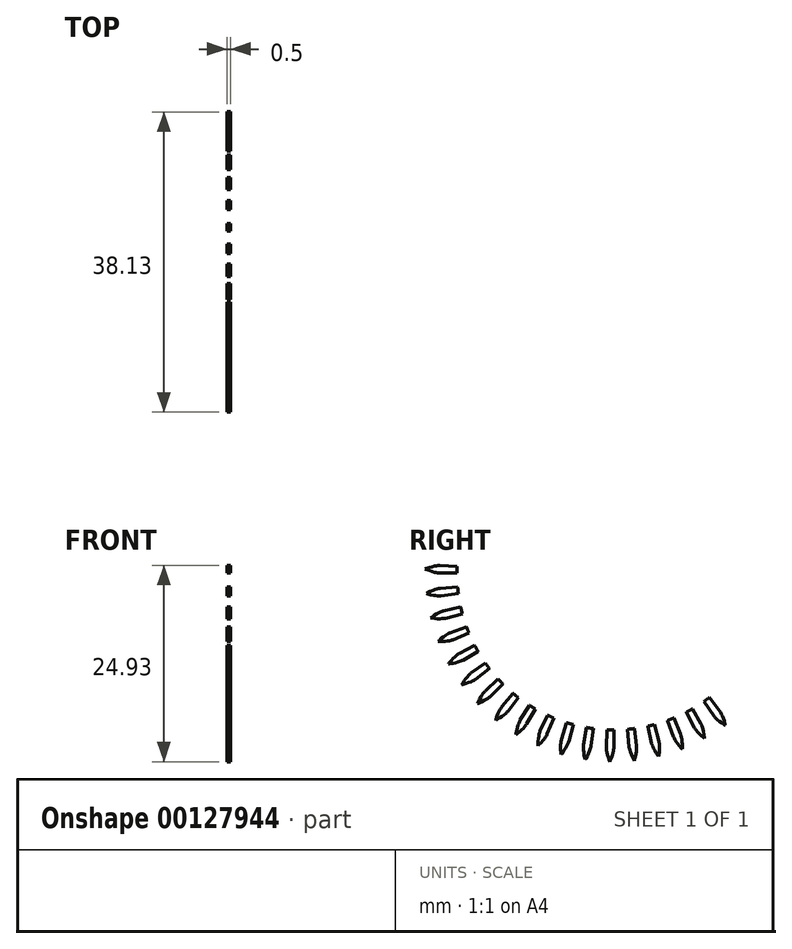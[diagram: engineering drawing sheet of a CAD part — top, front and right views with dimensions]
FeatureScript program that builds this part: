
annotation { "Feature Type Name" : "Feature", "Feature Type Description" : "" }
export const myFeature = defineFeature(function(context is Context, id is Id, definition is map)
    precondition{}
    {
        {
            assignVariable(context, id + "F0", {"name" : "GearThickness", "anyValue" : .5});
        }
        {
            var Q0;
            Q0=qCreatedBy(makeId("Right.planeOp"),FACE);
            var sketch = newSketch(context, id + "F1", { "sketchPlane" : qUnion([Q0])});
            skCircle(sketch, "E0", {"center": v(0, 0) * mm, "radius": 19.92 * mm});
            skCircle(sketch, "E1", {"center": v(0, 0) * mm, "radius": 22.13 * mm, "construction": true});
            skCircle(sketch, "E2", {"center": v(0, 0) * mm, "radius": 22.86 * mm, "construction": true});
            skCircle(sketch, "E3", {"center": v(0, 0) * mm, "radius": 25.4 * mm});
            skLineSegment(sketch, "E4", {"start": v(0, 0) * mm, "end": v(-22.13, 0) * mm, "construction": true});
            skLineSegment(sketch, "E5.1.0", {"start": v(0, 0) * mm, "end": v(-22.1, 1.1) * mm, "construction": true});
            skLineSegment(sketch, "E5.2.0", {"start": v(0, 0) * mm, "end": v(-22.02, 2.2) * mm, "construction": true});
            skLineSegment(sketch, "E5.3.0", {"start": v(0, 0) * mm, "end": v(-21.88, 3.3) * mm, "construction": true});
            skLineSegment(sketch, "E5.4.0", {"start": v(0, 0) * mm, "end": v(-21.7, 4.4) * mm, "construction": true});
            skLineSegment(sketch, "E5.5.0", {"start": v(0, 0) * mm, "end": v(-21.44, 5.48) * mm, "construction": true});
            skLineSegment(sketch, "E5.6.0", {"start": v(0, 0) * mm, "end": v(-21.14, 6.54) * mm, "construction": true});
            skLineSegment(sketch, "E5.7.0", {"start": v(0, 0) * mm, "end": v(-20.8, 7.59) * mm, "construction": true});
            skLineSegment(sketch, "E5.8.0", {"start": v(0, 0) * mm, "end": v(-20.38, 8.62) * mm, "construction": true});
            skLineSegment(sketch, "E5.9.0", {"start": v(0, 0) * mm, "end": v(-19.93, 9.63) * mm, "construction": true});
            skLineSegment(sketch, "E5.10.0", {"start": v(0, 0) * mm, "end": v(-19.42, 10.61) * mm, "construction": true});
            skLineSegment(sketch, "E5.11.0", {"start": v(0, 0) * mm, "end": v(-18.87, 11.57) * mm, "construction": true});
            skLineSegment(sketch, "E5.12.0", {"start": v(0, 0) * mm, "end": v(-18.27, 12.5) * mm, "construction": true});
            skLineSegment(sketch, "E5.13.0", {"start": v(0, 0) * mm, "end": v(-17.62, 13.4) * mm, "construction": true});
            skLineSegment(sketch, "E5.14.0", {"start": v(0, 0) * mm, "end": v(-16.93, 14.26) * mm, "construction": true});
            skLineSegment(sketch, "E5.anchor2", {"start": v(0, 0) * mm, "end": v(-16.93, 14.26) * mm, "construction": true});
            skLineSegment(sketch, "E6", {"start": v(-22.1, 1.1) * mm, "end": v(-22.16, 0) * mm, "construction": true});
            skLineSegment(sketch, "E7", {"start": v(-22.02, 2.2) * mm, "end": v(-22.24, 0) * mm, "construction": true});
            skLineSegment(sketch, "E8", {"start": v(-21.88, 3.3) * mm, "end": v(-22.38, 0.02) * mm, "construction": true});
            skLineSegment(sketch, "E9", {"start": v(-21.44, 5.48) * mm, "end": v(-22.81, 0.11) * mm, "construction": true});
            skLineSegment(sketch, "E10", {"start": v(-21.14, 6.54) * mm, "end": v(-23.1, 0.2) * mm, "construction": true});
            skLineSegment(sketch, "E11", {"start": v(-20.8, 7.59) * mm, "end": v(-23.45, 0.31) * mm, "construction": true});
            skLineSegment(sketch, "E12", {"start": v(-20.38, 8.62) * mm, "end": v(-23.83, 0.46) * mm, "construction": true});
            skLineSegment(sketch, "E13", {"start": v(-19.93, 9.63) * mm, "end": v(-24.26, 0.66) * mm, "construction": true});
            skLineSegment(sketch, "E14", {"start": v(-19.42, 10.61) * mm, "end": v(-24.73, 0.9) * mm, "construction": true});
            skLineSegment(sketch, "E15", {"start": v(-18.87, 11.57) * mm, "end": v(-25.23, 1.2) * mm, "construction": true});
            skLineSegment(sketch, "E16", {"start": v(-21.7, 4.4) * mm, "end": v(-22.57, 0.06) * mm, "construction": true});
            skLineSegment(sketch, "E17", {"start": v(-18.27, 12.5) * mm, "end": v(-25.76, 1.54) * mm, "construction": true});
            skLineSegment(sketch, "E18", {"start": v(-17.62, 13.4) * mm, "end": v(-26.32, 1.94) * mm, "construction": true});
            skLineSegment(sketch, "E19", {"start": v(-16.93, 14.26) * mm, "end": v(-26.9, 2.4) * mm, "construction": true});
            skLineSegment(sketch, "E20", {"start": v(0, 0) * mm, "end": v(-22.05, 1.93) * mm, "construction": true});
            skLineSegment(sketch, "E21", {"start": v(-19.92, 0) * mm, "end": v(-22.13, 0) * mm});
            skLineSegment(sketch, "E22.MirrorCS", {"start": v(-19.62, 3.46) * mm, "end": v(-21.8, 3.84) * mm});
            skLineSegment(sketch, "E23", {"start": v(-22.13, 0) * mm, "end": v(-22.16, 0) * mm});
            skLineSegment(sketch, "E24", {"start": v(-22.16, 0) * mm, "end": v(-22.24, 0) * mm});
            skLineSegment(sketch, "E25", {"start": v(-22.24, 0) * mm, "end": v(-22.38, 0.02) * mm});
            skLineSegment(sketch, "E26", {"start": v(-22.38, 0.02) * mm, "end": v(-22.57, 0.06) * mm});
            skLineSegment(sketch, "E27", {"start": v(-22.57, 0.06) * mm, "end": v(-22.81, 0.11) * mm});
            skLineSegment(sketch, "E28", {"start": v(-22.81, 0.11) * mm, "end": v(-23.1, 0.2) * mm});
            skLineSegment(sketch, "E29", {"start": v(-23.1, 0.2) * mm, "end": v(-23.45, 0.31) * mm});
            skLineSegment(sketch, "E30", {"start": v(-23.45, 0.31) * mm, "end": v(-23.83, 0.46) * mm});
            skLineSegment(sketch, "E31", {"start": v(-23.83, 0.46) * mm, "end": v(-24.26, 0.66) * mm});
            skLineSegment(sketch, "E32", {"start": v(-24.26, 0.66) * mm, "end": v(-24.73, 0.9) * mm});
            skLineSegment(sketch, "E33", {"start": v(-24.73, 0.9) * mm, "end": v(-25.23, 1.2) * mm});
            skLineSegment(sketch, "E34", {"start": v(-25.23, 1.2) * mm, "end": v(-25.76, 1.54) * mm});
            skLineSegment(sketch, "E35", {"start": v(-25.76, 1.54) * mm, "end": v(-26.32, 1.94) * mm});
            skLineSegment(sketch, "E36", {"start": v(-26.32, 1.94) * mm, "end": v(-26.9, 2.4) * mm});
            skLineSegment(sketch, "E37.MirrorCS", {"start": v(-21.8, 3.84) * mm, "end": v(-21.82, 3.85) * mm});
            skLineSegment(sketch, "E38.MirrorCS", {"start": v(-21.82, 3.85) * mm, "end": v(-21.9, 3.86) * mm});
            skLineSegment(sketch, "E39.MirrorCS", {"start": v(-21.9, 3.86) * mm, "end": v(-22.04, 3.86) * mm});
            skLineSegment(sketch, "E40.MirrorCS", {"start": v(-22.04, 3.86) * mm, "end": v(-22.24, 3.86) * mm});
            skLineSegment(sketch, "E41.MirrorCS", {"start": v(-22.49, 3.85) * mm, "end": v(-22.79, 3.82) * mm});
            skLineSegment(sketch, "E42.MirrorCS", {"start": v(-22.79, 3.82) * mm, "end": v(-23.14, 3.76) * mm});
            skLineSegment(sketch, "E43.MirrorCS", {"start": v(-23.14, 3.76) * mm, "end": v(-23.55, 3.68) * mm});
            skLineSegment(sketch, "E44.MirrorCS", {"start": v(-23.55, 3.68) * mm, "end": v(-24, 3.56) * mm});
            skLineSegment(sketch, "E45.MirrorCS", {"start": v(-24.5, 3.4) * mm, "end": v(-25.05, 3.2) * mm});
            skLineSegment(sketch, "E46.MirrorCS", {"start": v(-24, 3.56) * mm, "end": v(-24.5, 3.4) * mm});
            skLineSegment(sketch, "E47.MirrorCS", {"start": v(-25.05, 3.2) * mm, "end": v(-25.64, 2.96) * mm});
            skLineSegment(sketch, "E48.MirrorCS", {"start": v(-25.64, 2.96) * mm, "end": v(-26.26, 2.66) * mm});
            skLineSegment(sketch, "E49.MirrorCS", {"start": v(-26.26, 2.66) * mm, "end": v(-26.92, 2.3) * mm});
            skLineSegment(sketch, "E50.MirrorCS", {"start": v(-22.24, 3.86) * mm, "end": v(-22.49, 3.85) * mm});
            skLineSegment(sketch, "E51.1.0", {"start": v(-19.75, -2.6) * mm, "end": v(-21.94, -2.89) * mm});
            skLineSegment(sketch, "E51.1.1", {"start": v(-25.26, -0.09) * mm, "end": v(-25.8, -0.41) * mm});
            skLineSegment(sketch, "E51.1.2", {"start": v(-19.9, 0.87) * mm, "end": v(-22.11, 0.97) * mm});
            skLineSegment(sketch, "E51.1.3", {"start": v(-24.74, 0.18) * mm, "end": v(-25.26, -0.09) * mm});
            skLineSegment(sketch, "E51.1.4", {"start": v(-24.63, -2.34) * mm, "end": v(-25.17, -2.11) * mm});
            skLineSegment(sketch, "E51.1.5", {"start": v(-25.17, -2.11) * mm, "end": v(-25.74, -1.84) * mm});
            skLineSegment(sketch, "E51.1.6", {"start": v(-24.27, 0.4) * mm, "end": v(-24.74, 0.18) * mm});
            skLineSegment(sketch, "E51.1.7", {"start": v(-26.38, -0.8) * mm, "end": v(-26.99, -1.23) * mm});
            skLineSegment(sketch, "E51.1.8", {"start": v(-23.83, 0.58) * mm, "end": v(-24.27, 0.4) * mm});
            skLineSegment(sketch, "E51.1.9", {"start": v(-26.35, -1.51) * mm, "end": v(-27, -1.12) * mm});
            skLineSegment(sketch, "E51.1.10", {"start": v(-25.8, -0.41) * mm, "end": v(-26.38, -0.8) * mm});
            skLineSegment(sketch, "E51.1.11", {"start": v(-24.14, -2.51) * mm, "end": v(-24.63, -2.34) * mm});
            skLineSegment(sketch, "E51.1.12", {"start": v(-25.74, -1.84) * mm, "end": v(-26.35, -1.51) * mm});
            skLineSegment(sketch, "E51.1.13", {"start": v(-22.8, 0.88) * mm, "end": v(-23.1, 0.81) * mm});
            skLineSegment(sketch, "E51.1.14", {"start": v(-23.1, 0.81) * mm, "end": v(-23.44, 0.71) * mm});
            skLineSegment(sketch, "E51.1.15", {"start": v(-23.44, 0.71) * mm, "end": v(-23.83, 0.58) * mm});
            skLineSegment(sketch, "E51.1.16", {"start": v(-23.29, -2.75) * mm, "end": v(-23.69, -2.65) * mm});
            skLineSegment(sketch, "E51.1.17", {"start": v(-22.93, -2.82) * mm, "end": v(-23.29, -2.75) * mm});
            skLineSegment(sketch, "E51.1.18", {"start": v(-23.69, -2.65) * mm, "end": v(-24.14, -2.51) * mm});
            skLineSegment(sketch, "E51.1.19", {"start": v(-22.55, 0.93) * mm, "end": v(-22.8, 0.88) * mm});
            skLineSegment(sketch, "E51.1.20", {"start": v(-22.36, 0.95) * mm, "end": v(-22.55, 0.93) * mm});
            skLineSegment(sketch, "E51.1.21", {"start": v(-22.63, -2.86) * mm, "end": v(-22.93, -2.82) * mm});
            skLineSegment(sketch, "E51.1.22", {"start": v(-22.38, -2.89) * mm, "end": v(-22.63, -2.86) * mm});
            skLineSegment(sketch, "E51.1.23", {"start": v(-22.05, -2.9) * mm, "end": v(-22.2, -2.9) * mm});
            skLineSegment(sketch, "E51.1.24", {"start": v(-22.11, 0.97) * mm, "end": v(-22.14, 0.97) * mm});
            skLineSegment(sketch, "E51.1.25", {"start": v(-22.14, 0.97) * mm, "end": v(-22.22, 0.96) * mm});
            skLineSegment(sketch, "E51.1.26", {"start": v(-22.2, -2.9) * mm, "end": v(-22.38, -2.89) * mm});
            skLineSegment(sketch, "E51.1.27", {"start": v(-22.22, 0.96) * mm, "end": v(-22.36, 0.95) * mm});
            skLineSegment(sketch, "E51.1.28", {"start": v(-21.97, -2.9) * mm, "end": v(-22.05, -2.9) * mm});
            skLineSegment(sketch, "E51.1.29", {"start": v(-21.94, -2.89) * mm, "end": v(-21.97, -2.9) * mm});
            skLineSegment(sketch, "E51.2.0", {"start": v(-19.24, -5.16) * mm, "end": v(-21.38, -5.73) * mm});
            skLineSegment(sketch, "E51.2.1", {"start": v(-25.03, -3.39) * mm, "end": v(-25.53, -3.78) * mm});
            skLineSegment(sketch, "E51.2.2", {"start": v(-19.85, -1.74) * mm, "end": v(-22.05, -1.93) * mm});
            skLineSegment(sketch, "E51.2.3", {"start": v(-24.56, -3.05) * mm, "end": v(-25.03, -3.39) * mm});
            skLineSegment(sketch, "E51.2.4", {"start": v(-24.12, -5.53) * mm, "end": v(-24.68, -5.38) * mm});
            skLineSegment(sketch, "E51.2.5", {"start": v(-24.68, -5.38) * mm, "end": v(-25.28, -5.18) * mm});
            skLineSegment(sketch, "E51.2.6", {"start": v(-24.11, -2.77) * mm, "end": v(-24.56, -3.05) * mm});
            skLineSegment(sketch, "E51.2.7", {"start": v(-26.06, -4.23) * mm, "end": v(-26.6, -4.74) * mm});
            skLineSegment(sketch, "E51.2.8", {"start": v(-23.7, -2.54) * mm, "end": v(-24.11, -2.77) * mm});
            skLineSegment(sketch, "E51.2.9", {"start": v(-25.93, -4.94) * mm, "end": v(-26.61, -4.64) * mm});
            skLineSegment(sketch, "E51.2.10", {"start": v(-25.53, -3.78) * mm, "end": v(-26.06, -4.23) * mm});
            skLineSegment(sketch, "E51.2.11", {"start": v(-23.6, -5.64) * mm, "end": v(-24.12, -5.53) * mm});
            skLineSegment(sketch, "E51.2.12", {"start": v(-25.28, -5.18) * mm, "end": v(-25.93, -4.94) * mm});
            skLineSegment(sketch, "E51.2.13", {"start": v(-22.72, -2.1) * mm, "end": v(-23, -2.21) * mm});
            skLineSegment(sketch, "E51.2.14", {"start": v(-23, -2.21) * mm, "end": v(-23.33, -2.35) * mm});
            skLineSegment(sketch, "E51.2.15", {"start": v(-23.33, -2.35) * mm, "end": v(-23.7, -2.54) * mm});
            skLineSegment(sketch, "E51.2.16", {"start": v(-22.73, -5.77) * mm, "end": v(-23.14, -5.72) * mm});
            skLineSegment(sketch, "E51.2.17", {"start": v(-22.37, -5.79) * mm, "end": v(-22.73, -5.77) * mm});
            skLineSegment(sketch, "E51.2.18", {"start": v(-23.14, -5.72) * mm, "end": v(-23.6, -5.64) * mm});
            skLineSegment(sketch, "E51.2.19", {"start": v(-22.48, -2.03) * mm, "end": v(-22.72, -2.1) * mm});
            skLineSegment(sketch, "E51.2.20", {"start": v(-22.3, -1.98) * mm, "end": v(-22.48, -2.03) * mm});
            skLineSegment(sketch, "E51.2.21", {"start": v(-22.07, -5.8) * mm, "end": v(-22.37, -5.79) * mm});
            skLineSegment(sketch, "E51.2.22", {"start": v(-21.82, -5.78) * mm, "end": v(-22.07, -5.8) * mm});
            skLineSegment(sketch, "E51.2.23", {"start": v(-21.49, -5.75) * mm, "end": v(-21.62, -5.77) * mm});
            skLineSegment(sketch, "E51.2.24", {"start": v(-22.05, -1.93) * mm, "end": v(-22.08, -1.93) * mm});
            skLineSegment(sketch, "E51.2.25", {"start": v(-22.08, -1.93) * mm, "end": v(-22.16, -1.95) * mm});
            skLineSegment(sketch, "E51.2.26", {"start": v(-21.62, -5.77) * mm, "end": v(-21.82, -5.78) * mm});
            skLineSegment(sketch, "E51.2.27", {"start": v(-22.16, -1.95) * mm, "end": v(-22.3, -1.98) * mm});
            skLineSegment(sketch, "E51.2.28", {"start": v(-21.4, -5.73) * mm, "end": v(-21.49, -5.75) * mm});
            skLineSegment(sketch, "E51.2.29", {"start": v(-21.38, -5.73) * mm, "end": v(-21.4, -5.73) * mm});
            skLineSegment(sketch, "E51.3.0", {"start": v(-18.4, -7.62) * mm, "end": v(-20.45, -8.47) * mm});
            skLineSegment(sketch, "E51.3.1", {"start": v(-24.37, -6.62) * mm, "end": v(-24.82, -7.08) * mm});
            skLineSegment(sketch, "E51.3.2", {"start": v(-19.45, -4.31) * mm, "end": v(-21.6, -4.8) * mm});
            skLineSegment(sketch, "E51.3.3", {"start": v(-23.95, -6.23) * mm, "end": v(-24.37, -6.62) * mm});
            skLineSegment(sketch, "E51.3.4", {"start": v(-23.19, -8.63) * mm, "end": v(-23.77, -8.56) * mm});
            skLineSegment(sketch, "E51.3.5", {"start": v(-23.77, -8.56) * mm, "end": v(-24.4, -8.44) * mm});
            skLineSegment(sketch, "E51.3.6", {"start": v(-23.54, -5.9) * mm, "end": v(-23.95, -6.23) * mm});
            skLineSegment(sketch, "E51.3.7", {"start": v(-25.28, -7.6) * mm, "end": v(-25.75, -8.18) * mm});
            skLineSegment(sketch, "E51.3.8", {"start": v(-23.17, -5.61) * mm, "end": v(-23.54, -5.9) * mm});
            skLineSegment(sketch, "E51.3.9", {"start": v(-25.06, -8.28) * mm, "end": v(-25.78, -8.07) * mm});
            skLineSegment(sketch, "E51.3.10", {"start": v(-24.82, -7.08) * mm, "end": v(-25.28, -7.6) * mm});
            skLineSegment(sketch, "E51.3.11", {"start": v(-22.67, -8.68) * mm, "end": v(-23.19, -8.63) * mm});
            skLineSegment(sketch, "E51.3.12", {"start": v(-24.4, -8.44) * mm, "end": v(-25.06, -8.28) * mm});
            skLineSegment(sketch, "E51.3.13", {"start": v(-22.25, -5.05) * mm, "end": v(-22.52, -5.2) * mm});
            skLineSegment(sketch, "E51.3.14", {"start": v(-22.52, -5.2) * mm, "end": v(-22.82, -5.38) * mm});
            skLineSegment(sketch, "E51.3.15", {"start": v(-22.82, -5.38) * mm, "end": v(-23.17, -5.61) * mm});
            skLineSegment(sketch, "E51.3.16", {"start": v(-21.78, -8.68) * mm, "end": v(-22.2, -8.7) * mm});
            skLineSegment(sketch, "E51.3.17", {"start": v(-21.42, -8.66) * mm, "end": v(-21.78, -8.68) * mm});
            skLineSegment(sketch, "E51.3.18", {"start": v(-22.2, -8.7) * mm, "end": v(-22.67, -8.68) * mm});
            skLineSegment(sketch, "E51.3.19", {"start": v(-22.02, -4.94) * mm, "end": v(-22.25, -5.05) * mm});
            skLineSegment(sketch, "E51.3.20", {"start": v(-21.84, -4.87) * mm, "end": v(-22.02, -4.94) * mm});
            skLineSegment(sketch, "E51.3.21", {"start": v(-21.12, -8.62) * mm, "end": v(-21.42, -8.66) * mm});
            skLineSegment(sketch, "E51.3.22", {"start": v(-20.87, -8.58) * mm, "end": v(-21.12, -8.62) * mm});
            skLineSegment(sketch, "E51.3.23", {"start": v(-20.55, -8.5) * mm, "end": v(-20.69, -8.54) * mm});
            skLineSegment(sketch, "E51.3.24", {"start": v(-21.6, -4.8) * mm, "end": v(-21.63, -4.8) * mm});
            skLineSegment(sketch, "E51.3.25", {"start": v(-21.63, -4.8) * mm, "end": v(-21.71, -4.82) * mm});
            skLineSegment(sketch, "E51.3.26", {"start": v(-20.69, -8.54) * mm, "end": v(-20.87, -8.58) * mm});
            skLineSegment(sketch, "E51.3.27", {"start": v(-21.71, -4.82) * mm, "end": v(-21.84, -4.87) * mm});
            skLineSegment(sketch, "E51.3.28", {"start": v(-20.47, -8.48) * mm, "end": v(-20.55, -8.5) * mm});
            skLineSegment(sketch, "E51.3.29", {"start": v(-20.45, -8.47) * mm, "end": v(-20.47, -8.48) * mm});
            skLineSegment(sketch, "E51.4.0", {"start": v(-17.25, -9.96) * mm, "end": v(-19.17, -11.07) * mm});
            skLineSegment(sketch, "E51.4.1", {"start": v(-23.3, -9.75) * mm, "end": v(-23.68, -10.26) * mm});
            skLineSegment(sketch, "E51.4.2", {"start": v(-18.72, -6.81) * mm, "end": v(-20.8, -7.57) * mm});
            skLineSegment(sketch, "E51.4.3", {"start": v(-22.93, -9.3) * mm, "end": v(-23.3, -9.75) * mm});
            skLineSegment(sketch, "E51.4.4", {"start": v(-21.86, -11.59) * mm, "end": v(-22.45, -11.58) * mm});
            skLineSegment(sketch, "E51.4.5", {"start": v(-22.45, -11.58) * mm, "end": v(-23.08, -11.55) * mm});
            skLineSegment(sketch, "E51.4.6", {"start": v(-22.57, -8.92) * mm, "end": v(-22.93, -9.3) * mm});
            skLineSegment(sketch, "E51.4.7", {"start": v(-24.07, -10.83) * mm, "end": v(-24.46, -11.47) * mm});
            skLineSegment(sketch, "E51.4.8", {"start": v(-22.24, -8.59) * mm, "end": v(-22.57, -8.92) * mm});
            skLineSegment(sketch, "E51.4.9", {"start": v(-23.77, -11.48) * mm, "end": v(-24.5, -11.37) * mm});
            skLineSegment(sketch, "E51.4.10", {"start": v(-23.68, -10.26) * mm, "end": v(-24.07, -10.83) * mm});
            skLineSegment(sketch, "E51.4.11", {"start": v(-21.34, -11.56) * mm, "end": v(-21.86, -11.59) * mm});
            skLineSegment(sketch, "E51.4.12", {"start": v(-23.08, -11.55) * mm, "end": v(-23.77, -11.48) * mm});
            skLineSegment(sketch, "E51.4.13", {"start": v(-21.4, -7.91) * mm, "end": v(-21.64, -8.09) * mm});
            skLineSegment(sketch, "E51.4.14", {"start": v(-21.64, -8.09) * mm, "end": v(-21.93, -8.31) * mm});
            skLineSegment(sketch, "E51.4.15", {"start": v(-21.93, -8.31) * mm, "end": v(-22.24, -8.59) * mm});
            skLineSegment(sketch, "E51.4.16", {"start": v(-20.46, -11.45) * mm, "end": v(-20.87, -11.51) * mm});
            skLineSegment(sketch, "E51.4.17", {"start": v(-20.1, -11.38) * mm, "end": v(-20.46, -11.45) * mm});
            skLineSegment(sketch, "E51.4.18", {"start": v(-20.87, -11.51) * mm, "end": v(-21.34, -11.56) * mm});
            skLineSegment(sketch, "E51.4.19", {"start": v(-21.19, -7.77) * mm, "end": v(-21.4, -7.91) * mm});
            skLineSegment(sketch, "E51.4.20", {"start": v(-21.02, -7.68) * mm, "end": v(-21.19, -7.77) * mm});
            skLineSegment(sketch, "E51.4.21", {"start": v(-19.81, -11.3) * mm, "end": v(-20.1, -11.38) * mm});
            skLineSegment(sketch, "E51.4.22", {"start": v(-19.58, -11.23) * mm, "end": v(-19.81, -11.3) * mm});
            skLineSegment(sketch, "E51.4.23", {"start": v(-19.27, -11.11) * mm, "end": v(-19.4, -11.17) * mm});
            skLineSegment(sketch, "E51.4.24", {"start": v(-20.8, -7.57) * mm, "end": v(-20.82, -7.58) * mm});
            skLineSegment(sketch, "E51.4.25", {"start": v(-20.82, -7.58) * mm, "end": v(-20.9, -7.61) * mm});
            skLineSegment(sketch, "E51.4.26", {"start": v(-19.4, -11.17) * mm, "end": v(-19.58, -11.23) * mm});
            skLineSegment(sketch, "E51.4.27", {"start": v(-20.9, -7.61) * mm, "end": v(-21.02, -7.68) * mm});
            skLineSegment(sketch, "E51.4.28", {"start": v(-19.2, -11.08) * mm, "end": v(-19.27, -11.11) * mm});
            skLineSegment(sketch, "E51.4.29", {"start": v(-19.17, -11.07) * mm, "end": v(-19.2, -11.08) * mm});
            skLineSegment(sketch, "E51.5.0", {"start": v(-15.8, -12.13) * mm, "end": v(-17.56, -13.47) * mm});
            skLineSegment(sketch, "E51.5.1", {"start": v(-21.83, -12.7) * mm, "end": v(-22.14, -13.26) * mm});
            skLineSegment(sketch, "E51.5.2", {"start": v(-17.67, -9.2) * mm, "end": v(-19.63, -10.22) * mm});
            skLineSegment(sketch, "E51.5.3", {"start": v(-21.52, -12.22) * mm, "end": v(-21.83, -12.7) * mm});
            skLineSegment(sketch, "E51.5.4", {"start": v(-20.17, -14.34) * mm, "end": v(-20.74, -14.41) * mm});
            skLineSegment(sketch, "E51.5.5", {"start": v(-20.74, -14.41) * mm, "end": v(-21.38, -14.46) * mm});
            skLineSegment(sketch, "E51.5.6", {"start": v(-21.22, -11.79) * mm, "end": v(-21.52, -12.22) * mm});
            skLineSegment(sketch, "E51.5.7", {"start": v(-22.45, -13.88) * mm, "end": v(-22.76, -14.56) * mm});
            skLineSegment(sketch, "E51.5.8", {"start": v(-20.92, -11.42) * mm, "end": v(-21.22, -11.79) * mm});
            skLineSegment(sketch, "E51.5.9", {"start": v(-22.07, -14.49) * mm, "end": v(-22.81, -14.47) * mm});
            skLineSegment(sketch, "E51.5.10", {"start": v(-22.14, -13.26) * mm, "end": v(-22.45, -13.88) * mm});
            skLineSegment(sketch, "E51.5.11", {"start": v(-19.65, -14.25) * mm, "end": v(-20.17, -14.34) * mm});
            skLineSegment(sketch, "E51.5.12", {"start": v(-21.38, -14.46) * mm, "end": v(-22.07, -14.49) * mm});
            skLineSegment(sketch, "E51.5.13", {"start": v(-20.18, -10.64) * mm, "end": v(-20.4, -10.84) * mm});
            skLineSegment(sketch, "E51.5.14", {"start": v(-20.4, -10.84) * mm, "end": v(-20.65, -11.1) * mm});
            skLineSegment(sketch, "E51.5.15", {"start": v(-20.65, -11.1) * mm, "end": v(-20.92, -11.42) * mm});
            skLineSegment(sketch, "E51.5.16", {"start": v(-18.8, -14.03) * mm, "end": v(-19.2, -14.14) * mm});
            skLineSegment(sketch, "E51.5.17", {"start": v(-18.45, -13.9) * mm, "end": v(-18.8, -14.03) * mm});
            skLineSegment(sketch, "E51.5.18", {"start": v(-19.2, -14.14) * mm, "end": v(-19.65, -14.25) * mm});
            skLineSegment(sketch, "E51.5.19", {"start": v(-20, -10.47) * mm, "end": v(-20.18, -10.64) * mm});
            skLineSegment(sketch, "E51.5.20", {"start": v(-19.84, -10.36) * mm, "end": v(-20, -10.47) * mm});
            skLineSegment(sketch, "E51.5.21", {"start": v(-18.17, -13.8) * mm, "end": v(-18.45, -13.9) * mm});
            skLineSegment(sketch, "E51.5.22", {"start": v(-17.94, -13.7) * mm, "end": v(-18.17, -13.8) * mm});
            skLineSegment(sketch, "E51.5.23", {"start": v(-17.65, -13.53) * mm, "end": v(-17.77, -13.6) * mm});
            skLineSegment(sketch, "E51.5.24", {"start": v(-19.63, -10.22) * mm, "end": v(-19.66, -10.23) * mm});
            skLineSegment(sketch, "E51.5.25", {"start": v(-19.66, -10.23) * mm, "end": v(-19.73, -10.28) * mm});
            skLineSegment(sketch, "E51.5.26", {"start": v(-17.77, -13.6) * mm, "end": v(-17.94, -13.7) * mm});
            skLineSegment(sketch, "E51.5.27", {"start": v(-19.73, -10.28) * mm, "end": v(-19.84, -10.36) * mm});
            skLineSegment(sketch, "E51.5.28", {"start": v(-17.58, -13.49) * mm, "end": v(-17.65, -13.53) * mm});
            skLineSegment(sketch, "E51.5.29", {"start": v(-17.56, -13.47) * mm, "end": v(-17.58, -13.49) * mm});
            skLineSegment(sketch, "E51.6.0", {"start": v(-14.09, -14.09) * mm, "end": v(-15.65, -15.65) * mm});
            skLineSegment(sketch, "E51.6.1", {"start": v(-19.98, -15.45) * mm, "end": v(-20.22, -16.04) * mm});
            skLineSegment(sketch, "E51.6.2", {"start": v(-16.32, -11.43) * mm, "end": v(-18.13, -12.7) * mm});
            skLineSegment(sketch, "E51.6.3", {"start": v(-19.74, -14.92) * mm, "end": v(-19.98, -15.45) * mm});
            skLineSegment(sketch, "E51.6.4", {"start": v(-18.12, -16.85) * mm, "end": v(-18.68, -17) * mm});
            skLineSegment(sketch, "E51.6.5", {"start": v(-18.68, -17) * mm, "end": v(-19.3, -17.13) * mm});
            skLineSegment(sketch, "E51.6.6", {"start": v(-19.5, -14.45) * mm, "end": v(-19.74, -14.92) * mm});
            skLineSegment(sketch, "E51.6.7", {"start": v(-20.45, -16.69) * mm, "end": v(-20.66, -17.4) * mm});
            skLineSegment(sketch, "E51.6.8", {"start": v(-19.26, -14.05) * mm, "end": v(-19.5, -14.45) * mm});
            skLineSegment(sketch, "E51.6.9", {"start": v(-19.99, -17.24) * mm, "end": v(-20.73, -17.32) * mm});
            skLineSegment(sketch, "E51.6.10", {"start": v(-20.22, -16.04) * mm, "end": v(-20.45, -16.69) * mm});
            skLineSegment(sketch, "E51.6.11", {"start": v(-17.62, -16.69) * mm, "end": v(-18.12, -16.85) * mm});
            skLineSegment(sketch, "E51.6.12", {"start": v(-19.3, -17.13) * mm, "end": v(-19.99, -17.24) * mm});
            skLineSegment(sketch, "E51.6.13", {"start": v(-18.62, -13.18) * mm, "end": v(-18.81, -13.41) * mm});
            skLineSegment(sketch, "E51.6.14", {"start": v(-18.81, -13.41) * mm, "end": v(-19.03, -13.7) * mm});
            skLineSegment(sketch, "E51.6.15", {"start": v(-19.03, -13.7) * mm, "end": v(-19.26, -14.05) * mm});
            skLineSegment(sketch, "E51.6.16", {"start": v(-16.8, -16.36) * mm, "end": v(-17.18, -16.52) * mm});
            skLineSegment(sketch, "E51.6.17", {"start": v(-16.48, -16.2) * mm, "end": v(-16.8, -16.36) * mm});
            skLineSegment(sketch, "E51.6.18", {"start": v(-17.18, -16.52) * mm, "end": v(-17.62, -16.69) * mm});
            skLineSegment(sketch, "E51.6.19", {"start": v(-18.45, -13) * mm, "end": v(-18.62, -13.18) * mm});
            skLineSegment(sketch, "E51.6.20", {"start": v(-18.32, -12.86) * mm, "end": v(-18.45, -13) * mm});
            skLineSegment(sketch, "E51.6.21", {"start": v(-16.21, -16.05) * mm, "end": v(-16.48, -16.2) * mm});
            skLineSegment(sketch, "E51.6.22", {"start": v(-16, -15.92) * mm, "end": v(-16.21, -16.05) * mm});
            skLineSegment(sketch, "E51.6.23", {"start": v(-15.73, -15.72) * mm, "end": v(-15.84, -15.8) * mm});
            skLineSegment(sketch, "E51.6.24", {"start": v(-18.13, -12.7) * mm, "end": v(-18.15, -12.71) * mm});
            skLineSegment(sketch, "E51.6.25", {"start": v(-18.15, -12.71) * mm, "end": v(-18.22, -12.76) * mm});
            skLineSegment(sketch, "E51.6.26", {"start": v(-15.84, -15.8) * mm, "end": v(-16, -15.92) * mm});
            skLineSegment(sketch, "E51.6.27", {"start": v(-18.22, -12.76) * mm, "end": v(-18.32, -12.86) * mm});
            skLineSegment(sketch, "E51.6.28", {"start": v(-15.67, -15.67) * mm, "end": v(-15.73, -15.72) * mm});
            skLineSegment(sketch, "E51.6.29", {"start": v(-15.65, -15.65) * mm, "end": v(-15.67, -15.67) * mm});
            skLineSegment(sketch, "E51.7.0", {"start": v(-12.13, -15.8) * mm, "end": v(-13.47, -17.56) * mm});
            skLineSegment(sketch, "E51.7.1", {"start": v(-17.8, -17.92) * mm, "end": v(-17.96, -18.54) * mm});
            skLineSegment(sketch, "E51.7.2", {"start": v(-14.69, -13.46) * mm, "end": v(-16.32, -14.95) * mm});
            skLineSegment(sketch, "E51.7.3", {"start": v(-17.62, -17.37) * mm, "end": v(-17.8, -17.92) * mm});
            skLineSegment(sketch, "E51.7.4", {"start": v(-15.77, -19.07) * mm, "end": v(-16.3, -19.3) * mm});
            skLineSegment(sketch, "E51.7.5", {"start": v(-16.3, -19.3) * mm, "end": v(-16.9, -19.5) * mm});
            skLineSegment(sketch, "E51.7.6", {"start": v(-17.44, -16.88) * mm, "end": v(-17.62, -17.37) * mm});
            skLineSegment(sketch, "E51.7.7", {"start": v(-18.1, -19.22) * mm, "end": v(-18.21, -19.95) * mm});
            skLineSegment(sketch, "E51.7.8", {"start": v(-17.26, -16.44) * mm, "end": v(-17.44, -16.88) * mm});
            skLineSegment(sketch, "E51.7.9", {"start": v(-17.57, -19.7) * mm, "end": v(-18.3, -19.88) * mm});
            skLineSegment(sketch, "E51.7.10", {"start": v(-17.96, -18.54) * mm, "end": v(-18.1, -19.22) * mm});
            skLineSegment(sketch, "E51.7.11", {"start": v(-15.3, -18.85) * mm, "end": v(-15.77, -19.07) * mm});
            skLineSegment(sketch, "E51.7.12", {"start": v(-16.9, -19.5) * mm, "end": v(-17.57, -19.7) * mm});
            skLineSegment(sketch, "E51.7.13", {"start": v(-16.74, -15.5) * mm, "end": v(-16.9, -15.76) * mm});
            skLineSegment(sketch, "E51.7.14", {"start": v(-16.9, -15.76) * mm, "end": v(-17.08, -16.07) * mm});
            skLineSegment(sketch, "E51.7.15", {"start": v(-17.08, -16.07) * mm, "end": v(-17.26, -16.44) * mm});
            skLineSegment(sketch, "E51.7.16", {"start": v(-14.52, -18.41) * mm, "end": v(-14.88, -18.62) * mm});
            skLineSegment(sketch, "E51.7.17", {"start": v(-14.22, -18.21) * mm, "end": v(-14.52, -18.41) * mm});
            skLineSegment(sketch, "E51.7.18", {"start": v(-14.88, -18.62) * mm, "end": v(-15.3, -18.85) * mm});
            skLineSegment(sketch, "E51.7.19", {"start": v(-16.6, -15.3) * mm, "end": v(-16.74, -15.5) * mm});
            skLineSegment(sketch, "E51.7.20", {"start": v(-16.48, -15.14) * mm, "end": v(-16.6, -15.3) * mm});
            skLineSegment(sketch, "E51.7.21", {"start": v(-13.98, -18.03) * mm, "end": v(-14.22, -18.21) * mm});
            skLineSegment(sketch, "E51.7.22", {"start": v(-13.79, -17.87) * mm, "end": v(-13.98, -18.03) * mm});
            skLineSegment(sketch, "E51.7.23", {"start": v(-13.55, -17.64) * mm, "end": v(-13.64, -17.74) * mm});
            skLineSegment(sketch, "E51.7.24", {"start": v(-16.32, -14.95) * mm, "end": v(-16.34, -14.97) * mm});
            skLineSegment(sketch, "E51.7.25", {"start": v(-16.34, -14.97) * mm, "end": v(-16.4, -15.03) * mm});
            skLineSegment(sketch, "E51.7.26", {"start": v(-13.64, -17.74) * mm, "end": v(-13.79, -17.87) * mm});
            skLineSegment(sketch, "E51.7.27", {"start": v(-16.4, -15.03) * mm, "end": v(-16.48, -15.14) * mm});
            skLineSegment(sketch, "E51.7.28", {"start": v(-13.5, -17.58) * mm, "end": v(-13.55, -17.64) * mm});
            skLineSegment(sketch, "E51.7.29", {"start": v(-13.47, -17.56) * mm, "end": v(-13.5, -17.58) * mm});
            skLineSegment(sketch, "E51.8.0", {"start": v(-9.96, -17.25) * mm, "end": v(-11.07, -19.17) * mm});
            skLineSegment(sketch, "E51.8.1", {"start": v(-15.3, -20.1) * mm, "end": v(-15.38, -20.72) * mm});
            skLineSegment(sketch, "E51.8.2", {"start": v(-12.8, -15.26) * mm, "end": v(-14.23, -16.95) * mm});
            skLineSegment(sketch, "E51.8.3", {"start": v(-15.2, -19.52) * mm, "end": v(-15.3, -20.1) * mm});
            skLineSegment(sketch, "E51.8.4", {"start": v(-13.14, -20.97) * mm, "end": v(-13.65, -21.25) * mm});
            skLineSegment(sketch, "E51.8.5", {"start": v(-13.65, -21.25) * mm, "end": v(-14.21, -21.54) * mm});
            skLineSegment(sketch, "E51.8.6", {"start": v(-15.09, -19) * mm, "end": v(-15.2, -19.52) * mm});
            skLineSegment(sketch, "E51.8.7", {"start": v(-15.43, -21.41) * mm, "end": v(-15.45, -22.16) * mm});
            skLineSegment(sketch, "E51.8.8", {"start": v(-14.96, -18.56) * mm, "end": v(-15.09, -19) * mm});
            skLineSegment(sketch, "E51.8.9", {"start": v(-14.84, -21.83) * mm, "end": v(-15.54, -22.1) * mm});
            skLineSegment(sketch, "E51.8.10", {"start": v(-15.38, -20.72) * mm, "end": v(-15.43, -21.41) * mm});
            skLineSegment(sketch, "E51.8.11", {"start": v(-12.7, -20.68) * mm, "end": v(-13.14, -20.97) * mm});
            skLineSegment(sketch, "E51.8.12", {"start": v(-14.21, -21.54) * mm, "end": v(-14.84, -21.83) * mm});
            skLineSegment(sketch, "E51.8.13", {"start": v(-14.58, -17.55) * mm, "end": v(-14.7, -17.83) * mm});
            skLineSegment(sketch, "E51.8.14", {"start": v(-14.7, -17.83) * mm, "end": v(-14.83, -18.16) * mm});
            skLineSegment(sketch, "E51.8.15", {"start": v(-14.83, -18.16) * mm, "end": v(-14.96, -18.56) * mm});
            skLineSegment(sketch, "E51.8.16", {"start": v(-12, -20.15) * mm, "end": v(-12.32, -20.4) * mm});
            skLineSegment(sketch, "E51.8.17", {"start": v(-11.72, -19.91) * mm, "end": v(-12, -20.15) * mm});
            skLineSegment(sketch, "E51.8.18", {"start": v(-12.32, -20.4) * mm, "end": v(-12.7, -20.68) * mm});
            skLineSegment(sketch, "E51.8.19", {"start": v(-14.46, -17.33) * mm, "end": v(-14.58, -17.55) * mm});
            skLineSegment(sketch, "E51.8.20", {"start": v(-14.37, -17.16) * mm, "end": v(-14.46, -17.33) * mm});
            skLineSegment(sketch, "E51.8.21", {"start": v(-11.5, -19.7) * mm, "end": v(-11.72, -19.91) * mm});
            skLineSegment(sketch, "E51.8.22", {"start": v(-11.34, -19.52) * mm, "end": v(-11.5, -19.7) * mm});
            skLineSegment(sketch, "E51.8.23", {"start": v(-11.13, -19.26) * mm, "end": v(-11.21, -19.37) * mm});
            skLineSegment(sketch, "E51.8.24", {"start": v(-14.23, -16.95) * mm, "end": v(-14.24, -16.98) * mm});
            skLineSegment(sketch, "E51.8.25", {"start": v(-14.24, -16.98) * mm, "end": v(-14.3, -17.04) * mm});
            skLineSegment(sketch, "E51.8.26", {"start": v(-11.21, -19.37) * mm, "end": v(-11.34, -19.52) * mm});
            skLineSegment(sketch, "E51.8.27", {"start": v(-14.3, -17.04) * mm, "end": v(-14.37, -17.16) * mm});
            skLineSegment(sketch, "E51.8.28", {"start": v(-11.08, -19.2) * mm, "end": v(-11.13, -19.26) * mm});
            skLineSegment(sketch, "E51.8.29", {"start": v(-11.07, -19.17) * mm, "end": v(-11.08, -19.2) * mm});
            skLineSegment(sketch, "E51.9.0", {"start": v(-7.62, -18.4) * mm, "end": v(-8.47, -20.45) * mm});
            skLineSegment(sketch, "E51.9.1", {"start": v(-12.55, -21.92) * mm, "end": v(-12.55, -22.56) * mm});
            skLineSegment(sketch, "E51.9.2", {"start": v(-10.7, -16.8) * mm, "end": v(-11.9, -18.67) * mm});
            skLineSegment(sketch, "E51.9.3", {"start": v(-12.53, -21.34) * mm, "end": v(-12.55, -21.92) * mm});
            skLineSegment(sketch, "E51.9.4", {"start": v(-10.3, -22.5) * mm, "end": v(-10.76, -22.85) * mm});
            skLineSegment(sketch, "E51.9.5", {"start": v(-10.76, -22.85) * mm, "end": v(-11.28, -23.21) * mm});
            skLineSegment(sketch, "E51.9.6", {"start": v(-12.48, -20.82) * mm, "end": v(-12.53, -21.34) * mm});
            skLineSegment(sketch, "E51.9.7", {"start": v(-12.5, -23.25) * mm, "end": v(-12.43, -23.99) * mm});
            skLineSegment(sketch, "E51.9.8", {"start": v(-12.41, -20.35) * mm, "end": v(-12.48, -20.82) * mm});
            skLineSegment(sketch, "E51.9.9", {"start": v(-11.87, -23.58) * mm, "end": v(-12.52, -23.94) * mm});
            skLineSegment(sketch, "E51.9.10", {"start": v(-12.55, -22.56) * mm, "end": v(-12.5, -23.25) * mm});
            skLineSegment(sketch, "E51.9.11", {"start": v(-9.9, -22.16) * mm, "end": v(-10.3, -22.5) * mm});
            skLineSegment(sketch, "E51.9.12", {"start": v(-11.28, -23.21) * mm, "end": v(-11.87, -23.58) * mm});
            skLineSegment(sketch, "E51.9.13", {"start": v(-12.16, -19.3) * mm, "end": v(-12.25, -19.6) * mm});
            skLineSegment(sketch, "E51.9.14", {"start": v(-12.25, -19.6) * mm, "end": v(-12.33, -19.94) * mm});
            skLineSegment(sketch, "E51.9.15", {"start": v(-12.33, -19.94) * mm, "end": v(-12.41, -20.35) * mm});
            skLineSegment(sketch, "E51.9.16", {"start": v(-9.26, -21.54) * mm, "end": v(-9.55, -21.84) * mm});
            skLineSegment(sketch, "E51.9.17", {"start": v(-9.02, -21.27) * mm, "end": v(-9.26, -21.54) * mm});
            skLineSegment(sketch, "E51.9.18", {"start": v(-9.55, -21.84) * mm, "end": v(-9.9, -22.16) * mm});
            skLineSegment(sketch, "E51.9.19", {"start": v(-12.08, -19.07) * mm, "end": v(-12.16, -19.3) * mm});
            skLineSegment(sketch, "E51.9.20", {"start": v(-12, -18.89) * mm, "end": v(-12.08, -19.07) * mm});
            skLineSegment(sketch, "E51.9.21", {"start": v(-8.84, -21.03) * mm, "end": v(-9.02, -21.27) * mm});
            skLineSegment(sketch, "E51.9.22", {"start": v(-8.7, -20.83) * mm, "end": v(-8.84, -21.03) * mm});
            skLineSegment(sketch, "E51.9.23", {"start": v(-8.52, -20.55) * mm, "end": v(-8.59, -20.67) * mm});
            skLineSegment(sketch, "E51.9.24", {"start": v(-11.9, -18.67) * mm, "end": v(-11.9, -18.69) * mm});
            skLineSegment(sketch, "E51.9.25", {"start": v(-11.9, -18.69) * mm, "end": v(-11.94, -18.76) * mm});
            skLineSegment(sketch, "E51.9.26", {"start": v(-8.59, -20.67) * mm, "end": v(-8.7, -20.83) * mm});
            skLineSegment(sketch, "E51.9.27", {"start": v(-11.94, -18.76) * mm, "end": v(-12, -18.89) * mm});
            skLineSegment(sketch, "E51.9.28", {"start": v(-8.48, -20.47) * mm, "end": v(-8.52, -20.55) * mm});
            skLineSegment(sketch, "E51.9.29", {"start": v(-8.47, -20.45) * mm, "end": v(-8.48, -20.47) * mm});
            skLineSegment(sketch, "E51.10.0", {"start": v(-5.16, -19.24) * mm, "end": v(-5.73, -21.38) * mm});
            skLineSegment(sketch, "E51.10.1", {"start": v(-9.58, -23.37) * mm, "end": v(-9.5, -24) * mm});
            skLineSegment(sketch, "E51.10.2", {"start": v(-8.42, -18.05) * mm, "end": v(-9.35, -20.06) * mm});
            skLineSegment(sketch, "E51.10.3", {"start": v(-9.64, -22.8) * mm, "end": v(-9.58, -23.37) * mm});
            skLineSegment(sketch, "E51.10.4", {"start": v(-7.27, -23.65) * mm, "end": v(-7.68, -24.06) * mm});
            skLineSegment(sketch, "E51.10.5", {"start": v(-7.68, -24.06) * mm, "end": v(-8.15, -24.49) * mm});
            skLineSegment(sketch, "E51.10.6", {"start": v(-9.66, -22.27) * mm, "end": v(-9.64, -22.8) * mm});
            skLineSegment(sketch, "E51.10.7", {"start": v(-9.37, -24.68) * mm, "end": v(-9.19, -25.4) * mm});
            skLineSegment(sketch, "E51.10.8", {"start": v(-9.65, -21.8) * mm, "end": v(-9.66, -22.27) * mm});
            skLineSegment(sketch, "E51.10.9", {"start": v(-8.69, -24.93) * mm, "end": v(-9.3, -25.37) * mm});
            skLineSegment(sketch, "E51.10.10", {"start": v(-9.5, -24) * mm, "end": v(-9.37, -24.68) * mm});
            skLineSegment(sketch, "E51.10.11", {"start": v(-6.92, -23.26) * mm, "end": v(-7.27, -23.65) * mm});
            skLineSegment(sketch, "E51.10.12", {"start": v(-8.15, -24.49) * mm, "end": v(-8.69, -24.93) * mm});
            skLineSegment(sketch, "E51.10.13", {"start": v(-9.54, -20.72) * mm, "end": v(-9.59, -21.02) * mm});
            skLineSegment(sketch, "E51.10.14", {"start": v(-9.59, -21.02) * mm, "end": v(-9.63, -21.38) * mm});
            skLineSegment(sketch, "E51.10.15", {"start": v(-9.63, -21.38) * mm, "end": v(-9.65, -21.8) * mm});
            skLineSegment(sketch, "E51.10.16", {"start": v(-6.37, -22.57) * mm, "end": v(-6.62, -22.9) * mm});
            skLineSegment(sketch, "E51.10.17", {"start": v(-6.17, -22.27) * mm, "end": v(-6.37, -22.57) * mm});
            skLineSegment(sketch, "E51.10.18", {"start": v(-6.62, -22.9) * mm, "end": v(-6.92, -23.26) * mm});
            skLineSegment(sketch, "E51.10.19", {"start": v(-9.49, -20.48) * mm, "end": v(-9.54, -20.72) * mm});
            skLineSegment(sketch, "E51.10.20", {"start": v(-9.44, -20.3) * mm, "end": v(-9.49, -20.48) * mm});
            skLineSegment(sketch, "E51.10.21", {"start": v(-6.02, -22) * mm, "end": v(-6.17, -22.27) * mm});
            skLineSegment(sketch, "E51.10.22", {"start": v(-5.9, -21.79) * mm, "end": v(-6.02, -22) * mm});
            skLineSegment(sketch, "E51.10.23", {"start": v(-5.76, -21.48) * mm, "end": v(-5.82, -21.61) * mm});
            skLineSegment(sketch, "E51.10.24", {"start": v(-9.35, -20.06) * mm, "end": v(-9.36, -20.08) * mm});
            skLineSegment(sketch, "E51.10.25", {"start": v(-9.36, -20.08) * mm, "end": v(-9.4, -20.16) * mm});
            skLineSegment(sketch, "E51.10.26", {"start": v(-5.82, -21.61) * mm, "end": v(-5.9, -21.79) * mm});
            skLineSegment(sketch, "E51.10.27", {"start": v(-9.4, -20.16) * mm, "end": v(-9.44, -20.3) * mm});
            skLineSegment(sketch, "E51.10.28", {"start": v(-5.74, -21.4) * mm, "end": v(-5.76, -21.48) * mm});
            skLineSegment(sketch, "E51.10.29", {"start": v(-5.73, -21.38) * mm, "end": v(-5.74, -21.4) * mm});
            skLineSegment(sketch, "E51.11.0", {"start": v(-2.6, -19.75) * mm, "end": v(-2.89, -21.94) * mm});
            skLineSegment(sketch, "E51.11.1", {"start": v(-6.45, -24.42) * mm, "end": v(-6.28, -25.03) * mm});
            skLineSegment(sketch, "E51.11.2", {"start": v(-6, -19) * mm, "end": v(-6.66, -21.1) * mm});
            skLineSegment(sketch, "E51.11.3", {"start": v(-6.58, -23.85) * mm, "end": v(-6.45, -24.42) * mm});
            skLineSegment(sketch, "E51.11.4", {"start": v(-4.12, -24.4) * mm, "end": v(-4.47, -24.86) * mm});
            skLineSegment(sketch, "E51.11.5", {"start": v(-4.47, -24.86) * mm, "end": v(-4.89, -25.34) * mm});
            skLineSegment(sketch, "E51.11.6", {"start": v(-6.67, -23.34) * mm, "end": v(-6.58, -23.85) * mm});
            skLineSegment(sketch, "E51.11.7", {"start": v(-6.06, -25.7) * mm, "end": v(-5.8, -26.39) * mm});
            skLineSegment(sketch, "E51.11.8", {"start": v(-6.72, -22.87) * mm, "end": v(-6.67, -23.34) * mm});
            skLineSegment(sketch, "E51.11.9", {"start": v(-5.36, -25.85) * mm, "end": v(-5.9, -26.36) * mm});
            skLineSegment(sketch, "E51.11.10", {"start": v(-6.28, -25.03) * mm, "end": v(-6.06, -25.7) * mm});
            skLineSegment(sketch, "E51.11.11", {"start": v(-3.82, -23.97) * mm, "end": v(-4.12, -24.4) * mm});
            skLineSegment(sketch, "E51.11.12", {"start": v(-4.89, -25.34) * mm, "end": v(-5.36, -25.85) * mm});
            skLineSegment(sketch, "E51.11.13", {"start": v(-6.75, -21.8) * mm, "end": v(-6.76, -22.1) * mm});
            skLineSegment(sketch, "E51.11.14", {"start": v(-6.76, -22.1) * mm, "end": v(-6.75, -22.45) * mm});
            skLineSegment(sketch, "E51.11.15", {"start": v(-6.75, -22.45) * mm, "end": v(-6.72, -22.87) * mm});
            skLineSegment(sketch, "E51.11.16", {"start": v(-3.37, -23.2) * mm, "end": v(-3.57, -23.57) * mm});
            skLineSegment(sketch, "E51.11.17", {"start": v(-3.21, -22.88) * mm, "end": v(-3.37, -23.2) * mm});
            skLineSegment(sketch, "E51.11.18", {"start": v(-3.57, -23.57) * mm, "end": v(-3.82, -23.97) * mm});
            skLineSegment(sketch, "E51.11.19", {"start": v(-6.73, -21.54) * mm, "end": v(-6.75, -21.8) * mm});
            skLineSegment(sketch, "E51.11.20", {"start": v(-6.7, -21.35) * mm, "end": v(-6.73, -21.54) * mm});
            skLineSegment(sketch, "E51.11.21", {"start": v(-3.1, -22.6) * mm, "end": v(-3.21, -22.88) * mm});
            skLineSegment(sketch, "E51.11.22", {"start": v(-3, -22.37) * mm, "end": v(-3.1, -22.6) * mm});
            skLineSegment(sketch, "E51.11.23", {"start": v(-2.91, -22.05) * mm, "end": v(-2.95, -22.18) * mm});
            skLineSegment(sketch, "E51.11.24", {"start": v(-6.66, -21.1) * mm, "end": v(-6.66, -21.13) * mm});
            skLineSegment(sketch, "E51.11.25", {"start": v(-6.66, -21.13) * mm, "end": v(-6.68, -21.22) * mm});
            skLineSegment(sketch, "E51.11.26", {"start": v(-2.95, -22.18) * mm, "end": v(-3, -22.37) * mm});
            skLineSegment(sketch, "E51.11.27", {"start": v(-6.68, -21.22) * mm, "end": v(-6.7, -21.35) * mm});
            skLineSegment(sketch, "E51.11.28", {"start": v(-2.9, -21.97) * mm, "end": v(-2.91, -22.05) * mm});
            skLineSegment(sketch, "E51.11.29", {"start": v(-2.89, -21.94) * mm, "end": v(-2.9, -21.97) * mm});
            skLineSegment(sketch, "E51.12.0", {"start": v(0, -19.92) * mm, "end": v(0, -22.13) * mm});
            skLineSegment(sketch, "E51.12.1", {"start": v(-3.2, -25.05) * mm, "end": v(-2.96, -25.64) * mm});
            skLineSegment(sketch, "E51.12.2", {"start": v(-3.46, -19.62) * mm, "end": v(-3.84, -21.8) * mm});
            skLineSegment(sketch, "E51.12.3", {"start": v(-3.4, -24.5) * mm, "end": v(-3.2, -25.05) * mm});
            skLineSegment(sketch, "E51.12.4", {"start": v(-0.9, -24.73) * mm, "end": v(-1.2, -25.23) * mm});
            skLineSegment(sketch, "E51.12.5", {"start": v(-1.2, -25.23) * mm, "end": v(-1.54, -25.76) * mm});
            skLineSegment(sketch, "E51.12.6", {"start": v(-3.56, -24) * mm, "end": v(-3.4, -24.5) * mm});
            skLineSegment(sketch, "E51.12.7", {"start": v(-2.66, -26.26) * mm, "end": v(-2.3, -26.92) * mm});
            skLineSegment(sketch, "E51.12.8", {"start": v(-3.68, -23.55) * mm, "end": v(-3.56, -24) * mm});
            skLineSegment(sketch, "E51.12.9", {"start": v(-1.94, -26.32) * mm, "end": v(-2.4, -26.9) * mm});
            skLineSegment(sketch, "E51.12.10", {"start": v(-2.96, -25.64) * mm, "end": v(-2.66, -26.26) * mm});
            skLineSegment(sketch, "E51.12.11", {"start": v(-0.66, -24.26) * mm, "end": v(-0.9, -24.73) * mm});
            skLineSegment(sketch, "E51.12.12", {"start": v(-1.54, -25.76) * mm, "end": v(-1.94, -26.32) * mm});
            skLineSegment(sketch, "E51.12.13", {"start": v(-3.85, -22.49) * mm, "end": v(-3.82, -22.79) * mm});
            skLineSegment(sketch, "E51.12.14", {"start": v(-3.82, -22.79) * mm, "end": v(-3.76, -23.14) * mm});
            skLineSegment(sketch, "E51.12.15", {"start": v(-3.76, -23.14) * mm, "end": v(-3.68, -23.55) * mm});
            skLineSegment(sketch, "E51.12.16", {"start": v(-0.31, -23.45) * mm, "end": v(-0.46, -23.83) * mm});
            skLineSegment(sketch, "E51.12.17", {"start": v(-0.2, -23.1) * mm, "end": v(-0.31, -23.45) * mm});
            skLineSegment(sketch, "E51.12.18", {"start": v(-0.46, -23.83) * mm, "end": v(-0.66, -24.26) * mm});
            skLineSegment(sketch, "E51.12.19", {"start": v(-3.86, -22.24) * mm, "end": v(-3.85, -22.49) * mm});
            skLineSegment(sketch, "E51.12.20", {"start": v(-3.86, -22.04) * mm, "end": v(-3.86, -22.24) * mm});
            skLineSegment(sketch, "E51.12.21", {"start": v(-0.11, -22.81) * mm, "end": v(-0.2, -23.1) * mm});
            skLineSegment(sketch, "E51.12.22", {"start": v(-0.06, -22.57) * mm, "end": v(-0.11, -22.81) * mm});
            skLineSegment(sketch, "E51.12.23", {"start": v(0, -22.24) * mm, "end": v(-0.02, -22.38) * mm});
            skLineSegment(sketch, "E51.12.24", {"start": v(-3.84, -21.8) * mm, "end": v(-3.85, -21.82) * mm});
            skLineSegment(sketch, "E51.12.25", {"start": v(-3.85, -21.82) * mm, "end": v(-3.86, -21.9) * mm});
            skLineSegment(sketch, "E51.12.26", {"start": v(-0.02, -22.38) * mm, "end": v(-0.06, -22.57) * mm});
            skLineSegment(sketch, "E51.12.27", {"start": v(-3.86, -21.9) * mm, "end": v(-3.86, -22.04) * mm});
            skLineSegment(sketch, "E51.12.28", {"start": v(0, -22.16) * mm, "end": v(0, -22.24) * mm});
            skLineSegment(sketch, "E51.12.29", {"start": v(0, -22.13) * mm, "end": v(0, -22.16) * mm});
            skLineSegment(sketch, "E51.13.0", {"start": v(2.6, -19.75) * mm, "end": v(2.89, -21.94) * mm});
            skLineSegment(sketch, "E51.13.1", {"start": v(0.09, -25.26) * mm, "end": v(0.41, -25.8) * mm});
            skLineSegment(sketch, "E51.13.2", {"start": v(-0.87, -19.9) * mm, "end": v(-0.97, -22.11) * mm});
            skLineSegment(sketch, "E51.13.3", {"start": v(-0.18, -24.74) * mm, "end": v(0.09, -25.26) * mm});
            skLineSegment(sketch, "E51.13.4", {"start": v(2.34, -24.63) * mm, "end": v(2.11, -25.17) * mm});
            skLineSegment(sketch, "E51.13.5", {"start": v(2.11, -25.17) * mm, "end": v(1.84, -25.74) * mm});
            skLineSegment(sketch, "E51.13.6", {"start": v(-0.4, -24.27) * mm, "end": v(-0.18, -24.74) * mm});
            skLineSegment(sketch, "E51.13.7", {"start": v(0.8, -26.38) * mm, "end": v(1.23, -26.99) * mm});
            skLineSegment(sketch, "E51.13.8", {"start": v(-0.58, -23.83) * mm, "end": v(-0.4, -24.27) * mm});
            skLineSegment(sketch, "E51.13.9", {"start": v(1.51, -26.35) * mm, "end": v(1.12, -27) * mm});
            skLineSegment(sketch, "E51.13.10", {"start": v(0.41, -25.8) * mm, "end": v(0.8, -26.38) * mm});
            skLineSegment(sketch, "E51.13.11", {"start": v(2.51, -24.14) * mm, "end": v(2.34, -24.63) * mm});
            skLineSegment(sketch, "E51.13.12", {"start": v(1.84, -25.74) * mm, "end": v(1.51, -26.35) * mm});
            skLineSegment(sketch, "E51.13.13", {"start": v(-0.88, -22.8) * mm, "end": v(-0.81, -23.1) * mm});
            skLineSegment(sketch, "E51.13.14", {"start": v(-0.81, -23.1) * mm, "end": v(-0.71, -23.44) * mm});
            skLineSegment(sketch, "E51.13.15", {"start": v(-0.71, -23.44) * mm, "end": v(-0.58, -23.83) * mm});
            skLineSegment(sketch, "E51.13.16", {"start": v(2.75, -23.29) * mm, "end": v(2.65, -23.69) * mm});
            skLineSegment(sketch, "E51.13.17", {"start": v(2.82, -22.93) * mm, "end": v(2.75, -23.29) * mm});
            skLineSegment(sketch, "E51.13.18", {"start": v(2.65, -23.69) * mm, "end": v(2.51, -24.14) * mm});
            skLineSegment(sketch, "E51.13.19", {"start": v(-0.93, -22.55) * mm, "end": v(-0.88, -22.8) * mm});
            skLineSegment(sketch, "E51.13.20", {"start": v(-0.95, -22.36) * mm, "end": v(-0.93, -22.55) * mm});
            skLineSegment(sketch, "E51.13.21", {"start": v(2.86, -22.63) * mm, "end": v(2.82, -22.93) * mm});
            skLineSegment(sketch, "E51.13.22", {"start": v(2.89, -22.38) * mm, "end": v(2.86, -22.63) * mm});
            skLineSegment(sketch, "E51.13.23", {"start": v(2.9, -22.05) * mm, "end": v(2.9, -22.2) * mm});
            skLineSegment(sketch, "E51.13.24", {"start": v(-0.97, -22.11) * mm, "end": v(-0.97, -22.14) * mm});
            skLineSegment(sketch, "E51.13.25", {"start": v(-0.97, -22.14) * mm, "end": v(-0.96, -22.22) * mm});
            skLineSegment(sketch, "E51.13.26", {"start": v(2.9, -22.2) * mm, "end": v(2.89, -22.38) * mm});
            skLineSegment(sketch, "E51.13.27", {"start": v(-0.96, -22.22) * mm, "end": v(-0.95, -22.36) * mm});
            skLineSegment(sketch, "E51.13.28", {"start": v(2.9, -21.97) * mm, "end": v(2.9, -22.05) * mm});
            skLineSegment(sketch, "E51.13.29", {"start": v(2.89, -21.94) * mm, "end": v(2.9, -21.97) * mm});
            skLineSegment(sketch, "E51.14.0", {"start": v(5.16, -19.24) * mm, "end": v(5.73, -21.38) * mm});
            skLineSegment(sketch, "E51.14.1", {"start": v(3.39, -25.03) * mm, "end": v(3.78, -25.53) * mm});
            skLineSegment(sketch, "E51.14.2", {"start": v(1.74, -19.85) * mm, "end": v(1.93, -22.05) * mm});
            skLineSegment(sketch, "E51.14.3", {"start": v(3.05, -24.56) * mm, "end": v(3.39, -25.03) * mm});
            skLineSegment(sketch, "E51.14.4", {"start": v(5.53, -24.12) * mm, "end": v(5.38, -24.68) * mm});
            skLineSegment(sketch, "E51.14.5", {"start": v(5.38, -24.68) * mm, "end": v(5.18, -25.28) * mm});
            skLineSegment(sketch, "E51.14.6", {"start": v(2.77, -24.11) * mm, "end": v(3.05, -24.56) * mm});
            skLineSegment(sketch, "E51.14.7", {"start": v(4.23, -26.06) * mm, "end": v(4.74, -26.6) * mm});
            skLineSegment(sketch, "E51.14.8", {"start": v(2.54, -23.7) * mm, "end": v(2.77, -24.11) * mm});
            skLineSegment(sketch, "E51.14.9", {"start": v(4.94, -25.93) * mm, "end": v(4.64, -26.61) * mm});
            skLineSegment(sketch, "E51.14.10", {"start": v(3.78, -25.53) * mm, "end": v(4.23, -26.06) * mm});
            skLineSegment(sketch, "E51.14.11", {"start": v(5.64, -23.6) * mm, "end": v(5.53, -24.12) * mm});
            skLineSegment(sketch, "E51.14.12", {"start": v(5.18, -25.28) * mm, "end": v(4.94, -25.93) * mm});
            skLineSegment(sketch, "E51.14.13", {"start": v(2.1, -22.72) * mm, "end": v(2.21, -23) * mm});
            skLineSegment(sketch, "E51.14.14", {"start": v(2.21, -23) * mm, "end": v(2.35, -23.33) * mm});
            skLineSegment(sketch, "E51.14.15", {"start": v(2.35, -23.33) * mm, "end": v(2.54, -23.7) * mm});
            skLineSegment(sketch, "E51.14.16", {"start": v(5.77, -22.73) * mm, "end": v(5.72, -23.14) * mm});
            skLineSegment(sketch, "E51.14.17", {"start": v(5.79, -22.37) * mm, "end": v(5.77, -22.73) * mm});
            skLineSegment(sketch, "E51.14.18", {"start": v(5.72, -23.14) * mm, "end": v(5.64, -23.6) * mm});
            skLineSegment(sketch, "E51.14.19", {"start": v(2.03, -22.48) * mm, "end": v(2.1, -22.72) * mm});
            skLineSegment(sketch, "E51.14.20", {"start": v(1.98, -22.3) * mm, "end": v(2.03, -22.48) * mm});
            skLineSegment(sketch, "E51.14.21", {"start": v(5.8, -22.07) * mm, "end": v(5.79, -22.37) * mm});
            skLineSegment(sketch, "E51.14.22", {"start": v(5.78, -21.82) * mm, "end": v(5.8, -22.07) * mm});
            skLineSegment(sketch, "E51.14.23", {"start": v(5.75, -21.49) * mm, "end": v(5.77, -21.62) * mm});
            skLineSegment(sketch, "E51.14.24", {"start": v(1.93, -22.05) * mm, "end": v(1.93, -22.08) * mm});
            skLineSegment(sketch, "E51.14.25", {"start": v(1.93, -22.08) * mm, "end": v(1.95, -22.16) * mm});
            skLineSegment(sketch, "E51.14.26", {"start": v(5.77, -21.62) * mm, "end": v(5.78, -21.82) * mm});
            skLineSegment(sketch, "E51.14.27", {"start": v(1.95, -22.16) * mm, "end": v(1.98, -22.3) * mm});
            skLineSegment(sketch, "E51.14.28", {"start": v(5.73, -21.4) * mm, "end": v(5.75, -21.49) * mm});
            skLineSegment(sketch, "E51.14.29", {"start": v(5.73, -21.38) * mm, "end": v(5.73, -21.4) * mm});
            skLineSegment(sketch, "E51.15.0", {"start": v(7.62, -18.4) * mm, "end": v(8.47, -20.45) * mm});
            skLineSegment(sketch, "E51.15.1", {"start": v(6.62, -24.37) * mm, "end": v(7.08, -24.82) * mm});
            skLineSegment(sketch, "E51.15.2", {"start": v(4.31, -19.45) * mm, "end": v(4.8, -21.6) * mm});
            skLineSegment(sketch, "E51.15.3", {"start": v(6.23, -23.95) * mm, "end": v(6.62, -24.37) * mm});
            skLineSegment(sketch, "E51.15.4", {"start": v(8.63, -23.19) * mm, "end": v(8.56, -23.77) * mm});
            skLineSegment(sketch, "E51.15.5", {"start": v(8.56, -23.77) * mm, "end": v(8.44, -24.4) * mm});
            skLineSegment(sketch, "E51.15.6", {"start": v(5.9, -23.54) * mm, "end": v(6.23, -23.95) * mm});
            skLineSegment(sketch, "E51.15.7", {"start": v(7.6, -25.28) * mm, "end": v(8.18, -25.75) * mm});
            skLineSegment(sketch, "E51.15.8", {"start": v(5.61, -23.17) * mm, "end": v(5.9, -23.54) * mm});
            skLineSegment(sketch, "E51.15.9", {"start": v(8.28, -25.06) * mm, "end": v(8.07, -25.78) * mm});
            skLineSegment(sketch, "E51.15.10", {"start": v(7.08, -24.82) * mm, "end": v(7.6, -25.28) * mm});
            skLineSegment(sketch, "E51.15.11", {"start": v(8.68, -22.67) * mm, "end": v(8.63, -23.19) * mm});
            skLineSegment(sketch, "E51.15.12", {"start": v(8.44, -24.4) * mm, "end": v(8.28, -25.06) * mm});
            skLineSegment(sketch, "E51.15.13", {"start": v(5.05, -22.25) * mm, "end": v(5.2, -22.52) * mm});
            skLineSegment(sketch, "E51.15.14", {"start": v(5.2, -22.52) * mm, "end": v(5.38, -22.82) * mm});
            skLineSegment(sketch, "E51.15.15", {"start": v(5.38, -22.82) * mm, "end": v(5.61, -23.17) * mm});
            skLineSegment(sketch, "E51.15.16", {"start": v(8.68, -21.78) * mm, "end": v(8.7, -22.2) * mm});
            skLineSegment(sketch, "E51.15.17", {"start": v(8.66, -21.42) * mm, "end": v(8.68, -21.78) * mm});
            skLineSegment(sketch, "E51.15.18", {"start": v(8.7, -22.2) * mm, "end": v(8.68, -22.67) * mm});
            skLineSegment(sketch, "E51.15.19", {"start": v(4.94, -22.02) * mm, "end": v(5.05, -22.25) * mm});
            skLineSegment(sketch, "E51.15.20", {"start": v(4.87, -21.84) * mm, "end": v(4.94, -22.02) * mm});
            skLineSegment(sketch, "E51.15.21", {"start": v(8.62, -21.12) * mm, "end": v(8.66, -21.42) * mm});
            skLineSegment(sketch, "E51.15.22", {"start": v(8.58, -20.87) * mm, "end": v(8.62, -21.12) * mm});
            skLineSegment(sketch, "E51.15.23", {"start": v(8.5, -20.55) * mm, "end": v(8.54, -20.69) * mm});
            skLineSegment(sketch, "E51.15.24", {"start": v(4.8, -21.6) * mm, "end": v(4.8, -21.63) * mm});
            skLineSegment(sketch, "E51.15.25", {"start": v(4.8, -21.63) * mm, "end": v(4.82, -21.71) * mm});
            skLineSegment(sketch, "E51.15.26", {"start": v(8.54, -20.69) * mm, "end": v(8.58, -20.87) * mm});
            skLineSegment(sketch, "E51.15.27", {"start": v(4.82, -21.71) * mm, "end": v(4.87, -21.84) * mm});
            skLineSegment(sketch, "E51.15.28", {"start": v(8.48, -20.47) * mm, "end": v(8.5, -20.55) * mm});
            skLineSegment(sketch, "E51.15.29", {"start": v(8.47, -20.45) * mm, "end": v(8.48, -20.47) * mm});
            skLineSegment(sketch, "E51.16.0", {"start": v(9.96, -17.25) * mm, "end": v(11.07, -19.17) * mm});
            skLineSegment(sketch, "E51.16.1", {"start": v(9.75, -23.3) * mm, "end": v(10.26, -23.68) * mm});
            skLineSegment(sketch, "E51.16.2", {"start": v(6.81, -18.72) * mm, "end": v(7.57, -20.8) * mm});
            skLineSegment(sketch, "E51.16.3", {"start": v(9.3, -22.93) * mm, "end": v(9.75, -23.3) * mm});
            skLineSegment(sketch, "E51.16.4", {"start": v(11.59, -21.86) * mm, "end": v(11.58, -22.45) * mm});
            skLineSegment(sketch, "E51.16.5", {"start": v(11.58, -22.45) * mm, "end": v(11.55, -23.08) * mm});
            skLineSegment(sketch, "E51.16.6", {"start": v(8.92, -22.57) * mm, "end": v(9.3, -22.93) * mm});
            skLineSegment(sketch, "E51.16.7", {"start": v(10.83, -24.07) * mm, "end": v(11.47, -24.46) * mm});
            skLineSegment(sketch, "E51.16.8", {"start": v(8.59, -22.24) * mm, "end": v(8.92, -22.57) * mm});
            skLineSegment(sketch, "E51.16.9", {"start": v(11.48, -23.77) * mm, "end": v(11.37, -24.5) * mm});
            skLineSegment(sketch, "E51.16.10", {"start": v(10.26, -23.68) * mm, "end": v(10.83, -24.07) * mm});
            skLineSegment(sketch, "E51.16.11", {"start": v(11.56, -21.34) * mm, "end": v(11.59, -21.86) * mm});
            skLineSegment(sketch, "E51.16.12", {"start": v(11.55, -23.08) * mm, "end": v(11.48, -23.77) * mm});
            skLineSegment(sketch, "E51.16.13", {"start": v(7.91, -21.4) * mm, "end": v(8.09, -21.64) * mm});
            skLineSegment(sketch, "E51.16.14", {"start": v(8.09, -21.64) * mm, "end": v(8.31, -21.93) * mm});
            skLineSegment(sketch, "E51.16.15", {"start": v(8.31, -21.93) * mm, "end": v(8.59, -22.24) * mm});
            skLineSegment(sketch, "E51.16.16", {"start": v(11.45, -20.46) * mm, "end": v(11.51, -20.87) * mm});
            skLineSegment(sketch, "E51.16.17", {"start": v(11.38, -20.1) * mm, "end": v(11.45, -20.46) * mm});
            skLineSegment(sketch, "E51.16.18", {"start": v(11.51, -20.87) * mm, "end": v(11.56, -21.34) * mm});
            skLineSegment(sketch, "E51.16.19", {"start": v(7.77, -21.19) * mm, "end": v(7.91, -21.4) * mm});
            skLineSegment(sketch, "E51.16.20", {"start": v(7.68, -21.02) * mm, "end": v(7.77, -21.19) * mm});
            skLineSegment(sketch, "E51.16.21", {"start": v(11.3, -19.81) * mm, "end": v(11.38, -20.1) * mm});
            skLineSegment(sketch, "E51.16.22", {"start": v(11.23, -19.58) * mm, "end": v(11.3, -19.81) * mm});
            skLineSegment(sketch, "E51.16.23", {"start": v(11.11, -19.27) * mm, "end": v(11.17, -19.4) * mm});
            skLineSegment(sketch, "E51.16.24", {"start": v(7.57, -20.8) * mm, "end": v(7.58, -20.82) * mm});
            skLineSegment(sketch, "E51.16.25", {"start": v(7.58, -20.82) * mm, "end": v(7.61, -20.9) * mm});
            skLineSegment(sketch, "E51.16.26", {"start": v(11.17, -19.4) * mm, "end": v(11.23, -19.58) * mm});
            skLineSegment(sketch, "E51.16.27", {"start": v(7.61, -20.9) * mm, "end": v(7.68, -21.02) * mm});
            skLineSegment(sketch, "E51.16.28", {"start": v(11.08, -19.2) * mm, "end": v(11.11, -19.27) * mm});
            skLineSegment(sketch, "E51.16.29", {"start": v(11.07, -19.17) * mm, "end": v(11.08, -19.2) * mm});
            skLineSegment(sketch, "E51.17.0", {"start": v(12.13, -15.8) * mm, "end": v(13.47, -17.56) * mm});
            skLineSegment(sketch, "E51.17.1", {"start": v(12.7, -21.83) * mm, "end": v(13.26, -22.14) * mm});
            skLineSegment(sketch, "E51.17.2", {"start": v(9.2, -17.67) * mm, "end": v(10.22, -19.63) * mm});
            skLineSegment(sketch, "E51.17.3", {"start": v(12.22, -21.52) * mm, "end": v(12.7, -21.83) * mm});
            skLineSegment(sketch, "E51.17.4", {"start": v(14.34, -20.17) * mm, "end": v(14.41, -20.74) * mm});
            skLineSegment(sketch, "E51.17.5", {"start": v(14.41, -20.74) * mm, "end": v(14.46, -21.38) * mm});
            skLineSegment(sketch, "E51.17.6", {"start": v(11.79, -21.22) * mm, "end": v(12.22, -21.52) * mm});
            skLineSegment(sketch, "E51.17.7", {"start": v(13.88, -22.45) * mm, "end": v(14.56, -22.76) * mm});
            skLineSegment(sketch, "E51.17.8", {"start": v(11.42, -20.92) * mm, "end": v(11.79, -21.22) * mm});
            skLineSegment(sketch, "E51.17.9", {"start": v(14.49, -22.07) * mm, "end": v(14.47, -22.81) * mm});
            skLineSegment(sketch, "E51.17.10", {"start": v(13.26, -22.14) * mm, "end": v(13.88, -22.45) * mm});
            skLineSegment(sketch, "E51.17.11", {"start": v(14.25, -19.65) * mm, "end": v(14.34, -20.17) * mm});
            skLineSegment(sketch, "E51.17.12", {"start": v(14.46, -21.38) * mm, "end": v(14.49, -22.07) * mm});
            skLineSegment(sketch, "E51.17.13", {"start": v(10.64, -20.18) * mm, "end": v(10.84, -20.4) * mm});
            skLineSegment(sketch, "E51.17.14", {"start": v(10.84, -20.4) * mm, "end": v(11.1, -20.65) * mm});
            skLineSegment(sketch, "E51.17.15", {"start": v(11.1, -20.65) * mm, "end": v(11.42, -20.92) * mm});
            skLineSegment(sketch, "E51.17.16", {"start": v(14.03, -18.8) * mm, "end": v(14.14, -19.2) * mm});
            skLineSegment(sketch, "E51.17.17", {"start": v(13.9, -18.45) * mm, "end": v(14.03, -18.8) * mm});
            skLineSegment(sketch, "E51.17.18", {"start": v(14.14, -19.2) * mm, "end": v(14.25, -19.65) * mm});
            skLineSegment(sketch, "E51.17.19", {"start": v(10.47, -20) * mm, "end": v(10.64, -20.18) * mm});
            skLineSegment(sketch, "E51.17.20", {"start": v(10.36, -19.84) * mm, "end": v(10.47, -20) * mm});
            skLineSegment(sketch, "E51.17.21", {"start": v(13.8, -18.17) * mm, "end": v(13.9, -18.45) * mm});
            skLineSegment(sketch, "E51.17.22", {"start": v(13.7, -17.94) * mm, "end": v(13.8, -18.17) * mm});
            skLineSegment(sketch, "E51.17.23", {"start": v(13.53, -17.65) * mm, "end": v(13.6, -17.77) * mm});
            skLineSegment(sketch, "E51.17.24", {"start": v(10.22, -19.63) * mm, "end": v(10.23, -19.66) * mm});
            skLineSegment(sketch, "E51.17.25", {"start": v(10.23, -19.66) * mm, "end": v(10.28, -19.73) * mm});
            skLineSegment(sketch, "E51.17.26", {"start": v(13.6, -17.77) * mm, "end": v(13.7, -17.94) * mm});
            skLineSegment(sketch, "E51.17.27", {"start": v(10.28, -19.73) * mm, "end": v(10.36, -19.84) * mm});
            skLineSegment(sketch, "E51.17.28", {"start": v(13.49, -17.58) * mm, "end": v(13.53, -17.65) * mm});
            skLineSegment(sketch, "E51.17.29", {"start": v(13.47, -17.56) * mm, "end": v(13.49, -17.58) * mm});
            skLineSegment(sketch, "E52.2.18.0", {"start": v(14.09, -14.09) * mm, "end": v(15.65, -15.65) * mm});
            skLineSegment(sketch, "E52.3.18.0", {"start": v(15.45, -19.98) * mm, "end": v(16.04, -20.22) * mm});
            skLineSegment(sketch, "E52.6.18.0", {"start": v(11.43, -16.32) * mm, "end": v(12.7, -18.13) * mm});
            skLineSegment(sketch, "E52.9.18.0", {"start": v(14.92, -19.74) * mm, "end": v(15.45, -19.98) * mm});
            skLineSegment(sketch, "E52.12.18.0", {"start": v(16.85, -18.12) * mm, "end": v(17, -18.68) * mm});
            skLineSegment(sketch, "E52.15.18.0", {"start": v(17, -18.68) * mm, "end": v(17.13, -19.3) * mm});
            skLineSegment(sketch, "E52.18.18.0", {"start": v(14.45, -19.5) * mm, "end": v(14.92, -19.74) * mm});
            skLineSegment(sketch, "E52.21.18.0", {"start": v(16.69, -20.45) * mm, "end": v(17.4, -20.66) * mm});
            skLineSegment(sketch, "E52.24.18.0", {"start": v(14.05, -19.26) * mm, "end": v(14.45, -19.5) * mm});
            skLineSegment(sketch, "E52.27.18.0", {"start": v(17.24, -19.99) * mm, "end": v(17.32, -20.73) * mm});
            skLineSegment(sketch, "E52.30.18.0", {"start": v(16.04, -20.22) * mm, "end": v(16.69, -20.45) * mm});
            skLineSegment(sketch, "E52.33.18.0", {"start": v(16.69, -17.62) * mm, "end": v(16.85, -18.12) * mm});
            skLineSegment(sketch, "E52.36.18.0", {"start": v(17.13, -19.3) * mm, "end": v(17.24, -19.99) * mm});
            skLineSegment(sketch, "E52.39.18.0", {"start": v(13.18, -18.62) * mm, "end": v(13.41, -18.81) * mm});
            skLineSegment(sketch, "E52.42.18.0", {"start": v(13.41, -18.81) * mm, "end": v(13.7, -19.03) * mm});
            skLineSegment(sketch, "E52.45.18.0", {"start": v(13.7, -19.03) * mm, "end": v(14.05, -19.26) * mm});
            skLineSegment(sketch, "E52.48.18.0", {"start": v(16.36, -16.8) * mm, "end": v(16.52, -17.18) * mm});
            skLineSegment(sketch, "E52.51.18.0", {"start": v(16.2, -16.48) * mm, "end": v(16.36, -16.8) * mm});
            skLineSegment(sketch, "E52.54.18.0", {"start": v(16.52, -17.18) * mm, "end": v(16.69, -17.62) * mm});
            skLineSegment(sketch, "E52.57.18.0", {"start": v(13, -18.45) * mm, "end": v(13.18, -18.62) * mm});
            skLineSegment(sketch, "E52.60.18.0", {"start": v(12.86, -18.32) * mm, "end": v(13, -18.45) * mm});
            skLineSegment(sketch, "E52.63.18.0", {"start": v(16.05, -16.21) * mm, "end": v(16.2, -16.48) * mm});
            skLineSegment(sketch, "E52.66.18.0", {"start": v(15.92, -16) * mm, "end": v(16.05, -16.21) * mm});
            skLineSegment(sketch, "E52.69.18.0", {"start": v(15.72, -15.73) * mm, "end": v(15.8, -15.84) * mm});
            skLineSegment(sketch, "E52.72.18.0", {"start": v(12.7, -18.13) * mm, "end": v(12.71, -18.15) * mm});
            skLineSegment(sketch, "E52.75.18.0", {"start": v(12.71, -18.15) * mm, "end": v(12.76, -18.22) * mm});
            skLineSegment(sketch, "E52.78.18.0", {"start": v(15.8, -15.84) * mm, "end": v(15.92, -16) * mm});
            skLineSegment(sketch, "E52.81.18.0", {"start": v(12.76, -18.22) * mm, "end": v(12.86, -18.32) * mm});
            skLineSegment(sketch, "E52.84.18.0", {"start": v(15.67, -15.67) * mm, "end": v(15.72, -15.73) * mm});
            skLineSegment(sketch, "E52.87.18.0", {"start": v(15.65, -15.65) * mm, "end": v(15.67, -15.67) * mm});
            skLineSegment(sketch, "E52.2.19.0", {"start": v(15.8, -12.13) * mm, "end": v(17.56, -13.47) * mm});
            skLineSegment(sketch, "E52.3.19.0", {"start": v(17.92, -17.8) * mm, "end": v(18.54, -17.96) * mm});
            skLineSegment(sketch, "E52.6.19.0", {"start": v(13.46, -14.69) * mm, "end": v(14.95, -16.32) * mm});
            skLineSegment(sketch, "E52.9.19.0", {"start": v(17.37, -17.62) * mm, "end": v(17.92, -17.8) * mm});
            skLineSegment(sketch, "E52.12.19.0", {"start": v(19.07, -15.77) * mm, "end": v(19.3, -16.3) * mm});
            skLineSegment(sketch, "E52.15.19.0", {"start": v(19.3, -16.3) * mm, "end": v(19.5, -16.9) * mm});
            skLineSegment(sketch, "E52.18.19.0", {"start": v(16.88, -17.44) * mm, "end": v(17.37, -17.62) * mm});
            skLineSegment(sketch, "E52.21.19.0", {"start": v(19.22, -18.1) * mm, "end": v(19.95, -18.21) * mm});
            skLineSegment(sketch, "E52.24.19.0", {"start": v(16.44, -17.26) * mm, "end": v(16.88, -17.44) * mm});
            skLineSegment(sketch, "E52.27.19.0", {"start": v(19.7, -17.57) * mm, "end": v(19.88, -18.3) * mm});
            skLineSegment(sketch, "E52.30.19.0", {"start": v(18.54, -17.96) * mm, "end": v(19.22, -18.1) * mm});
            skLineSegment(sketch, "E52.33.19.0", {"start": v(18.85, -15.3) * mm, "end": v(19.07, -15.77) * mm});
            skLineSegment(sketch, "E52.36.19.0", {"start": v(19.5, -16.9) * mm, "end": v(19.7, -17.57) * mm});
            skLineSegment(sketch, "E52.39.19.0", {"start": v(15.5, -16.74) * mm, "end": v(15.76, -16.9) * mm});
            skLineSegment(sketch, "E52.42.19.0", {"start": v(15.76, -16.9) * mm, "end": v(16.07, -17.08) * mm});
            skLineSegment(sketch, "E52.45.19.0", {"start": v(16.07, -17.08) * mm, "end": v(16.44, -17.26) * mm});
            skLineSegment(sketch, "E52.48.19.0", {"start": v(18.41, -14.52) * mm, "end": v(18.62, -14.88) * mm});
            skLineSegment(sketch, "E52.51.19.0", {"start": v(18.21, -14.22) * mm, "end": v(18.41, -14.52) * mm});
            skLineSegment(sketch, "E52.54.19.0", {"start": v(18.62, -14.88) * mm, "end": v(18.85, -15.3) * mm});
            skLineSegment(sketch, "E52.57.19.0", {"start": v(15.3, -16.6) * mm, "end": v(15.5, -16.74) * mm});
            skLineSegment(sketch, "E52.60.19.0", {"start": v(15.14, -16.48) * mm, "end": v(15.3, -16.6) * mm});
            skLineSegment(sketch, "E52.63.19.0", {"start": v(18.03, -13.98) * mm, "end": v(18.21, -14.22) * mm});
            skLineSegment(sketch, "E52.66.19.0", {"start": v(17.87, -13.79) * mm, "end": v(18.03, -13.98) * mm});
            skLineSegment(sketch, "E52.69.19.0", {"start": v(17.64, -13.55) * mm, "end": v(17.74, -13.64) * mm});
            skLineSegment(sketch, "E52.72.19.0", {"start": v(14.95, -16.32) * mm, "end": v(14.97, -16.34) * mm});
            skLineSegment(sketch, "E52.75.19.0", {"start": v(14.97, -16.34) * mm, "end": v(15.03, -16.4) * mm});
            skLineSegment(sketch, "E52.78.19.0", {"start": v(17.74, -13.64) * mm, "end": v(17.87, -13.79) * mm});
            skLineSegment(sketch, "E52.81.19.0", {"start": v(15.03, -16.4) * mm, "end": v(15.14, -16.48) * mm});
            skLineSegment(sketch, "E52.84.19.0", {"start": v(17.58, -13.5) * mm, "end": v(17.64, -13.55) * mm});
            skLineSegment(sketch, "E52.87.19.0", {"start": v(17.56, -13.47) * mm, "end": v(17.58, -13.5) * mm});
            skLineSegment(sketch, "E52.2.20.0", {"start": v(17.25, -9.96) * mm, "end": v(19.17, -11.07) * mm});
            skLineSegment(sketch, "E52.3.20.0", {"start": v(20.1, -15.3) * mm, "end": v(20.72, -15.38) * mm});
            skLineSegment(sketch, "E52.6.20.0", {"start": v(15.26, -12.8) * mm, "end": v(16.95, -14.23) * mm});
            skLineSegment(sketch, "E52.9.20.0", {"start": v(19.52, -15.2) * mm, "end": v(20.1, -15.3) * mm});
            skLineSegment(sketch, "E52.12.20.0", {"start": v(20.97, -13.14) * mm, "end": v(21.25, -13.65) * mm});
            skLineSegment(sketch, "E52.15.20.0", {"start": v(21.25, -13.65) * mm, "end": v(21.54, -14.21) * mm});
            skLineSegment(sketch, "E52.18.20.0", {"start": v(19, -15.09) * mm, "end": v(19.52, -15.2) * mm});
            skLineSegment(sketch, "E52.21.20.0", {"start": v(21.41, -15.43) * mm, "end": v(22.16, -15.45) * mm});
            skLineSegment(sketch, "E52.24.20.0", {"start": v(18.56, -14.96) * mm, "end": v(19, -15.09) * mm});
            skLineSegment(sketch, "E52.27.20.0", {"start": v(21.83, -14.84) * mm, "end": v(22.1, -15.54) * mm});
            skLineSegment(sketch, "E52.30.20.0", {"start": v(20.72, -15.38) * mm, "end": v(21.41, -15.43) * mm});
            skLineSegment(sketch, "E52.33.20.0", {"start": v(20.68, -12.7) * mm, "end": v(20.97, -13.14) * mm});
            skLineSegment(sketch, "E52.36.20.0", {"start": v(21.54, -14.21) * mm, "end": v(21.83, -14.84) * mm});
            skLineSegment(sketch, "E52.39.20.0", {"start": v(17.55, -14.58) * mm, "end": v(17.83, -14.7) * mm});
            skLineSegment(sketch, "E52.42.20.0", {"start": v(17.83, -14.7) * mm, "end": v(18.16, -14.83) * mm});
            skLineSegment(sketch, "E52.45.20.0", {"start": v(18.16, -14.83) * mm, "end": v(18.56, -14.96) * mm});
            skLineSegment(sketch, "E52.48.20.0", {"start": v(20.15, -12) * mm, "end": v(20.4, -12.32) * mm});
            skLineSegment(sketch, "E52.51.20.0", {"start": v(19.91, -11.72) * mm, "end": v(20.15, -12) * mm});
            skLineSegment(sketch, "E52.54.20.0", {"start": v(20.4, -12.32) * mm, "end": v(20.68, -12.7) * mm});
            skLineSegment(sketch, "E52.57.20.0", {"start": v(17.33, -14.46) * mm, "end": v(17.55, -14.58) * mm});
            skLineSegment(sketch, "E52.60.20.0", {"start": v(17.16, -14.37) * mm, "end": v(17.33, -14.46) * mm});
            skLineSegment(sketch, "E52.63.20.0", {"start": v(19.7, -11.5) * mm, "end": v(19.91, -11.72) * mm});
            skLineSegment(sketch, "E52.66.20.0", {"start": v(19.52, -11.34) * mm, "end": v(19.7, -11.5) * mm});
            skLineSegment(sketch, "E52.69.20.0", {"start": v(19.26, -11.13) * mm, "end": v(19.37, -11.21) * mm});
            skLineSegment(sketch, "E52.72.20.0", {"start": v(16.95, -14.23) * mm, "end": v(16.98, -14.24) * mm});
            skLineSegment(sketch, "E52.75.20.0", {"start": v(16.98, -14.24) * mm, "end": v(17.04, -14.3) * mm});
            skLineSegment(sketch, "E52.78.20.0", {"start": v(19.37, -11.21) * mm, "end": v(19.52, -11.34) * mm});
            skLineSegment(sketch, "E52.81.20.0", {"start": v(17.04, -14.3) * mm, "end": v(17.16, -14.37) * mm});
            skLineSegment(sketch, "E52.84.20.0", {"start": v(19.2, -11.08) * mm, "end": v(19.26, -11.13) * mm});
            skLineSegment(sketch, "E52.87.20.0", {"start": v(19.17, -11.07) * mm, "end": v(19.2, -11.08) * mm});
            skLineSegment(sketch, "E52.2.21.0", {"start": v(18.4, -7.62) * mm, "end": v(20.45, -8.47) * mm});
            skLineSegment(sketch, "E52.3.21.0", {"start": v(21.92, -12.55) * mm, "end": v(22.56, -12.55) * mm});
            skLineSegment(sketch, "E52.6.21.0", {"start": v(16.8, -10.7) * mm, "end": v(18.67, -11.9) * mm});
            skLineSegment(sketch, "E52.9.21.0", {"start": v(21.34, -12.53) * mm, "end": v(21.92, -12.55) * mm});
            skLineSegment(sketch, "E52.12.21.0", {"start": v(22.5, -10.3) * mm, "end": v(22.85, -10.76) * mm});
            skLineSegment(sketch, "E52.15.21.0", {"start": v(22.85, -10.76) * mm, "end": v(23.21, -11.28) * mm});
            skLineSegment(sketch, "E52.18.21.0", {"start": v(20.82, -12.48) * mm, "end": v(21.34, -12.53) * mm});
            skLineSegment(sketch, "E52.21.21.0", {"start": v(23.25, -12.5) * mm, "end": v(23.99, -12.43) * mm});
            skLineSegment(sketch, "E52.24.21.0", {"start": v(20.35, -12.41) * mm, "end": v(20.82, -12.48) * mm});
            skLineSegment(sketch, "E52.27.21.0", {"start": v(23.58, -11.87) * mm, "end": v(23.94, -12.52) * mm});
            skLineSegment(sketch, "E52.30.21.0", {"start": v(22.56, -12.55) * mm, "end": v(23.25, -12.5) * mm});
            skLineSegment(sketch, "E52.33.21.0", {"start": v(22.16, -9.9) * mm, "end": v(22.5, -10.3) * mm});
            skLineSegment(sketch, "E52.36.21.0", {"start": v(23.21, -11.28) * mm, "end": v(23.58, -11.87) * mm});
            skLineSegment(sketch, "E52.39.21.0", {"start": v(19.3, -12.16) * mm, "end": v(19.6, -12.25) * mm});
            skLineSegment(sketch, "E52.42.21.0", {"start": v(19.6, -12.25) * mm, "end": v(19.94, -12.33) * mm});
            skLineSegment(sketch, "E52.45.21.0", {"start": v(19.94, -12.33) * mm, "end": v(20.35, -12.41) * mm});
            skLineSegment(sketch, "E52.48.21.0", {"start": v(21.54, -9.26) * mm, "end": v(21.84, -9.55) * mm});
            skLineSegment(sketch, "E52.51.21.0", {"start": v(21.27, -9.02) * mm, "end": v(21.54, -9.26) * mm});
            skLineSegment(sketch, "E52.54.21.0", {"start": v(21.84, -9.55) * mm, "end": v(22.16, -9.9) * mm});
            skLineSegment(sketch, "E52.57.21.0", {"start": v(19.07, -12.08) * mm, "end": v(19.3, -12.16) * mm});
            skLineSegment(sketch, "E52.60.21.0", {"start": v(18.89, -12) * mm, "end": v(19.07, -12.08) * mm});
            skLineSegment(sketch, "E52.63.21.0", {"start": v(21.03, -8.84) * mm, "end": v(21.27, -9.02) * mm});
            skLineSegment(sketch, "E52.66.21.0", {"start": v(20.83, -8.7) * mm, "end": v(21.03, -8.84) * mm});
            skLineSegment(sketch, "E52.69.21.0", {"start": v(20.55, -8.52) * mm, "end": v(20.67, -8.59) * mm});
            skLineSegment(sketch, "E52.72.21.0", {"start": v(18.67, -11.9) * mm, "end": v(18.69, -11.9) * mm});
            skLineSegment(sketch, "E52.75.21.0", {"start": v(18.69, -11.9) * mm, "end": v(18.76, -11.94) * mm});
            skLineSegment(sketch, "E52.78.21.0", {"start": v(20.67, -8.59) * mm, "end": v(20.83, -8.7) * mm});
            skLineSegment(sketch, "E52.81.21.0", {"start": v(18.76, -11.94) * mm, "end": v(18.89, -12) * mm});
            skLineSegment(sketch, "E52.84.21.0", {"start": v(20.47, -8.48) * mm, "end": v(20.55, -8.52) * mm});
            skLineSegment(sketch, "E52.87.21.0", {"start": v(20.45, -8.47) * mm, "end": v(20.47, -8.48) * mm});
            skLineSegment(sketch, "E52.2.22.0", {"start": v(19.24, -5.16) * mm, "end": v(21.38, -5.73) * mm});
            skLineSegment(sketch, "E52.3.22.0", {"start": v(23.37, -9.58) * mm, "end": v(24, -9.5) * mm});
            skLineSegment(sketch, "E52.6.22.0", {"start": v(18.05, -8.42) * mm, "end": v(20.06, -9.35) * mm});
            skLineSegment(sketch, "E52.9.22.0", {"start": v(22.8, -9.64) * mm, "end": v(23.37, -9.58) * mm});
            skLineSegment(sketch, "E52.12.22.0", {"start": v(23.65, -7.27) * mm, "end": v(24.06, -7.68) * mm});
            skLineSegment(sketch, "E52.15.22.0", {"start": v(24.06, -7.68) * mm, "end": v(24.49, -8.15) * mm});
            skLineSegment(sketch, "E52.18.22.0", {"start": v(22.27, -9.66) * mm, "end": v(22.8, -9.64) * mm});
            skLineSegment(sketch, "E52.21.22.0", {"start": v(24.68, -9.37) * mm, "end": v(25.4, -9.19) * mm});
            skLineSegment(sketch, "E52.24.22.0", {"start": v(21.8, -9.65) * mm, "end": v(22.27, -9.66) * mm});
            skLineSegment(sketch, "E52.27.22.0", {"start": v(24.93, -8.69) * mm, "end": v(25.37, -9.3) * mm});
            skLineSegment(sketch, "E52.30.22.0", {"start": v(24, -9.5) * mm, "end": v(24.68, -9.37) * mm});
            skLineSegment(sketch, "E52.33.22.0", {"start": v(23.26, -6.92) * mm, "end": v(23.65, -7.27) * mm});
            skLineSegment(sketch, "E52.36.22.0", {"start": v(24.49, -8.15) * mm, "end": v(24.93, -8.69) * mm});
            skLineSegment(sketch, "E52.39.22.0", {"start": v(20.72, -9.54) * mm, "end": v(21.02, -9.59) * mm});
            skLineSegment(sketch, "E52.42.22.0", {"start": v(21.02, -9.59) * mm, "end": v(21.38, -9.63) * mm});
            skLineSegment(sketch, "E52.45.22.0", {"start": v(21.38, -9.63) * mm, "end": v(21.8, -9.65) * mm});
            skLineSegment(sketch, "E52.48.22.0", {"start": v(22.57, -6.37) * mm, "end": v(22.9, -6.62) * mm});
            skLineSegment(sketch, "E52.51.22.0", {"start": v(22.27, -6.17) * mm, "end": v(22.57, -6.37) * mm});
            skLineSegment(sketch, "E52.54.22.0", {"start": v(22.9, -6.62) * mm, "end": v(23.26, -6.92) * mm});
            skLineSegment(sketch, "E52.57.22.0", {"start": v(20.48, -9.49) * mm, "end": v(20.72, -9.54) * mm});
            skLineSegment(sketch, "E52.60.22.0", {"start": v(20.3, -9.44) * mm, "end": v(20.48, -9.49) * mm});
            skLineSegment(sketch, "E52.63.22.0", {"start": v(22, -6.02) * mm, "end": v(22.27, -6.17) * mm});
            skLineSegment(sketch, "E52.66.22.0", {"start": v(21.79, -5.9) * mm, "end": v(22, -6.02) * mm});
            skLineSegment(sketch, "E52.69.22.0", {"start": v(21.48, -5.76) * mm, "end": v(21.61, -5.82) * mm});
            skLineSegment(sketch, "E52.72.22.0", {"start": v(20.06, -9.35) * mm, "end": v(20.08, -9.36) * mm});
            skLineSegment(sketch, "E52.75.22.0", {"start": v(20.08, -9.36) * mm, "end": v(20.16, -9.4) * mm});
            skLineSegment(sketch, "E52.78.22.0", {"start": v(21.61, -5.82) * mm, "end": v(21.79, -5.9) * mm});
            skLineSegment(sketch, "E52.81.22.0", {"start": v(20.16, -9.4) * mm, "end": v(20.3, -9.44) * mm});
            skLineSegment(sketch, "E52.84.22.0", {"start": v(21.4, -5.74) * mm, "end": v(21.48, -5.76) * mm});
            skLineSegment(sketch, "E52.87.22.0", {"start": v(21.38, -5.73) * mm, "end": v(21.4, -5.74) * mm});
            skLineSegment(sketch, "E52.2.23.0", {"start": v(19.75, -2.6) * mm, "end": v(21.94, -2.89) * mm});
            skLineSegment(sketch, "E52.3.23.0", {"start": v(24.42, -6.45) * mm, "end": v(25.03, -6.28) * mm});
            skLineSegment(sketch, "E52.6.23.0", {"start": v(19, -6) * mm, "end": v(21.1, -6.66) * mm});
            skLineSegment(sketch, "E52.9.23.0", {"start": v(23.85, -6.58) * mm, "end": v(24.42, -6.45) * mm});
            skLineSegment(sketch, "E52.12.23.0", {"start": v(24.4, -4.12) * mm, "end": v(24.86, -4.47) * mm});
            skLineSegment(sketch, "E52.15.23.0", {"start": v(24.86, -4.47) * mm, "end": v(25.34, -4.89) * mm});
            skLineSegment(sketch, "E52.18.23.0", {"start": v(23.34, -6.67) * mm, "end": v(23.85, -6.58) * mm});
            skLineSegment(sketch, "E52.21.23.0", {"start": v(25.7, -6.06) * mm, "end": v(26.39, -5.8) * mm});
            skLineSegment(sketch, "E52.24.23.0", {"start": v(22.87, -6.72) * mm, "end": v(23.34, -6.67) * mm});
            skLineSegment(sketch, "E52.27.23.0", {"start": v(25.85, -5.36) * mm, "end": v(26.36, -5.9) * mm});
            skLineSegment(sketch, "E52.30.23.0", {"start": v(25.03, -6.28) * mm, "end": v(25.7, -6.06) * mm});
            skLineSegment(sketch, "E52.33.23.0", {"start": v(23.97, -3.82) * mm, "end": v(24.4, -4.12) * mm});
            skLineSegment(sketch, "E52.36.23.0", {"start": v(25.34, -4.89) * mm, "end": v(25.85, -5.36) * mm});
            skLineSegment(sketch, "E52.39.23.0", {"start": v(21.8, -6.75) * mm, "end": v(22.1, -6.76) * mm});
            skLineSegment(sketch, "E52.42.23.0", {"start": v(22.1, -6.76) * mm, "end": v(22.45, -6.75) * mm});
            skLineSegment(sketch, "E52.45.23.0", {"start": v(22.45, -6.75) * mm, "end": v(22.87, -6.72) * mm});
            skLineSegment(sketch, "E52.48.23.0", {"start": v(23.2, -3.37) * mm, "end": v(23.57, -3.57) * mm});
            skLineSegment(sketch, "E52.51.23.0", {"start": v(22.88, -3.21) * mm, "end": v(23.2, -3.37) * mm});
            skLineSegment(sketch, "E52.54.23.0", {"start": v(23.57, -3.57) * mm, "end": v(23.97, -3.82) * mm});
            skLineSegment(sketch, "E52.57.23.0", {"start": v(21.54, -6.73) * mm, "end": v(21.8, -6.75) * mm});
            skLineSegment(sketch, "E52.60.23.0", {"start": v(21.35, -6.7) * mm, "end": v(21.54, -6.73) * mm});
            skLineSegment(sketch, "E52.63.23.0", {"start": v(22.6, -3.1) * mm, "end": v(22.88, -3.21) * mm});
            skLineSegment(sketch, "E52.66.23.0", {"start": v(22.37, -3) * mm, "end": v(22.6, -3.1) * mm});
            skLineSegment(sketch, "E52.69.23.0", {"start": v(22.05, -2.91) * mm, "end": v(22.18, -2.95) * mm});
            skLineSegment(sketch, "E52.72.23.0", {"start": v(21.1, -6.66) * mm, "end": v(21.13, -6.66) * mm});
            skLineSegment(sketch, "E52.75.23.0", {"start": v(21.13, -6.66) * mm, "end": v(21.22, -6.68) * mm});
            skLineSegment(sketch, "E52.78.23.0", {"start": v(22.18, -2.95) * mm, "end": v(22.37, -3) * mm});
            skLineSegment(sketch, "E52.81.23.0", {"start": v(21.22, -6.68) * mm, "end": v(21.35, -6.7) * mm});
            skLineSegment(sketch, "E52.84.23.0", {"start": v(21.97, -2.9) * mm, "end": v(22.05, -2.91) * mm});
            skLineSegment(sketch, "E52.87.23.0", {"start": v(21.94, -2.89) * mm, "end": v(21.97, -2.9) * mm});
            skLineSegment(sketch, "E52.2.24.0", {"start": v(19.92, 0) * mm, "end": v(22.13, 0) * mm});
            skLineSegment(sketch, "E52.3.24.0", {"start": v(25.05, -3.2) * mm, "end": v(25.64, -2.96) * mm});
            skLineSegment(sketch, "E52.6.24.0", {"start": v(19.62, -3.46) * mm, "end": v(21.8, -3.84) * mm});
            skLineSegment(sketch, "E52.9.24.0", {"start": v(24.5, -3.4) * mm, "end": v(25.05, -3.2) * mm});
            skLineSegment(sketch, "E52.12.24.0", {"start": v(24.73, -0.9) * mm, "end": v(25.23, -1.2) * mm});
            skLineSegment(sketch, "E52.15.24.0", {"start": v(25.23, -1.2) * mm, "end": v(25.76, -1.54) * mm});
            skLineSegment(sketch, "E52.18.24.0", {"start": v(24, -3.56) * mm, "end": v(24.5, -3.4) * mm});
            skLineSegment(sketch, "E52.21.24.0", {"start": v(26.26, -2.66) * mm, "end": v(26.92, -2.3) * mm});
            skLineSegment(sketch, "E52.24.24.0", {"start": v(23.55, -3.68) * mm, "end": v(24, -3.56) * mm});
            skLineSegment(sketch, "E52.27.24.0", {"start": v(26.32, -1.94) * mm, "end": v(26.9, -2.4) * mm});
            skLineSegment(sketch, "E52.30.24.0", {"start": v(25.64, -2.96) * mm, "end": v(26.26, -2.66) * mm});
            skLineSegment(sketch, "E52.33.24.0", {"start": v(24.26, -0.66) * mm, "end": v(24.73, -0.9) * mm});
            skLineSegment(sketch, "E52.36.24.0", {"start": v(25.76, -1.54) * mm, "end": v(26.32, -1.94) * mm});
            skLineSegment(sketch, "E52.39.24.0", {"start": v(22.49, -3.85) * mm, "end": v(22.79, -3.82) * mm});
            skLineSegment(sketch, "E52.42.24.0", {"start": v(22.79, -3.82) * mm, "end": v(23.14, -3.76) * mm});
            skLineSegment(sketch, "E52.45.24.0", {"start": v(23.14, -3.76) * mm, "end": v(23.55, -3.68) * mm});
            skLineSegment(sketch, "E52.48.24.0", {"start": v(23.45, -0.31) * mm, "end": v(23.83, -0.46) * mm});
            skLineSegment(sketch, "E52.51.24.0", {"start": v(23.1, -0.2) * mm, "end": v(23.45, -0.31) * mm});
            skLineSegment(sketch, "E52.54.24.0", {"start": v(23.83, -0.46) * mm, "end": v(24.26, -0.66) * mm});
            skLineSegment(sketch, "E52.57.24.0", {"start": v(22.24, -3.86) * mm, "end": v(22.49, -3.85) * mm});
            skLineSegment(sketch, "E52.60.24.0", {"start": v(22.04, -3.86) * mm, "end": v(22.24, -3.86) * mm});
            skLineSegment(sketch, "E52.63.24.0", {"start": v(22.81, -0.11) * mm, "end": v(23.1, -0.2) * mm});
            skLineSegment(sketch, "E52.66.24.0", {"start": v(22.57, -0.06) * mm, "end": v(22.81, -0.11) * mm});
            skLineSegment(sketch, "E52.69.24.0", {"start": v(22.24, 0) * mm, "end": v(22.38, -0.02) * mm});
            skLineSegment(sketch, "E52.72.24.0", {"start": v(21.8, -3.84) * mm, "end": v(21.82, -3.85) * mm});
            skLineSegment(sketch, "E52.75.24.0", {"start": v(21.82, -3.85) * mm, "end": v(21.9, -3.86) * mm});
            skLineSegment(sketch, "E52.78.24.0", {"start": v(22.38, -0.02) * mm, "end": v(22.57, -0.06) * mm});
            skLineSegment(sketch, "E52.81.24.0", {"start": v(21.9, -3.86) * mm, "end": v(22.04, -3.86) * mm});
            skLineSegment(sketch, "E52.84.24.0", {"start": v(22.16, 0) * mm, "end": v(22.24, 0) * mm});
            skLineSegment(sketch, "E52.87.24.0", {"start": v(22.13, 0) * mm, "end": v(22.16, 0) * mm});
            skLineSegment(sketch, "E52.2.25.0", {"start": v(19.75, 2.6) * mm, "end": v(21.94, 2.89) * mm});
            skLineSegment(sketch, "E52.3.25.0", {"start": v(25.26, 0.09) * mm, "end": v(25.8, 0.41) * mm});
            skLineSegment(sketch, "E52.6.25.0", {"start": v(19.9, -0.87) * mm, "end": v(22.11, -0.97) * mm});
            skLineSegment(sketch, "E52.9.25.0", {"start": v(24.74, -0.18) * mm, "end": v(25.26, 0.09) * mm});
            skLineSegment(sketch, "E52.12.25.0", {"start": v(24.63, 2.34) * mm, "end": v(25.17, 2.11) * mm});
            skLineSegment(sketch, "E52.15.25.0", {"start": v(25.17, 2.11) * mm, "end": v(25.74, 1.84) * mm});
            skLineSegment(sketch, "E52.18.25.0", {"start": v(24.27, -0.4) * mm, "end": v(24.74, -0.18) * mm});
            skLineSegment(sketch, "E52.21.25.0", {"start": v(26.38, 0.8) * mm, "end": v(26.99, 1.23) * mm});
            skLineSegment(sketch, "E52.24.25.0", {"start": v(23.83, -0.58) * mm, "end": v(24.27, -0.4) * mm});
            skLineSegment(sketch, "E52.27.25.0", {"start": v(26.35, 1.51) * mm, "end": v(27, 1.12) * mm});
            skLineSegment(sketch, "E52.30.25.0", {"start": v(25.8, 0.41) * mm, "end": v(26.38, 0.8) * mm});
            skLineSegment(sketch, "E52.33.25.0", {"start": v(24.14, 2.51) * mm, "end": v(24.63, 2.34) * mm});
            skLineSegment(sketch, "E52.36.25.0", {"start": v(25.74, 1.84) * mm, "end": v(26.35, 1.51) * mm});
            skLineSegment(sketch, "E52.39.25.0", {"start": v(22.8, -0.88) * mm, "end": v(23.1, -0.81) * mm});
            skLineSegment(sketch, "E52.42.25.0", {"start": v(23.1, -0.81) * mm, "end": v(23.44, -0.71) * mm});
            skLineSegment(sketch, "E52.45.25.0", {"start": v(23.44, -0.71) * mm, "end": v(23.83, -0.58) * mm});
            skLineSegment(sketch, "E52.48.25.0", {"start": v(23.29, 2.75) * mm, "end": v(23.69, 2.65) * mm});
            skLineSegment(sketch, "E52.51.25.0", {"start": v(22.93, 2.82) * mm, "end": v(23.29, 2.75) * mm});
            skLineSegment(sketch, "E52.54.25.0", {"start": v(23.69, 2.65) * mm, "end": v(24.14, 2.51) * mm});
            skLineSegment(sketch, "E52.57.25.0", {"start": v(22.55, -0.93) * mm, "end": v(22.8, -0.88) * mm});
            skLineSegment(sketch, "E52.60.25.0", {"start": v(22.36, -0.95) * mm, "end": v(22.55, -0.93) * mm});
            skLineSegment(sketch, "E52.63.25.0", {"start": v(22.63, 2.86) * mm, "end": v(22.93, 2.82) * mm});
            skLineSegment(sketch, "E52.66.25.0", {"start": v(22.38, 2.89) * mm, "end": v(22.63, 2.86) * mm});
            skLineSegment(sketch, "E52.69.25.0", {"start": v(22.05, 2.9) * mm, "end": v(22.2, 2.9) * mm});
            skLineSegment(sketch, "E52.72.25.0", {"start": v(22.11, -0.97) * mm, "end": v(22.14, -0.97) * mm});
            skLineSegment(sketch, "E52.75.25.0", {"start": v(22.14, -0.97) * mm, "end": v(22.22, -0.96) * mm});
            skLineSegment(sketch, "E52.78.25.0", {"start": v(22.2, 2.9) * mm, "end": v(22.38, 2.89) * mm});
            skLineSegment(sketch, "E52.81.25.0", {"start": v(22.22, -0.96) * mm, "end": v(22.36, -0.95) * mm});
            skLineSegment(sketch, "E52.84.25.0", {"start": v(21.97, 2.9) * mm, "end": v(22.05, 2.9) * mm});
            skLineSegment(sketch, "E52.87.25.0", {"start": v(21.94, 2.89) * mm, "end": v(21.97, 2.9) * mm});
            skLineSegment(sketch, "E52.2.26.0", {"start": v(19.24, 5.16) * mm, "end": v(21.38, 5.73) * mm});
            skLineSegment(sketch, "E52.3.26.0", {"start": v(25.03, 3.39) * mm, "end": v(25.53, 3.78) * mm});
            skLineSegment(sketch, "E52.6.26.0", {"start": v(19.85, 1.74) * mm, "end": v(22.05, 1.93) * mm});
            skLineSegment(sketch, "E52.9.26.0", {"start": v(24.56, 3.05) * mm, "end": v(25.03, 3.39) * mm});
            skLineSegment(sketch, "E52.12.26.0", {"start": v(24.12, 5.53) * mm, "end": v(24.68, 5.38) * mm});
            skLineSegment(sketch, "E52.15.26.0", {"start": v(24.68, 5.38) * mm, "end": v(25.28, 5.18) * mm});
            skLineSegment(sketch, "E52.18.26.0", {"start": v(24.11, 2.77) * mm, "end": v(24.56, 3.05) * mm});
            skLineSegment(sketch, "E52.21.26.0", {"start": v(26.06, 4.23) * mm, "end": v(26.6, 4.74) * mm});
            skLineSegment(sketch, "E52.24.26.0", {"start": v(23.7, 2.54) * mm, "end": v(24.11, 2.77) * mm});
            skLineSegment(sketch, "E52.27.26.0", {"start": v(25.93, 4.94) * mm, "end": v(26.61, 4.64) * mm});
            skLineSegment(sketch, "E52.30.26.0", {"start": v(25.53, 3.78) * mm, "end": v(26.06, 4.23) * mm});
            skLineSegment(sketch, "E52.33.26.0", {"start": v(23.6, 5.64) * mm, "end": v(24.12, 5.53) * mm});
            skLineSegment(sketch, "E52.36.26.0", {"start": v(25.28, 5.18) * mm, "end": v(25.93, 4.94) * mm});
            skLineSegment(sketch, "E52.39.26.0", {"start": v(22.72, 2.1) * mm, "end": v(23, 2.21) * mm});
            skLineSegment(sketch, "E52.42.26.0", {"start": v(23, 2.21) * mm, "end": v(23.33, 2.35) * mm});
            skLineSegment(sketch, "E52.45.26.0", {"start": v(23.33, 2.35) * mm, "end": v(23.7, 2.54) * mm});
            skLineSegment(sketch, "E52.48.26.0", {"start": v(22.73, 5.77) * mm, "end": v(23.14, 5.72) * mm});
            skLineSegment(sketch, "E52.51.26.0", {"start": v(22.37, 5.79) * mm, "end": v(22.73, 5.77) * mm});
            skLineSegment(sketch, "E52.54.26.0", {"start": v(23.14, 5.72) * mm, "end": v(23.6, 5.64) * mm});
            skLineSegment(sketch, "E52.57.26.0", {"start": v(22.48, 2.03) * mm, "end": v(22.72, 2.1) * mm});
            skLineSegment(sketch, "E52.60.26.0", {"start": v(22.3, 1.98) * mm, "end": v(22.48, 2.03) * mm});
            skLineSegment(sketch, "E52.63.26.0", {"start": v(22.07, 5.8) * mm, "end": v(22.37, 5.79) * mm});
            skLineSegment(sketch, "E52.66.26.0", {"start": v(21.82, 5.78) * mm, "end": v(22.07, 5.8) * mm});
            skLineSegment(sketch, "E52.69.26.0", {"start": v(21.49, 5.75) * mm, "end": v(21.62, 5.77) * mm});
            skLineSegment(sketch, "E52.72.26.0", {"start": v(22.05, 1.93) * mm, "end": v(22.08, 1.93) * mm});
            skLineSegment(sketch, "E52.75.26.0", {"start": v(22.08, 1.93) * mm, "end": v(22.16, 1.95) * mm});
            skLineSegment(sketch, "E52.78.26.0", {"start": v(21.62, 5.77) * mm, "end": v(21.82, 5.78) * mm});
            skLineSegment(sketch, "E52.81.26.0", {"start": v(22.16, 1.95) * mm, "end": v(22.3, 1.98) * mm});
            skLineSegment(sketch, "E52.84.26.0", {"start": v(21.4, 5.73) * mm, "end": v(21.49, 5.75) * mm});
            skLineSegment(sketch, "E52.87.26.0", {"start": v(21.38, 5.73) * mm, "end": v(21.4, 5.73) * mm});
            skLineSegment(sketch, "E52.2.27.0", {"start": v(18.4, 7.62) * mm, "end": v(20.45, 8.47) * mm});
            skLineSegment(sketch, "E52.3.27.0", {"start": v(24.37, 6.62) * mm, "end": v(24.82, 7.08) * mm});
            skLineSegment(sketch, "E52.6.27.0", {"start": v(19.45, 4.31) * mm, "end": v(21.6, 4.8) * mm});
            skLineSegment(sketch, "E52.9.27.0", {"start": v(23.95, 6.23) * mm, "end": v(24.37, 6.62) * mm});
            skLineSegment(sketch, "E52.12.27.0", {"start": v(23.19, 8.63) * mm, "end": v(23.77, 8.56) * mm});
            skLineSegment(sketch, "E52.15.27.0", {"start": v(23.77, 8.56) * mm, "end": v(24.4, 8.44) * mm});
            skLineSegment(sketch, "E52.18.27.0", {"start": v(23.54, 5.9) * mm, "end": v(23.95, 6.23) * mm});
            skLineSegment(sketch, "E52.21.27.0", {"start": v(25.28, 7.6) * mm, "end": v(25.75, 8.18) * mm});
            skLineSegment(sketch, "E52.24.27.0", {"start": v(23.17, 5.61) * mm, "end": v(23.54, 5.9) * mm});
            skLineSegment(sketch, "E52.27.27.0", {"start": v(25.06, 8.28) * mm, "end": v(25.78, 8.07) * mm});
            skLineSegment(sketch, "E52.30.27.0", {"start": v(24.82, 7.08) * mm, "end": v(25.28, 7.6) * mm});
            skLineSegment(sketch, "E52.33.27.0", {"start": v(22.67, 8.68) * mm, "end": v(23.19, 8.63) * mm});
            skLineSegment(sketch, "E52.36.27.0", {"start": v(24.4, 8.44) * mm, "end": v(25.06, 8.28) * mm});
            skLineSegment(sketch, "E52.39.27.0", {"start": v(22.25, 5.05) * mm, "end": v(22.52, 5.2) * mm});
            skLineSegment(sketch, "E52.42.27.0", {"start": v(22.52, 5.2) * mm, "end": v(22.82, 5.38) * mm});
            skLineSegment(sketch, "E52.45.27.0", {"start": v(22.82, 5.38) * mm, "end": v(23.17, 5.61) * mm});
            skLineSegment(sketch, "E52.48.27.0", {"start": v(21.78, 8.68) * mm, "end": v(22.2, 8.7) * mm});
            skLineSegment(sketch, "E52.51.27.0", {"start": v(21.42, 8.66) * mm, "end": v(21.78, 8.68) * mm});
            skLineSegment(sketch, "E52.54.27.0", {"start": v(22.2, 8.7) * mm, "end": v(22.67, 8.68) * mm});
            skLineSegment(sketch, "E52.57.27.0", {"start": v(22.02, 4.94) * mm, "end": v(22.25, 5.05) * mm});
            skLineSegment(sketch, "E52.60.27.0", {"start": v(21.84, 4.87) * mm, "end": v(22.02, 4.94) * mm});
            skLineSegment(sketch, "E52.63.27.0", {"start": v(21.12, 8.62) * mm, "end": v(21.42, 8.66) * mm});
            skLineSegment(sketch, "E52.66.27.0", {"start": v(20.87, 8.58) * mm, "end": v(21.12, 8.62) * mm});
            skLineSegment(sketch, "E52.69.27.0", {"start": v(20.55, 8.5) * mm, "end": v(20.69, 8.54) * mm});
            skLineSegment(sketch, "E52.72.27.0", {"start": v(21.6, 4.8) * mm, "end": v(21.63, 4.8) * mm});
            skLineSegment(sketch, "E52.75.27.0", {"start": v(21.63, 4.8) * mm, "end": v(21.71, 4.82) * mm});
            skLineSegment(sketch, "E52.78.27.0", {"start": v(20.69, 8.54) * mm, "end": v(20.87, 8.58) * mm});
            skLineSegment(sketch, "E52.81.27.0", {"start": v(21.71, 4.82) * mm, "end": v(21.84, 4.87) * mm});
            skLineSegment(sketch, "E52.84.27.0", {"start": v(20.47, 8.48) * mm, "end": v(20.55, 8.5) * mm});
            skLineSegment(sketch, "E52.87.27.0", {"start": v(20.45, 8.47) * mm, "end": v(20.47, 8.48) * mm});
            skLineSegment(sketch, "E52.2.28.0", {"start": v(17.25, 9.96) * mm, "end": v(19.17, 11.07) * mm});
            skLineSegment(sketch, "E52.3.28.0", {"start": v(23.3, 9.75) * mm, "end": v(23.68, 10.26) * mm});
            skLineSegment(sketch, "E52.6.28.0", {"start": v(18.72, 6.81) * mm, "end": v(20.8, 7.57) * mm});
            skLineSegment(sketch, "E52.9.28.0", {"start": v(22.93, 9.3) * mm, "end": v(23.3, 9.75) * mm});
            skLineSegment(sketch, "E52.12.28.0", {"start": v(21.86, 11.59) * mm, "end": v(22.45, 11.58) * mm});
            skLineSegment(sketch, "E52.15.28.0", {"start": v(22.45, 11.58) * mm, "end": v(23.08, 11.55) * mm});
            skLineSegment(sketch, "E52.18.28.0", {"start": v(22.57, 8.92) * mm, "end": v(22.93, 9.3) * mm});
            skLineSegment(sketch, "E52.21.28.0", {"start": v(24.07, 10.83) * mm, "end": v(24.46, 11.47) * mm});
            skLineSegment(sketch, "E52.24.28.0", {"start": v(22.24, 8.59) * mm, "end": v(22.57, 8.92) * mm});
            skLineSegment(sketch, "E52.27.28.0", {"start": v(23.77, 11.48) * mm, "end": v(24.5, 11.37) * mm});
            skLineSegment(sketch, "E52.30.28.0", {"start": v(23.68, 10.26) * mm, "end": v(24.07, 10.83) * mm});
            skLineSegment(sketch, "E52.33.28.0", {"start": v(21.34, 11.56) * mm, "end": v(21.86, 11.59) * mm});
            skLineSegment(sketch, "E52.36.28.0", {"start": v(23.08, 11.55) * mm, "end": v(23.77, 11.48) * mm});
            skLineSegment(sketch, "E52.39.28.0", {"start": v(21.4, 7.91) * mm, "end": v(21.64, 8.09) * mm});
            skLineSegment(sketch, "E52.42.28.0", {"start": v(21.64, 8.09) * mm, "end": v(21.93, 8.31) * mm});
            skLineSegment(sketch, "E52.45.28.0", {"start": v(21.93, 8.31) * mm, "end": v(22.24, 8.59) * mm});
            skLineSegment(sketch, "E52.48.28.0", {"start": v(20.46, 11.45) * mm, "end": v(20.87, 11.51) * mm});
            skLineSegment(sketch, "E52.51.28.0", {"start": v(20.1, 11.38) * mm, "end": v(20.46, 11.45) * mm});
            skLineSegment(sketch, "E52.54.28.0", {"start": v(20.87, 11.51) * mm, "end": v(21.34, 11.56) * mm});
            skLineSegment(sketch, "E52.57.28.0", {"start": v(21.19, 7.77) * mm, "end": v(21.4, 7.91) * mm});
            skLineSegment(sketch, "E52.60.28.0", {"start": v(21.02, 7.68) * mm, "end": v(21.19, 7.77) * mm});
            skLineSegment(sketch, "E52.63.28.0", {"start": v(19.81, 11.3) * mm, "end": v(20.1, 11.38) * mm});
            skLineSegment(sketch, "E52.66.28.0", {"start": v(19.58, 11.23) * mm, "end": v(19.81, 11.3) * mm});
            skLineSegment(sketch, "E52.69.28.0", {"start": v(19.27, 11.11) * mm, "end": v(19.4, 11.17) * mm});
            skLineSegment(sketch, "E52.72.28.0", {"start": v(20.8, 7.57) * mm, "end": v(20.82, 7.58) * mm});
            skLineSegment(sketch, "E52.75.28.0", {"start": v(20.82, 7.58) * mm, "end": v(20.9, 7.61) * mm});
            skLineSegment(sketch, "E52.78.28.0", {"start": v(19.4, 11.17) * mm, "end": v(19.58, 11.23) * mm});
            skLineSegment(sketch, "E52.81.28.0", {"start": v(20.9, 7.61) * mm, "end": v(21.02, 7.68) * mm});
            skLineSegment(sketch, "E52.84.28.0", {"start": v(19.2, 11.08) * mm, "end": v(19.27, 11.11) * mm});
            skLineSegment(sketch, "E52.87.28.0", {"start": v(19.17, 11.07) * mm, "end": v(19.2, 11.08) * mm});
            skLineSegment(sketch, "E52.2.29.0", {"start": v(15.8, 12.13) * mm, "end": v(17.56, 13.47) * mm});
            skLineSegment(sketch, "E52.3.29.0", {"start": v(21.83, 12.7) * mm, "end": v(22.14, 13.26) * mm});
            skLineSegment(sketch, "E52.6.29.0", {"start": v(17.67, 9.2) * mm, "end": v(19.63, 10.22) * mm});
            skLineSegment(sketch, "E52.9.29.0", {"start": v(21.52, 12.22) * mm, "end": v(21.83, 12.7) * mm});
            skLineSegment(sketch, "E52.12.29.0", {"start": v(20.17, 14.34) * mm, "end": v(20.74, 14.41) * mm});
            skLineSegment(sketch, "E52.15.29.0", {"start": v(20.74, 14.41) * mm, "end": v(21.38, 14.46) * mm});
            skLineSegment(sketch, "E52.18.29.0", {"start": v(21.22, 11.79) * mm, "end": v(21.52, 12.22) * mm});
            skLineSegment(sketch, "E52.21.29.0", {"start": v(22.45, 13.88) * mm, "end": v(22.76, 14.56) * mm});
            skLineSegment(sketch, "E52.24.29.0", {"start": v(20.92, 11.42) * mm, "end": v(21.22, 11.79) * mm});
            skLineSegment(sketch, "E52.27.29.0", {"start": v(22.07, 14.49) * mm, "end": v(22.81, 14.47) * mm});
            skLineSegment(sketch, "E52.30.29.0", {"start": v(22.14, 13.26) * mm, "end": v(22.45, 13.88) * mm});
            skLineSegment(sketch, "E52.33.29.0", {"start": v(19.65, 14.25) * mm, "end": v(20.17, 14.34) * mm});
            skLineSegment(sketch, "E52.36.29.0", {"start": v(21.38, 14.46) * mm, "end": v(22.07, 14.49) * mm});
            skLineSegment(sketch, "E52.39.29.0", {"start": v(20.18, 10.64) * mm, "end": v(20.4, 10.84) * mm});
            skLineSegment(sketch, "E52.42.29.0", {"start": v(20.4, 10.84) * mm, "end": v(20.65, 11.1) * mm});
            skLineSegment(sketch, "E52.45.29.0", {"start": v(20.65, 11.1) * mm, "end": v(20.92, 11.42) * mm});
            skLineSegment(sketch, "E52.48.29.0", {"start": v(18.8, 14.03) * mm, "end": v(19.2, 14.14) * mm});
            skLineSegment(sketch, "E52.51.29.0", {"start": v(18.45, 13.9) * mm, "end": v(18.8, 14.03) * mm});
            skLineSegment(sketch, "E52.54.29.0", {"start": v(19.2, 14.14) * mm, "end": v(19.65, 14.25) * mm});
            skLineSegment(sketch, "E52.57.29.0", {"start": v(20, 10.47) * mm, "end": v(20.18, 10.64) * mm});
            skLineSegment(sketch, "E52.60.29.0", {"start": v(19.84, 10.36) * mm, "end": v(20, 10.47) * mm});
            skLineSegment(sketch, "E52.63.29.0", {"start": v(18.17, 13.8) * mm, "end": v(18.45, 13.9) * mm});
            skLineSegment(sketch, "E52.66.29.0", {"start": v(17.94, 13.7) * mm, "end": v(18.17, 13.8) * mm});
            skLineSegment(sketch, "E52.69.29.0", {"start": v(17.65, 13.53) * mm, "end": v(17.77, 13.6) * mm});
            skLineSegment(sketch, "E52.72.29.0", {"start": v(19.63, 10.22) * mm, "end": v(19.66, 10.23) * mm});
            skLineSegment(sketch, "E52.75.29.0", {"start": v(19.66, 10.23) * mm, "end": v(19.73, 10.28) * mm});
            skLineSegment(sketch, "E52.78.29.0", {"start": v(17.77, 13.6) * mm, "end": v(17.94, 13.7) * mm});
            skLineSegment(sketch, "E52.81.29.0", {"start": v(19.73, 10.28) * mm, "end": v(19.84, 10.36) * mm});
            skLineSegment(sketch, "E52.84.29.0", {"start": v(17.58, 13.49) * mm, "end": v(17.65, 13.53) * mm});
            skLineSegment(sketch, "E52.87.29.0", {"start": v(17.56, 13.47) * mm, "end": v(17.58, 13.49) * mm});
            skLineSegment(sketch, "E52.2.30.0", {"start": v(14.09, 14.09) * mm, "end": v(15.65, 15.65) * mm});
            skLineSegment(sketch, "E52.3.30.0", {"start": v(19.98, 15.45) * mm, "end": v(20.22, 16.04) * mm});
            skLineSegment(sketch, "E52.6.30.0", {"start": v(16.32, 11.43) * mm, "end": v(18.13, 12.7) * mm});
            skLineSegment(sketch, "E52.9.30.0", {"start": v(19.74, 14.92) * mm, "end": v(19.98, 15.45) * mm});
            skLineSegment(sketch, "E52.12.30.0", {"start": v(18.12, 16.85) * mm, "end": v(18.68, 17) * mm});
            skLineSegment(sketch, "E52.15.30.0", {"start": v(18.68, 17) * mm, "end": v(19.3, 17.13) * mm});
            skLineSegment(sketch, "E52.18.30.0", {"start": v(19.5, 14.45) * mm, "end": v(19.74, 14.92) * mm});
            skLineSegment(sketch, "E52.21.30.0", {"start": v(20.45, 16.69) * mm, "end": v(20.66, 17.4) * mm});
            skLineSegment(sketch, "E52.24.30.0", {"start": v(19.26, 14.05) * mm, "end": v(19.5, 14.45) * mm});
            skLineSegment(sketch, "E52.27.30.0", {"start": v(19.99, 17.24) * mm, "end": v(20.73, 17.32) * mm});
            skLineSegment(sketch, "E52.30.30.0", {"start": v(20.22, 16.04) * mm, "end": v(20.45, 16.69) * mm});
            skLineSegment(sketch, "E52.33.30.0", {"start": v(17.62, 16.69) * mm, "end": v(18.12, 16.85) * mm});
            skLineSegment(sketch, "E52.36.30.0", {"start": v(19.3, 17.13) * mm, "end": v(19.99, 17.24) * mm});
            skLineSegment(sketch, "E52.39.30.0", {"start": v(18.62, 13.18) * mm, "end": v(18.81, 13.41) * mm});
            skLineSegment(sketch, "E52.42.30.0", {"start": v(18.81, 13.41) * mm, "end": v(19.03, 13.7) * mm});
            skLineSegment(sketch, "E52.45.30.0", {"start": v(19.03, 13.7) * mm, "end": v(19.26, 14.05) * mm});
            skLineSegment(sketch, "E52.48.30.0", {"start": v(16.8, 16.36) * mm, "end": v(17.18, 16.52) * mm});
            skLineSegment(sketch, "E52.51.30.0", {"start": v(16.48, 16.2) * mm, "end": v(16.8, 16.36) * mm});
            skLineSegment(sketch, "E52.54.30.0", {"start": v(17.18, 16.52) * mm, "end": v(17.62, 16.69) * mm});
            skLineSegment(sketch, "E52.57.30.0", {"start": v(18.45, 13) * mm, "end": v(18.62, 13.18) * mm});
            skLineSegment(sketch, "E52.60.30.0", {"start": v(18.32, 12.86) * mm, "end": v(18.45, 13) * mm});
            skLineSegment(sketch, "E52.63.30.0", {"start": v(16.21, 16.05) * mm, "end": v(16.48, 16.2) * mm});
            skLineSegment(sketch, "E52.66.30.0", {"start": v(16, 15.92) * mm, "end": v(16.21, 16.05) * mm});
            skLineSegment(sketch, "E52.69.30.0", {"start": v(15.73, 15.72) * mm, "end": v(15.84, 15.8) * mm});
            skLineSegment(sketch, "E52.72.30.0", {"start": v(18.13, 12.7) * mm, "end": v(18.15, 12.71) * mm});
            skLineSegment(sketch, "E52.75.30.0", {"start": v(18.15, 12.71) * mm, "end": v(18.22, 12.76) * mm});
            skLineSegment(sketch, "E52.78.30.0", {"start": v(15.84, 15.8) * mm, "end": v(16, 15.92) * mm});
            skLineSegment(sketch, "E52.81.30.0", {"start": v(18.22, 12.76) * mm, "end": v(18.32, 12.86) * mm});
            skLineSegment(sketch, "E52.84.30.0", {"start": v(15.67, 15.67) * mm, "end": v(15.73, 15.72) * mm});
            skLineSegment(sketch, "E52.87.30.0", {"start": v(15.65, 15.65) * mm, "end": v(15.67, 15.67) * mm});
            skLineSegment(sketch, "E52.2.31.0", {"start": v(12.13, 15.8) * mm, "end": v(13.47, 17.56) * mm});
            skLineSegment(sketch, "E52.3.31.0", {"start": v(17.8, 17.92) * mm, "end": v(17.96, 18.54) * mm});
            skLineSegment(sketch, "E52.6.31.0", {"start": v(14.69, 13.46) * mm, "end": v(16.32, 14.95) * mm});
            skLineSegment(sketch, "E52.9.31.0", {"start": v(17.62, 17.37) * mm, "end": v(17.8, 17.92) * mm});
            skLineSegment(sketch, "E52.12.31.0", {"start": v(15.77, 19.07) * mm, "end": v(16.3, 19.3) * mm});
            skLineSegment(sketch, "E52.15.31.0", {"start": v(16.3, 19.3) * mm, "end": v(16.9, 19.5) * mm});
            skLineSegment(sketch, "E52.18.31.0", {"start": v(17.44, 16.88) * mm, "end": v(17.62, 17.37) * mm});
            skLineSegment(sketch, "E52.21.31.0", {"start": v(18.1, 19.22) * mm, "end": v(18.21, 19.95) * mm});
            skLineSegment(sketch, "E52.24.31.0", {"start": v(17.26, 16.44) * mm, "end": v(17.44, 16.88) * mm});
            skLineSegment(sketch, "E52.27.31.0", {"start": v(17.57, 19.7) * mm, "end": v(18.3, 19.88) * mm});
            skLineSegment(sketch, "E52.30.31.0", {"start": v(17.96, 18.54) * mm, "end": v(18.1, 19.22) * mm});
            skLineSegment(sketch, "E52.33.31.0", {"start": v(15.3, 18.85) * mm, "end": v(15.77, 19.07) * mm});
            skLineSegment(sketch, "E52.36.31.0", {"start": v(16.9, 19.5) * mm, "end": v(17.57, 19.7) * mm});
            skLineSegment(sketch, "E52.39.31.0", {"start": v(16.74, 15.5) * mm, "end": v(16.9, 15.76) * mm});
            skLineSegment(sketch, "E52.42.31.0", {"start": v(16.9, 15.76) * mm, "end": v(17.08, 16.07) * mm});
            skLineSegment(sketch, "E52.45.31.0", {"start": v(17.08, 16.07) * mm, "end": v(17.26, 16.44) * mm});
            skLineSegment(sketch, "E52.48.31.0", {"start": v(14.52, 18.41) * mm, "end": v(14.88, 18.62) * mm});
            skLineSegment(sketch, "E52.51.31.0", {"start": v(14.22, 18.21) * mm, "end": v(14.52, 18.41) * mm});
            skLineSegment(sketch, "E52.54.31.0", {"start": v(14.88, 18.62) * mm, "end": v(15.3, 18.85) * mm});
            skLineSegment(sketch, "E52.57.31.0", {"start": v(16.6, 15.3) * mm, "end": v(16.74, 15.5) * mm});
            skLineSegment(sketch, "E52.60.31.0", {"start": v(16.48, 15.14) * mm, "end": v(16.6, 15.3) * mm});
            skLineSegment(sketch, "E52.63.31.0", {"start": v(13.98, 18.03) * mm, "end": v(14.22, 18.21) * mm});
            skLineSegment(sketch, "E52.66.31.0", {"start": v(13.79, 17.87) * mm, "end": v(13.98, 18.03) * mm});
            skLineSegment(sketch, "E52.69.31.0", {"start": v(13.55, 17.64) * mm, "end": v(13.64, 17.74) * mm});
            skLineSegment(sketch, "E52.72.31.0", {"start": v(16.32, 14.95) * mm, "end": v(16.34, 14.97) * mm});
            skLineSegment(sketch, "E52.75.31.0", {"start": v(16.34, 14.97) * mm, "end": v(16.4, 15.03) * mm});
            skLineSegment(sketch, "E52.78.31.0", {"start": v(13.64, 17.74) * mm, "end": v(13.79, 17.87) * mm});
            skLineSegment(sketch, "E52.81.31.0", {"start": v(16.4, 15.03) * mm, "end": v(16.48, 15.14) * mm});
            skLineSegment(sketch, "E52.84.31.0", {"start": v(13.5, 17.58) * mm, "end": v(13.55, 17.64) * mm});
            skLineSegment(sketch, "E52.87.31.0", {"start": v(13.47, 17.56) * mm, "end": v(13.5, 17.58) * mm});
            skLineSegment(sketch, "E52.2.32.0", {"start": v(9.96, 17.25) * mm, "end": v(11.07, 19.17) * mm});
            skLineSegment(sketch, "E52.3.32.0", {"start": v(15.3, 20.1) * mm, "end": v(15.38, 20.72) * mm});
            skLineSegment(sketch, "E52.6.32.0", {"start": v(12.8, 15.26) * mm, "end": v(14.23, 16.95) * mm});
            skLineSegment(sketch, "E52.9.32.0", {"start": v(15.2, 19.52) * mm, "end": v(15.3, 20.1) * mm});
            skLineSegment(sketch, "E52.12.32.0", {"start": v(13.14, 20.97) * mm, "end": v(13.65, 21.25) * mm});
            skLineSegment(sketch, "E52.15.32.0", {"start": v(13.65, 21.25) * mm, "end": v(14.21, 21.54) * mm});
            skLineSegment(sketch, "E52.18.32.0", {"start": v(15.09, 19) * mm, "end": v(15.2, 19.52) * mm});
            skLineSegment(sketch, "E52.21.32.0", {"start": v(15.43, 21.41) * mm, "end": v(15.45, 22.16) * mm});
            skLineSegment(sketch, "E52.24.32.0", {"start": v(14.96, 18.56) * mm, "end": v(15.09, 19) * mm});
            skLineSegment(sketch, "E52.27.32.0", {"start": v(14.84, 21.83) * mm, "end": v(15.54, 22.1) * mm});
            skLineSegment(sketch, "E52.30.32.0", {"start": v(15.38, 20.72) * mm, "end": v(15.43, 21.41) * mm});
            skLineSegment(sketch, "E52.33.32.0", {"start": v(12.7, 20.68) * mm, "end": v(13.14, 20.97) * mm});
            skLineSegment(sketch, "E52.36.32.0", {"start": v(14.21, 21.54) * mm, "end": v(14.84, 21.83) * mm});
            skLineSegment(sketch, "E52.39.32.0", {"start": v(14.58, 17.55) * mm, "end": v(14.7, 17.83) * mm});
            skLineSegment(sketch, "E52.42.32.0", {"start": v(14.7, 17.83) * mm, "end": v(14.83, 18.16) * mm});
            skLineSegment(sketch, "E52.45.32.0", {"start": v(14.83, 18.16) * mm, "end": v(14.96, 18.56) * mm});
            skLineSegment(sketch, "E52.48.32.0", {"start": v(12, 20.15) * mm, "end": v(12.32, 20.4) * mm});
            skLineSegment(sketch, "E52.51.32.0", {"start": v(11.72, 19.91) * mm, "end": v(12, 20.15) * mm});
            skLineSegment(sketch, "E52.54.32.0", {"start": v(12.32, 20.4) * mm, "end": v(12.7, 20.68) * mm});
            skLineSegment(sketch, "E52.57.32.0", {"start": v(14.46, 17.33) * mm, "end": v(14.58, 17.55) * mm});
            skLineSegment(sketch, "E52.60.32.0", {"start": v(14.37, 17.16) * mm, "end": v(14.46, 17.33) * mm});
            skLineSegment(sketch, "E52.63.32.0", {"start": v(11.5, 19.7) * mm, "end": v(11.72, 19.91) * mm});
            skLineSegment(sketch, "E52.66.32.0", {"start": v(11.34, 19.52) * mm, "end": v(11.5, 19.7) * mm});
            skLineSegment(sketch, "E52.69.32.0", {"start": v(11.13, 19.26) * mm, "end": v(11.21, 19.37) * mm});
            skLineSegment(sketch, "E52.72.32.0", {"start": v(14.23, 16.95) * mm, "end": v(14.24, 16.98) * mm});
            skLineSegment(sketch, "E52.75.32.0", {"start": v(14.24, 16.98) * mm, "end": v(14.3, 17.04) * mm});
            skLineSegment(sketch, "E52.78.32.0", {"start": v(11.21, 19.37) * mm, "end": v(11.34, 19.52) * mm});
            skLineSegment(sketch, "E52.81.32.0", {"start": v(14.3, 17.04) * mm, "end": v(14.37, 17.16) * mm});
            skLineSegment(sketch, "E52.84.32.0", {"start": v(11.08, 19.2) * mm, "end": v(11.13, 19.26) * mm});
            skLineSegment(sketch, "E52.87.32.0", {"start": v(11.07, 19.17) * mm, "end": v(11.08, 19.2) * mm});
            skLineSegment(sketch, "E52.2.33.0", {"start": v(7.62, 18.4) * mm, "end": v(8.47, 20.45) * mm});
            skLineSegment(sketch, "E52.3.33.0", {"start": v(12.55, 21.92) * mm, "end": v(12.55, 22.56) * mm});
            skLineSegment(sketch, "E52.6.33.0", {"start": v(10.7, 16.8) * mm, "end": v(11.9, 18.67) * mm});
            skLineSegment(sketch, "E52.9.33.0", {"start": v(12.53, 21.34) * mm, "end": v(12.55, 21.92) * mm});
            skLineSegment(sketch, "E52.12.33.0", {"start": v(10.3, 22.5) * mm, "end": v(10.76, 22.85) * mm});
            skLineSegment(sketch, "E52.15.33.0", {"start": v(10.76, 22.85) * mm, "end": v(11.28, 23.21) * mm});
            skLineSegment(sketch, "E52.18.33.0", {"start": v(12.48, 20.82) * mm, "end": v(12.53, 21.34) * mm});
            skLineSegment(sketch, "E52.21.33.0", {"start": v(12.5, 23.25) * mm, "end": v(12.43, 23.99) * mm});
            skLineSegment(sketch, "E52.24.33.0", {"start": v(12.41, 20.35) * mm, "end": v(12.48, 20.82) * mm});
            skLineSegment(sketch, "E52.27.33.0", {"start": v(11.87, 23.58) * mm, "end": v(12.52, 23.94) * mm});
            skLineSegment(sketch, "E52.30.33.0", {"start": v(12.55, 22.56) * mm, "end": v(12.5, 23.25) * mm});
            skLineSegment(sketch, "E52.33.33.0", {"start": v(9.9, 22.16) * mm, "end": v(10.3, 22.5) * mm});
            skLineSegment(sketch, "E52.36.33.0", {"start": v(11.28, 23.21) * mm, "end": v(11.87, 23.58) * mm});
            skLineSegment(sketch, "E52.39.33.0", {"start": v(12.16, 19.3) * mm, "end": v(12.25, 19.6) * mm});
            skLineSegment(sketch, "E52.42.33.0", {"start": v(12.25, 19.6) * mm, "end": v(12.33, 19.94) * mm});
            skLineSegment(sketch, "E52.45.33.0", {"start": v(12.33, 19.94) * mm, "end": v(12.41, 20.35) * mm});
            skLineSegment(sketch, "E52.48.33.0", {"start": v(9.26, 21.54) * mm, "end": v(9.55, 21.84) * mm});
            skLineSegment(sketch, "E52.51.33.0", {"start": v(9.02, 21.27) * mm, "end": v(9.26, 21.54) * mm});
            skLineSegment(sketch, "E52.54.33.0", {"start": v(9.55, 21.84) * mm, "end": v(9.9, 22.16) * mm});
            skLineSegment(sketch, "E52.57.33.0", {"start": v(12.08, 19.07) * mm, "end": v(12.16, 19.3) * mm});
            skLineSegment(sketch, "E52.60.33.0", {"start": v(12, 18.89) * mm, "end": v(12.08, 19.07) * mm});
            skLineSegment(sketch, "E52.63.33.0", {"start": v(8.84, 21.03) * mm, "end": v(9.02, 21.27) * mm});
            skLineSegment(sketch, "E52.66.33.0", {"start": v(8.7, 20.83) * mm, "end": v(8.84, 21.03) * mm});
            skLineSegment(sketch, "E52.69.33.0", {"start": v(8.52, 20.55) * mm, "end": v(8.59, 20.67) * mm});
            skLineSegment(sketch, "E52.72.33.0", {"start": v(11.9, 18.67) * mm, "end": v(11.9, 18.69) * mm});
            skLineSegment(sketch, "E52.75.33.0", {"start": v(11.9, 18.69) * mm, "end": v(11.94, 18.76) * mm});
            skLineSegment(sketch, "E52.78.33.0", {"start": v(8.59, 20.67) * mm, "end": v(8.7, 20.83) * mm});
            skLineSegment(sketch, "E52.81.33.0", {"start": v(11.94, 18.76) * mm, "end": v(12, 18.89) * mm});
            skLineSegment(sketch, "E52.84.33.0", {"start": v(8.48, 20.47) * mm, "end": v(8.52, 20.55) * mm});
            skLineSegment(sketch, "E52.87.33.0", {"start": v(8.47, 20.45) * mm, "end": v(8.48, 20.47) * mm});
            skLineSegment(sketch, "E52.2.34.0", {"start": v(5.16, 19.24) * mm, "end": v(5.73, 21.38) * mm});
            skLineSegment(sketch, "E52.3.34.0", {"start": v(9.58, 23.37) * mm, "end": v(9.5, 24) * mm});
            skLineSegment(sketch, "E52.6.34.0", {"start": v(8.42, 18.05) * mm, "end": v(9.35, 20.06) * mm});
            skLineSegment(sketch, "E52.9.34.0", {"start": v(9.64, 22.8) * mm, "end": v(9.58, 23.37) * mm});
            skLineSegment(sketch, "E52.12.34.0", {"start": v(7.27, 23.65) * mm, "end": v(7.68, 24.06) * mm});
            skLineSegment(sketch, "E52.15.34.0", {"start": v(7.68, 24.06) * mm, "end": v(8.15, 24.49) * mm});
            skLineSegment(sketch, "E52.18.34.0", {"start": v(9.66, 22.27) * mm, "end": v(9.64, 22.8) * mm});
            skLineSegment(sketch, "E52.21.34.0", {"start": v(9.37, 24.68) * mm, "end": v(9.19, 25.4) * mm});
            skLineSegment(sketch, "E52.24.34.0", {"start": v(9.65, 21.8) * mm, "end": v(9.66, 22.27) * mm});
            skLineSegment(sketch, "E52.27.34.0", {"start": v(8.69, 24.93) * mm, "end": v(9.3, 25.37) * mm});
            skLineSegment(sketch, "E52.30.34.0", {"start": v(9.5, 24) * mm, "end": v(9.37, 24.68) * mm});
            skLineSegment(sketch, "E52.33.34.0", {"start": v(6.92, 23.26) * mm, "end": v(7.27, 23.65) * mm});
            skLineSegment(sketch, "E52.36.34.0", {"start": v(8.15, 24.49) * mm, "end": v(8.69, 24.93) * mm});
            skLineSegment(sketch, "E52.39.34.0", {"start": v(9.54, 20.72) * mm, "end": v(9.59, 21.02) * mm});
            skLineSegment(sketch, "E52.42.34.0", {"start": v(9.59, 21.02) * mm, "end": v(9.63, 21.38) * mm});
            skLineSegment(sketch, "E52.45.34.0", {"start": v(9.63, 21.38) * mm, "end": v(9.65, 21.8) * mm});
            skLineSegment(sketch, "E52.48.34.0", {"start": v(6.37, 22.57) * mm, "end": v(6.62, 22.9) * mm});
            skLineSegment(sketch, "E52.51.34.0", {"start": v(6.17, 22.27) * mm, "end": v(6.37, 22.57) * mm});
            skLineSegment(sketch, "E52.54.34.0", {"start": v(6.62, 22.9) * mm, "end": v(6.92, 23.26) * mm});
            skLineSegment(sketch, "E52.57.34.0", {"start": v(9.49, 20.48) * mm, "end": v(9.54, 20.72) * mm});
            skLineSegment(sketch, "E52.60.34.0", {"start": v(9.44, 20.3) * mm, "end": v(9.49, 20.48) * mm});
            skLineSegment(sketch, "E52.63.34.0", {"start": v(6.02, 22) * mm, "end": v(6.17, 22.27) * mm});
            skLineSegment(sketch, "E52.66.34.0", {"start": v(5.9, 21.79) * mm, "end": v(6.02, 22) * mm});
            skLineSegment(sketch, "E52.69.34.0", {"start": v(5.76, 21.48) * mm, "end": v(5.82, 21.61) * mm});
            skLineSegment(sketch, "E52.72.34.0", {"start": v(9.35, 20.06) * mm, "end": v(9.36, 20.08) * mm});
            skLineSegment(sketch, "E52.75.34.0", {"start": v(9.36, 20.08) * mm, "end": v(9.4, 20.16) * mm});
            skLineSegment(sketch, "E52.78.34.0", {"start": v(5.82, 21.61) * mm, "end": v(5.9, 21.79) * mm});
            skLineSegment(sketch, "E52.81.34.0", {"start": v(9.4, 20.16) * mm, "end": v(9.44, 20.3) * mm});
            skLineSegment(sketch, "E52.84.34.0", {"start": v(5.74, 21.4) * mm, "end": v(5.76, 21.48) * mm});
            skLineSegment(sketch, "E52.87.34.0", {"start": v(5.73, 21.38) * mm, "end": v(5.74, 21.4) * mm});
            skLineSegment(sketch, "E52.2.35.0", {"start": v(2.6, 19.75) * mm, "end": v(2.89, 21.94) * mm});
            skLineSegment(sketch, "E52.3.35.0", {"start": v(6.45, 24.42) * mm, "end": v(6.28, 25.03) * mm});
            skLineSegment(sketch, "E52.6.35.0", {"start": v(6, 19) * mm, "end": v(6.66, 21.1) * mm});
            skLineSegment(sketch, "E52.9.35.0", {"start": v(6.58, 23.85) * mm, "end": v(6.45, 24.42) * mm});
            skLineSegment(sketch, "E52.12.35.0", {"start": v(4.12, 24.4) * mm, "end": v(4.47, 24.86) * mm});
            skLineSegment(sketch, "E52.15.35.0", {"start": v(4.47, 24.86) * mm, "end": v(4.89, 25.34) * mm});
            skLineSegment(sketch, "E52.18.35.0", {"start": v(6.67, 23.34) * mm, "end": v(6.58, 23.85) * mm});
            skLineSegment(sketch, "E52.21.35.0", {"start": v(6.06, 25.7) * mm, "end": v(5.8, 26.39) * mm});
            skLineSegment(sketch, "E52.24.35.0", {"start": v(6.72, 22.87) * mm, "end": v(6.67, 23.34) * mm});
            skLineSegment(sketch, "E52.27.35.0", {"start": v(5.36, 25.85) * mm, "end": v(5.9, 26.36) * mm});
            skLineSegment(sketch, "E52.30.35.0", {"start": v(6.28, 25.03) * mm, "end": v(6.06, 25.7) * mm});
            skLineSegment(sketch, "E52.33.35.0", {"start": v(3.82, 23.97) * mm, "end": v(4.12, 24.4) * mm});
            skLineSegment(sketch, "E52.36.35.0", {"start": v(4.89, 25.34) * mm, "end": v(5.36, 25.85) * mm});
            skLineSegment(sketch, "E52.39.35.0", {"start": v(6.75, 21.8) * mm, "end": v(6.76, 22.1) * mm});
            skLineSegment(sketch, "E52.42.35.0", {"start": v(6.76, 22.1) * mm, "end": v(6.75, 22.45) * mm});
            skLineSegment(sketch, "E52.45.35.0", {"start": v(6.75, 22.45) * mm, "end": v(6.72, 22.87) * mm});
            skLineSegment(sketch, "E52.48.35.0", {"start": v(3.37, 23.2) * mm, "end": v(3.57, 23.57) * mm});
            skLineSegment(sketch, "E52.51.35.0", {"start": v(3.21, 22.88) * mm, "end": v(3.37, 23.2) * mm});
            skLineSegment(sketch, "E52.54.35.0", {"start": v(3.57, 23.57) * mm, "end": v(3.82, 23.97) * mm});
            skLineSegment(sketch, "E52.57.35.0", {"start": v(6.73, 21.54) * mm, "end": v(6.75, 21.8) * mm});
            skLineSegment(sketch, "E52.60.35.0", {"start": v(6.7, 21.35) * mm, "end": v(6.73, 21.54) * mm});
            skLineSegment(sketch, "E52.63.35.0", {"start": v(3.1, 22.6) * mm, "end": v(3.21, 22.88) * mm});
            skLineSegment(sketch, "E52.66.35.0", {"start": v(3, 22.37) * mm, "end": v(3.1, 22.6) * mm});
            skLineSegment(sketch, "E52.69.35.0", {"start": v(2.91, 22.05) * mm, "end": v(2.95, 22.18) * mm});
            skLineSegment(sketch, "E52.72.35.0", {"start": v(6.66, 21.1) * mm, "end": v(6.66, 21.13) * mm});
            skLineSegment(sketch, "E52.75.35.0", {"start": v(6.66, 21.13) * mm, "end": v(6.68, 21.22) * mm});
            skLineSegment(sketch, "E52.78.35.0", {"start": v(2.95, 22.18) * mm, "end": v(3, 22.37) * mm});
            skLineSegment(sketch, "E52.81.35.0", {"start": v(6.68, 21.22) * mm, "end": v(6.7, 21.35) * mm});
            skLineSegment(sketch, "E52.84.35.0", {"start": v(2.9, 21.97) * mm, "end": v(2.91, 22.05) * mm});
            skLineSegment(sketch, "E52.87.35.0", {"start": v(2.89, 21.94) * mm, "end": v(2.9, 21.97) * mm});
            skLineSegment(sketch, "E52.2.36.0", {"start": v(0, 19.92) * mm, "end": v(0, 22.13) * mm});
            skLineSegment(sketch, "E52.3.36.0", {"start": v(3.2, 25.05) * mm, "end": v(2.96, 25.64) * mm});
            skLineSegment(sketch, "E52.6.36.0", {"start": v(3.46, 19.62) * mm, "end": v(3.84, 21.8) * mm});
            skLineSegment(sketch, "E52.9.36.0", {"start": v(3.4, 24.5) * mm, "end": v(3.2, 25.05) * mm});
            skLineSegment(sketch, "E52.12.36.0", {"start": v(0.9, 24.73) * mm, "end": v(1.2, 25.23) * mm});
            skLineSegment(sketch, "E52.15.36.0", {"start": v(1.2, 25.23) * mm, "end": v(1.54, 25.76) * mm});
            skLineSegment(sketch, "E52.18.36.0", {"start": v(3.56, 24) * mm, "end": v(3.4, 24.5) * mm});
            skLineSegment(sketch, "E52.21.36.0", {"start": v(2.66, 26.26) * mm, "end": v(2.3, 26.92) * mm});
            skLineSegment(sketch, "E52.24.36.0", {"start": v(3.68, 23.55) * mm, "end": v(3.56, 24) * mm});
            skLineSegment(sketch, "E52.27.36.0", {"start": v(1.94, 26.32) * mm, "end": v(2.4, 26.9) * mm});
            skLineSegment(sketch, "E52.30.36.0", {"start": v(2.96, 25.64) * mm, "end": v(2.66, 26.26) * mm});
            skLineSegment(sketch, "E52.33.36.0", {"start": v(0.66, 24.26) * mm, "end": v(0.9, 24.73) * mm});
            skLineSegment(sketch, "E52.36.36.0", {"start": v(1.54, 25.76) * mm, "end": v(1.94, 26.32) * mm});
            skLineSegment(sketch, "E52.39.36.0", {"start": v(3.85, 22.49) * mm, "end": v(3.82, 22.79) * mm});
            skLineSegment(sketch, "E52.42.36.0", {"start": v(3.82, 22.79) * mm, "end": v(3.76, 23.14) * mm});
            skLineSegment(sketch, "E52.45.36.0", {"start": v(3.76, 23.14) * mm, "end": v(3.68, 23.55) * mm});
            skLineSegment(sketch, "E52.48.36.0", {"start": v(0.31, 23.45) * mm, "end": v(0.46, 23.83) * mm});
            skLineSegment(sketch, "E52.51.36.0", {"start": v(0.2, 23.1) * mm, "end": v(0.31, 23.45) * mm});
            skLineSegment(sketch, "E52.54.36.0", {"start": v(0.46, 23.83) * mm, "end": v(0.66, 24.26) * mm});
            skLineSegment(sketch, "E52.57.36.0", {"start": v(3.86, 22.24) * mm, "end": v(3.85, 22.49) * mm});
            skLineSegment(sketch, "E52.60.36.0", {"start": v(3.86, 22.04) * mm, "end": v(3.86, 22.24) * mm});
            skLineSegment(sketch, "E52.63.36.0", {"start": v(0.11, 22.81) * mm, "end": v(0.2, 23.1) * mm});
            skLineSegment(sketch, "E52.66.36.0", {"start": v(0.06, 22.57) * mm, "end": v(0.11, 22.81) * mm});
            skLineSegment(sketch, "E52.69.36.0", {"start": v(0, 22.24) * mm, "end": v(0.02, 22.38) * mm});
            skLineSegment(sketch, "E52.72.36.0", {"start": v(3.84, 21.8) * mm, "end": v(3.85, 21.82) * mm});
            skLineSegment(sketch, "E52.75.36.0", {"start": v(3.85, 21.82) * mm, "end": v(3.86, 21.9) * mm});
            skLineSegment(sketch, "E52.78.36.0", {"start": v(0.02, 22.38) * mm, "end": v(0.06, 22.57) * mm});
            skLineSegment(sketch, "E52.81.36.0", {"start": v(3.86, 21.9) * mm, "end": v(3.86, 22.04) * mm});
            skLineSegment(sketch, "E52.84.36.0", {"start": v(0, 22.16) * mm, "end": v(0, 22.24) * mm});
            skLineSegment(sketch, "E52.87.36.0", {"start": v(0, 22.13) * mm, "end": v(0, 22.16) * mm});
            skLineSegment(sketch, "E52.2.37.0", {"start": v(-2.6, 19.75) * mm, "end": v(-2.89, 21.94) * mm});
            skLineSegment(sketch, "E52.3.37.0", {"start": v(-0.09, 25.26) * mm, "end": v(-0.41, 25.8) * mm});
            skLineSegment(sketch, "E52.6.37.0", {"start": v(0.87, 19.9) * mm, "end": v(0.97, 22.11) * mm});
            skLineSegment(sketch, "E52.9.37.0", {"start": v(0.18, 24.74) * mm, "end": v(-0.09, 25.26) * mm});
            skLineSegment(sketch, "E52.12.37.0", {"start": v(-2.34, 24.63) * mm, "end": v(-2.11, 25.17) * mm});
            skLineSegment(sketch, "E52.15.37.0", {"start": v(-2.11, 25.17) * mm, "end": v(-1.84, 25.74) * mm});
            skLineSegment(sketch, "E52.18.37.0", {"start": v(0.4, 24.27) * mm, "end": v(0.18, 24.74) * mm});
            skLineSegment(sketch, "E52.21.37.0", {"start": v(-0.8, 26.38) * mm, "end": v(-1.23, 26.99) * mm});
            skLineSegment(sketch, "E52.24.37.0", {"start": v(0.58, 23.83) * mm, "end": v(0.4, 24.27) * mm});
            skLineSegment(sketch, "E52.27.37.0", {"start": v(-1.51, 26.35) * mm, "end": v(-1.12, 27) * mm});
            skLineSegment(sketch, "E52.30.37.0", {"start": v(-0.41, 25.8) * mm, "end": v(-0.8, 26.38) * mm});
            skLineSegment(sketch, "E52.33.37.0", {"start": v(-2.51, 24.14) * mm, "end": v(-2.34, 24.63) * mm});
            skLineSegment(sketch, "E52.36.37.0", {"start": v(-1.84, 25.74) * mm, "end": v(-1.51, 26.35) * mm});
            skLineSegment(sketch, "E52.39.37.0", {"start": v(0.88, 22.8) * mm, "end": v(0.81, 23.1) * mm});
            skLineSegment(sketch, "E52.42.37.0", {"start": v(0.81, 23.1) * mm, "end": v(0.71, 23.44) * mm});
            skLineSegment(sketch, "E52.45.37.0", {"start": v(0.71, 23.44) * mm, "end": v(0.58, 23.83) * mm});
            skLineSegment(sketch, "E52.48.37.0", {"start": v(-2.75, 23.29) * mm, "end": v(-2.65, 23.69) * mm});
            skLineSegment(sketch, "E52.51.37.0", {"start": v(-2.82, 22.93) * mm, "end": v(-2.75, 23.29) * mm});
            skLineSegment(sketch, "E52.54.37.0", {"start": v(-2.65, 23.69) * mm, "end": v(-2.51, 24.14) * mm});
            skLineSegment(sketch, "E52.57.37.0", {"start": v(0.93, 22.55) * mm, "end": v(0.88, 22.8) * mm});
            skLineSegment(sketch, "E52.60.37.0", {"start": v(0.95, 22.36) * mm, "end": v(0.93, 22.55) * mm});
            skLineSegment(sketch, "E52.63.37.0", {"start": v(-2.86, 22.63) * mm, "end": v(-2.82, 22.93) * mm});
            skLineSegment(sketch, "E52.66.37.0", {"start": v(-2.89, 22.38) * mm, "end": v(-2.86, 22.63) * mm});
            skLineSegment(sketch, "E52.69.37.0", {"start": v(-2.9, 22.05) * mm, "end": v(-2.9, 22.2) * mm});
            skLineSegment(sketch, "E52.72.37.0", {"start": v(0.97, 22.11) * mm, "end": v(0.97, 22.14) * mm});
            skLineSegment(sketch, "E52.75.37.0", {"start": v(0.97, 22.14) * mm, "end": v(0.96, 22.22) * mm});
            skLineSegment(sketch, "E52.78.37.0", {"start": v(-2.9, 22.2) * mm, "end": v(-2.89, 22.38) * mm});
            skLineSegment(sketch, "E52.81.37.0", {"start": v(0.96, 22.22) * mm, "end": v(0.95, 22.36) * mm});
            skLineSegment(sketch, "E52.84.37.0", {"start": v(-2.9, 21.97) * mm, "end": v(-2.9, 22.05) * mm});
            skLineSegment(sketch, "E52.87.37.0", {"start": v(-2.89, 21.94) * mm, "end": v(-2.9, 21.97) * mm});
            skLineSegment(sketch, "E52.2.38.0", {"start": v(-5.16, 19.24) * mm, "end": v(-5.73, 21.38) * mm});
            skLineSegment(sketch, "E52.3.38.0", {"start": v(-3.39, 25.03) * mm, "end": v(-3.78, 25.53) * mm});
            skLineSegment(sketch, "E52.6.38.0", {"start": v(-1.74, 19.85) * mm, "end": v(-1.93, 22.05) * mm});
            skLineSegment(sketch, "E52.9.38.0", {"start": v(-3.05, 24.56) * mm, "end": v(-3.39, 25.03) * mm});
            skLineSegment(sketch, "E52.12.38.0", {"start": v(-5.53, 24.12) * mm, "end": v(-5.38, 24.68) * mm});
            skLineSegment(sketch, "E52.15.38.0", {"start": v(-5.38, 24.68) * mm, "end": v(-5.18, 25.28) * mm});
            skLineSegment(sketch, "E52.18.38.0", {"start": v(-2.77, 24.11) * mm, "end": v(-3.05, 24.56) * mm});
            skLineSegment(sketch, "E52.21.38.0", {"start": v(-4.23, 26.06) * mm, "end": v(-4.74, 26.6) * mm});
            skLineSegment(sketch, "E52.24.38.0", {"start": v(-2.54, 23.7) * mm, "end": v(-2.77, 24.11) * mm});
            skLineSegment(sketch, "E52.27.38.0", {"start": v(-4.94, 25.93) * mm, "end": v(-4.64, 26.61) * mm});
            skLineSegment(sketch, "E52.30.38.0", {"start": v(-3.78, 25.53) * mm, "end": v(-4.23, 26.06) * mm});
            skLineSegment(sketch, "E52.33.38.0", {"start": v(-5.64, 23.6) * mm, "end": v(-5.53, 24.12) * mm});
            skLineSegment(sketch, "E52.36.38.0", {"start": v(-5.18, 25.28) * mm, "end": v(-4.94, 25.93) * mm});
            skLineSegment(sketch, "E52.39.38.0", {"start": v(-2.1, 22.72) * mm, "end": v(-2.21, 23) * mm});
            skLineSegment(sketch, "E52.42.38.0", {"start": v(-2.21, 23) * mm, "end": v(-2.35, 23.33) * mm});
            skLineSegment(sketch, "E52.45.38.0", {"start": v(-2.35, 23.33) * mm, "end": v(-2.54, 23.7) * mm});
            skLineSegment(sketch, "E52.48.38.0", {"start": v(-5.77, 22.73) * mm, "end": v(-5.72, 23.14) * mm});
            skLineSegment(sketch, "E52.51.38.0", {"start": v(-5.79, 22.37) * mm, "end": v(-5.77, 22.73) * mm});
            skLineSegment(sketch, "E52.54.38.0", {"start": v(-5.72, 23.14) * mm, "end": v(-5.64, 23.6) * mm});
            skLineSegment(sketch, "E52.57.38.0", {"start": v(-2.03, 22.48) * mm, "end": v(-2.1, 22.72) * mm});
            skLineSegment(sketch, "E52.60.38.0", {"start": v(-1.98, 22.3) * mm, "end": v(-2.03, 22.48) * mm});
            skLineSegment(sketch, "E52.63.38.0", {"start": v(-5.8, 22.07) * mm, "end": v(-5.79, 22.37) * mm});
            skLineSegment(sketch, "E52.66.38.0", {"start": v(-5.78, 21.82) * mm, "end": v(-5.8, 22.07) * mm});
            skLineSegment(sketch, "E52.69.38.0", {"start": v(-5.75, 21.49) * mm, "end": v(-5.77, 21.62) * mm});
            skLineSegment(sketch, "E52.72.38.0", {"start": v(-1.93, 22.05) * mm, "end": v(-1.93, 22.08) * mm});
            skLineSegment(sketch, "E52.75.38.0", {"start": v(-1.93, 22.08) * mm, "end": v(-1.95, 22.16) * mm});
            skLineSegment(sketch, "E52.78.38.0", {"start": v(-5.77, 21.62) * mm, "end": v(-5.78, 21.82) * mm});
            skLineSegment(sketch, "E52.81.38.0", {"start": v(-1.95, 22.16) * mm, "end": v(-1.98, 22.3) * mm});
            skLineSegment(sketch, "E52.84.38.0", {"start": v(-5.73, 21.4) * mm, "end": v(-5.75, 21.49) * mm});
            skLineSegment(sketch, "E52.87.38.0", {"start": v(-5.73, 21.38) * mm, "end": v(-5.73, 21.4) * mm});
            skLineSegment(sketch, "E52.2.39.0", {"start": v(-7.62, 18.4) * mm, "end": v(-8.47, 20.45) * mm});
            skLineSegment(sketch, "E52.3.39.0", {"start": v(-6.62, 24.37) * mm, "end": v(-7.08, 24.82) * mm});
            skLineSegment(sketch, "E52.6.39.0", {"start": v(-4.31, 19.45) * mm, "end": v(-4.8, 21.6) * mm});
            skLineSegment(sketch, "E52.9.39.0", {"start": v(-6.23, 23.95) * mm, "end": v(-6.62, 24.37) * mm});
            skLineSegment(sketch, "E52.12.39.0", {"start": v(-8.63, 23.19) * mm, "end": v(-8.56, 23.77) * mm});
            skLineSegment(sketch, "E52.15.39.0", {"start": v(-8.56, 23.77) * mm, "end": v(-8.44, 24.4) * mm});
            skLineSegment(sketch, "E52.18.39.0", {"start": v(-5.9, 23.54) * mm, "end": v(-6.23, 23.95) * mm});
            skLineSegment(sketch, "E52.21.39.0", {"start": v(-7.6, 25.28) * mm, "end": v(-8.18, 25.75) * mm});
            skLineSegment(sketch, "E52.24.39.0", {"start": v(-5.61, 23.17) * mm, "end": v(-5.9, 23.54) * mm});
            skLineSegment(sketch, "E52.27.39.0", {"start": v(-8.28, 25.06) * mm, "end": v(-8.07, 25.78) * mm});
            skLineSegment(sketch, "E52.30.39.0", {"start": v(-7.08, 24.82) * mm, "end": v(-7.6, 25.28) * mm});
            skLineSegment(sketch, "E52.33.39.0", {"start": v(-8.68, 22.67) * mm, "end": v(-8.63, 23.19) * mm});
            skLineSegment(sketch, "E52.36.39.0", {"start": v(-8.44, 24.4) * mm, "end": v(-8.28, 25.06) * mm});
            skLineSegment(sketch, "E52.39.39.0", {"start": v(-5.05, 22.25) * mm, "end": v(-5.2, 22.52) * mm});
            skLineSegment(sketch, "E52.42.39.0", {"start": v(-5.2, 22.52) * mm, "end": v(-5.38, 22.82) * mm});
            skLineSegment(sketch, "E52.45.39.0", {"start": v(-5.38, 22.82) * mm, "end": v(-5.61, 23.17) * mm});
            skLineSegment(sketch, "E52.48.39.0", {"start": v(-8.68, 21.78) * mm, "end": v(-8.7, 22.2) * mm});
            skLineSegment(sketch, "E52.51.39.0", {"start": v(-8.66, 21.42) * mm, "end": v(-8.68, 21.78) * mm});
            skLineSegment(sketch, "E52.54.39.0", {"start": v(-8.7, 22.2) * mm, "end": v(-8.68, 22.67) * mm});
            skLineSegment(sketch, "E52.57.39.0", {"start": v(-4.94, 22.02) * mm, "end": v(-5.05, 22.25) * mm});
            skLineSegment(sketch, "E52.60.39.0", {"start": v(-4.87, 21.84) * mm, "end": v(-4.94, 22.02) * mm});
            skLineSegment(sketch, "E52.63.39.0", {"start": v(-8.62, 21.12) * mm, "end": v(-8.66, 21.42) * mm});
            skLineSegment(sketch, "E52.66.39.0", {"start": v(-8.58, 20.87) * mm, "end": v(-8.62, 21.12) * mm});
            skLineSegment(sketch, "E52.69.39.0", {"start": v(-8.5, 20.55) * mm, "end": v(-8.54, 20.69) * mm});
            skLineSegment(sketch, "E52.72.39.0", {"start": v(-4.8, 21.6) * mm, "end": v(-4.8, 21.63) * mm});
            skLineSegment(sketch, "E52.75.39.0", {"start": v(-4.8, 21.63) * mm, "end": v(-4.82, 21.71) * mm});
            skLineSegment(sketch, "E52.78.39.0", {"start": v(-8.54, 20.69) * mm, "end": v(-8.58, 20.87) * mm});
            skLineSegment(sketch, "E52.81.39.0", {"start": v(-4.82, 21.71) * mm, "end": v(-4.87, 21.84) * mm});
            skLineSegment(sketch, "E52.84.39.0", {"start": v(-8.48, 20.47) * mm, "end": v(-8.5, 20.55) * mm});
            skLineSegment(sketch, "E52.87.39.0", {"start": v(-8.47, 20.45) * mm, "end": v(-8.48, 20.47) * mm});
            skLineSegment(sketch, "E52.2.40.0", {"start": v(-9.96, 17.25) * mm, "end": v(-11.07, 19.17) * mm});
            skLineSegment(sketch, "E52.3.40.0", {"start": v(-9.75, 23.3) * mm, "end": v(-10.26, 23.68) * mm});
            skLineSegment(sketch, "E52.6.40.0", {"start": v(-6.81, 18.72) * mm, "end": v(-7.57, 20.8) * mm});
            skLineSegment(sketch, "E52.9.40.0", {"start": v(-9.3, 22.93) * mm, "end": v(-9.75, 23.3) * mm});
            skLineSegment(sketch, "E52.12.40.0", {"start": v(-11.59, 21.86) * mm, "end": v(-11.58, 22.45) * mm});
            skLineSegment(sketch, "E52.15.40.0", {"start": v(-11.58, 22.45) * mm, "end": v(-11.55, 23.08) * mm});
            skLineSegment(sketch, "E52.18.40.0", {"start": v(-8.92, 22.57) * mm, "end": v(-9.3, 22.93) * mm});
            skLineSegment(sketch, "E52.21.40.0", {"start": v(-10.83, 24.07) * mm, "end": v(-11.47, 24.46) * mm});
            skLineSegment(sketch, "E52.24.40.0", {"start": v(-8.59, 22.24) * mm, "end": v(-8.92, 22.57) * mm});
            skLineSegment(sketch, "E52.27.40.0", {"start": v(-11.48, 23.77) * mm, "end": v(-11.37, 24.5) * mm});
            skLineSegment(sketch, "E52.30.40.0", {"start": v(-10.26, 23.68) * mm, "end": v(-10.83, 24.07) * mm});
            skLineSegment(sketch, "E52.33.40.0", {"start": v(-11.56, 21.34) * mm, "end": v(-11.59, 21.86) * mm});
            skLineSegment(sketch, "E52.36.40.0", {"start": v(-11.55, 23.08) * mm, "end": v(-11.48, 23.77) * mm});
            skLineSegment(sketch, "E52.39.40.0", {"start": v(-7.91, 21.4) * mm, "end": v(-8.09, 21.64) * mm});
            skLineSegment(sketch, "E52.42.40.0", {"start": v(-8.09, 21.64) * mm, "end": v(-8.31, 21.93) * mm});
            skLineSegment(sketch, "E52.45.40.0", {"start": v(-8.31, 21.93) * mm, "end": v(-8.59, 22.24) * mm});
            skLineSegment(sketch, "E52.48.40.0", {"start": v(-11.45, 20.46) * mm, "end": v(-11.51, 20.87) * mm});
            skLineSegment(sketch, "E52.51.40.0", {"start": v(-11.38, 20.1) * mm, "end": v(-11.45, 20.46) * mm});
            skLineSegment(sketch, "E52.54.40.0", {"start": v(-11.51, 20.87) * mm, "end": v(-11.56, 21.34) * mm});
            skLineSegment(sketch, "E52.57.40.0", {"start": v(-7.77, 21.19) * mm, "end": v(-7.91, 21.4) * mm});
            skLineSegment(sketch, "E52.60.40.0", {"start": v(-7.68, 21.02) * mm, "end": v(-7.77, 21.19) * mm});
            skLineSegment(sketch, "E52.63.40.0", {"start": v(-11.3, 19.81) * mm, "end": v(-11.38, 20.1) * mm});
            skLineSegment(sketch, "E52.66.40.0", {"start": v(-11.23, 19.58) * mm, "end": v(-11.3, 19.81) * mm});
            skLineSegment(sketch, "E52.69.40.0", {"start": v(-11.11, 19.27) * mm, "end": v(-11.17, 19.4) * mm});
            skLineSegment(sketch, "E52.72.40.0", {"start": v(-7.57, 20.8) * mm, "end": v(-7.58, 20.82) * mm});
            skLineSegment(sketch, "E52.75.40.0", {"start": v(-7.58, 20.82) * mm, "end": v(-7.61, 20.9) * mm});
            skLineSegment(sketch, "E52.78.40.0", {"start": v(-11.17, 19.4) * mm, "end": v(-11.23, 19.58) * mm});
            skLineSegment(sketch, "E52.81.40.0", {"start": v(-7.61, 20.9) * mm, "end": v(-7.68, 21.02) * mm});
            skLineSegment(sketch, "E52.84.40.0", {"start": v(-11.08, 19.2) * mm, "end": v(-11.11, 19.27) * mm});
            skLineSegment(sketch, "E52.87.40.0", {"start": v(-11.07, 19.17) * mm, "end": v(-11.08, 19.2) * mm});
            skLineSegment(sketch, "E52.2.41.0", {"start": v(-12.13, 15.8) * mm, "end": v(-13.47, 17.56) * mm});
            skLineSegment(sketch, "E52.3.41.0", {"start": v(-12.7, 21.83) * mm, "end": v(-13.26, 22.14) * mm});
            skLineSegment(sketch, "E52.6.41.0", {"start": v(-9.2, 17.67) * mm, "end": v(-10.22, 19.63) * mm});
            skLineSegment(sketch, "E52.9.41.0", {"start": v(-12.22, 21.52) * mm, "end": v(-12.7, 21.83) * mm});
            skLineSegment(sketch, "E52.12.41.0", {"start": v(-14.34, 20.17) * mm, "end": v(-14.41, 20.74) * mm});
            skLineSegment(sketch, "E52.15.41.0", {"start": v(-14.41, 20.74) * mm, "end": v(-14.46, 21.38) * mm});
            skLineSegment(sketch, "E52.18.41.0", {"start": v(-11.79, 21.22) * mm, "end": v(-12.22, 21.52) * mm});
            skLineSegment(sketch, "E52.21.41.0", {"start": v(-13.88, 22.45) * mm, "end": v(-14.56, 22.76) * mm});
            skLineSegment(sketch, "E52.24.41.0", {"start": v(-11.42, 20.92) * mm, "end": v(-11.79, 21.22) * mm});
            skLineSegment(sketch, "E52.27.41.0", {"start": v(-14.49, 22.07) * mm, "end": v(-14.47, 22.81) * mm});
            skLineSegment(sketch, "E52.30.41.0", {"start": v(-13.26, 22.14) * mm, "end": v(-13.88, 22.45) * mm});
            skLineSegment(sketch, "E52.33.41.0", {"start": v(-14.25, 19.65) * mm, "end": v(-14.34, 20.17) * mm});
            skLineSegment(sketch, "E52.36.41.0", {"start": v(-14.46, 21.38) * mm, "end": v(-14.49, 22.07) * mm});
            skLineSegment(sketch, "E52.39.41.0", {"start": v(-10.64, 20.18) * mm, "end": v(-10.84, 20.4) * mm});
            skLineSegment(sketch, "E52.42.41.0", {"start": v(-10.84, 20.4) * mm, "end": v(-11.1, 20.65) * mm});
            skLineSegment(sketch, "E52.45.41.0", {"start": v(-11.1, 20.65) * mm, "end": v(-11.42, 20.92) * mm});
            skLineSegment(sketch, "E52.48.41.0", {"start": v(-14.03, 18.8) * mm, "end": v(-14.14, 19.2) * mm});
            skLineSegment(sketch, "E52.51.41.0", {"start": v(-13.9, 18.45) * mm, "end": v(-14.03, 18.8) * mm});
            skLineSegment(sketch, "E52.54.41.0", {"start": v(-14.14, 19.2) * mm, "end": v(-14.25, 19.65) * mm});
            skLineSegment(sketch, "E52.57.41.0", {"start": v(-10.47, 20) * mm, "end": v(-10.64, 20.18) * mm});
            skLineSegment(sketch, "E52.60.41.0", {"start": v(-10.36, 19.84) * mm, "end": v(-10.47, 20) * mm});
            skLineSegment(sketch, "E52.63.41.0", {"start": v(-13.8, 18.17) * mm, "end": v(-13.9, 18.45) * mm});
            skLineSegment(sketch, "E52.66.41.0", {"start": v(-13.7, 17.94) * mm, "end": v(-13.8, 18.17) * mm});
            skLineSegment(sketch, "E52.69.41.0", {"start": v(-13.53, 17.65) * mm, "end": v(-13.6, 17.77) * mm});
            skLineSegment(sketch, "E52.72.41.0", {"start": v(-10.22, 19.63) * mm, "end": v(-10.23, 19.66) * mm});
            skLineSegment(sketch, "E52.75.41.0", {"start": v(-10.23, 19.66) * mm, "end": v(-10.28, 19.73) * mm});
            skLineSegment(sketch, "E52.78.41.0", {"start": v(-13.6, 17.77) * mm, "end": v(-13.7, 17.94) * mm});
            skLineSegment(sketch, "E52.81.41.0", {"start": v(-10.28, 19.73) * mm, "end": v(-10.36, 19.84) * mm});
            skLineSegment(sketch, "E52.84.41.0", {"start": v(-13.49, 17.58) * mm, "end": v(-13.53, 17.65) * mm});
            skLineSegment(sketch, "E52.87.41.0", {"start": v(-13.47, 17.56) * mm, "end": v(-13.49, 17.58) * mm});
            skLineSegment(sketch, "E52.2.42.0", {"start": v(-14.09, 14.09) * mm, "end": v(-15.65, 15.65) * mm});
            skLineSegment(sketch, "E52.3.42.0", {"start": v(-15.45, 19.98) * mm, "end": v(-16.04, 20.22) * mm});
            skLineSegment(sketch, "E52.6.42.0", {"start": v(-11.43, 16.32) * mm, "end": v(-12.7, 18.13) * mm});
            skLineSegment(sketch, "E52.9.42.0", {"start": v(-14.92, 19.74) * mm, "end": v(-15.45, 19.98) * mm});
            skLineSegment(sketch, "E52.12.42.0", {"start": v(-16.85, 18.12) * mm, "end": v(-17, 18.68) * mm});
            skLineSegment(sketch, "E52.15.42.0", {"start": v(-17, 18.68) * mm, "end": v(-17.13, 19.3) * mm});
            skLineSegment(sketch, "E52.18.42.0", {"start": v(-14.45, 19.5) * mm, "end": v(-14.92, 19.74) * mm});
            skLineSegment(sketch, "E52.21.42.0", {"start": v(-16.69, 20.45) * mm, "end": v(-17.4, 20.66) * mm});
            skLineSegment(sketch, "E52.24.42.0", {"start": v(-14.05, 19.26) * mm, "end": v(-14.45, 19.5) * mm});
            skLineSegment(sketch, "E52.27.42.0", {"start": v(-17.24, 19.99) * mm, "end": v(-17.32, 20.73) * mm});
            skLineSegment(sketch, "E52.30.42.0", {"start": v(-16.04, 20.22) * mm, "end": v(-16.69, 20.45) * mm});
            skLineSegment(sketch, "E52.33.42.0", {"start": v(-16.69, 17.62) * mm, "end": v(-16.85, 18.12) * mm});
            skLineSegment(sketch, "E52.36.42.0", {"start": v(-17.13, 19.3) * mm, "end": v(-17.24, 19.99) * mm});
            skLineSegment(sketch, "E52.39.42.0", {"start": v(-13.18, 18.62) * mm, "end": v(-13.41, 18.81) * mm});
            skLineSegment(sketch, "E52.42.42.0", {"start": v(-13.41, 18.81) * mm, "end": v(-13.7, 19.03) * mm});
            skLineSegment(sketch, "E52.45.42.0", {"start": v(-13.7, 19.03) * mm, "end": v(-14.05, 19.26) * mm});
            skLineSegment(sketch, "E52.48.42.0", {"start": v(-16.36, 16.8) * mm, "end": v(-16.52, 17.18) * mm});
            skLineSegment(sketch, "E52.51.42.0", {"start": v(-16.2, 16.48) * mm, "end": v(-16.36, 16.8) * mm});
            skLineSegment(sketch, "E52.54.42.0", {"start": v(-16.52, 17.18) * mm, "end": v(-16.69, 17.62) * mm});
            skLineSegment(sketch, "E52.57.42.0", {"start": v(-13, 18.45) * mm, "end": v(-13.18, 18.62) * mm});
            skLineSegment(sketch, "E52.60.42.0", {"start": v(-12.86, 18.32) * mm, "end": v(-13, 18.45) * mm});
            skLineSegment(sketch, "E52.63.42.0", {"start": v(-16.05, 16.21) * mm, "end": v(-16.2, 16.48) * mm});
            skLineSegment(sketch, "E52.66.42.0", {"start": v(-15.92, 16) * mm, "end": v(-16.05, 16.21) * mm});
            skLineSegment(sketch, "E52.69.42.0", {"start": v(-15.72, 15.73) * mm, "end": v(-15.8, 15.84) * mm});
            skLineSegment(sketch, "E52.72.42.0", {"start": v(-12.7, 18.13) * mm, "end": v(-12.71, 18.15) * mm});
            skLineSegment(sketch, "E52.75.42.0", {"start": v(-12.71, 18.15) * mm, "end": v(-12.76, 18.22) * mm});
            skLineSegment(sketch, "E52.78.42.0", {"start": v(-15.8, 15.84) * mm, "end": v(-15.92, 16) * mm});
            skLineSegment(sketch, "E52.81.42.0", {"start": v(-12.76, 18.22) * mm, "end": v(-12.86, 18.32) * mm});
            skLineSegment(sketch, "E52.84.42.0", {"start": v(-15.67, 15.67) * mm, "end": v(-15.72, 15.73) * mm});
            skLineSegment(sketch, "E52.87.42.0", {"start": v(-15.65, 15.65) * mm, "end": v(-15.67, 15.67) * mm});
            skLineSegment(sketch, "E52.2.43.0", {"start": v(-15.8, 12.13) * mm, "end": v(-17.56, 13.47) * mm});
            skLineSegment(sketch, "E52.3.43.0", {"start": v(-17.92, 17.8) * mm, "end": v(-18.54, 17.96) * mm});
            skLineSegment(sketch, "E52.6.43.0", {"start": v(-13.46, 14.69) * mm, "end": v(-14.95, 16.32) * mm});
            skLineSegment(sketch, "E52.9.43.0", {"start": v(-17.37, 17.62) * mm, "end": v(-17.92, 17.8) * mm});
            skLineSegment(sketch, "E52.12.43.0", {"start": v(-19.07, 15.77) * mm, "end": v(-19.3, 16.3) * mm});
            skLineSegment(sketch, "E52.15.43.0", {"start": v(-19.3, 16.3) * mm, "end": v(-19.5, 16.9) * mm});
            skLineSegment(sketch, "E52.18.43.0", {"start": v(-16.88, 17.44) * mm, "end": v(-17.37, 17.62) * mm});
            skLineSegment(sketch, "E52.21.43.0", {"start": v(-19.22, 18.1) * mm, "end": v(-19.95, 18.21) * mm});
            skLineSegment(sketch, "E52.24.43.0", {"start": v(-16.44, 17.26) * mm, "end": v(-16.88, 17.44) * mm});
            skLineSegment(sketch, "E52.27.43.0", {"start": v(-19.7, 17.57) * mm, "end": v(-19.88, 18.3) * mm});
            skLineSegment(sketch, "E52.30.43.0", {"start": v(-18.54, 17.96) * mm, "end": v(-19.22, 18.1) * mm});
            skLineSegment(sketch, "E52.33.43.0", {"start": v(-18.85, 15.3) * mm, "end": v(-19.07, 15.77) * mm});
            skLineSegment(sketch, "E52.36.43.0", {"start": v(-19.5, 16.9) * mm, "end": v(-19.7, 17.57) * mm});
            skLineSegment(sketch, "E52.39.43.0", {"start": v(-15.5, 16.74) * mm, "end": v(-15.76, 16.9) * mm});
            skLineSegment(sketch, "E52.42.43.0", {"start": v(-15.76, 16.9) * mm, "end": v(-16.07, 17.08) * mm});
            skLineSegment(sketch, "E52.45.43.0", {"start": v(-16.07, 17.08) * mm, "end": v(-16.44, 17.26) * mm});
            skLineSegment(sketch, "E52.48.43.0", {"start": v(-18.41, 14.52) * mm, "end": v(-18.62, 14.88) * mm});
            skLineSegment(sketch, "E52.51.43.0", {"start": v(-18.21, 14.22) * mm, "end": v(-18.41, 14.52) * mm});
            skLineSegment(sketch, "E52.54.43.0", {"start": v(-18.62, 14.88) * mm, "end": v(-18.85, 15.3) * mm});
            skLineSegment(sketch, "E52.57.43.0", {"start": v(-15.3, 16.6) * mm, "end": v(-15.5, 16.74) * mm});
            skLineSegment(sketch, "E52.60.43.0", {"start": v(-15.14, 16.48) * mm, "end": v(-15.3, 16.6) * mm});
            skLineSegment(sketch, "E52.63.43.0", {"start": v(-18.03, 13.98) * mm, "end": v(-18.21, 14.22) * mm});
            skLineSegment(sketch, "E52.66.43.0", {"start": v(-17.87, 13.79) * mm, "end": v(-18.03, 13.98) * mm});
            skLineSegment(sketch, "E52.69.43.0", {"start": v(-17.64, 13.55) * mm, "end": v(-17.74, 13.64) * mm});
            skLineSegment(sketch, "E52.72.43.0", {"start": v(-14.95, 16.32) * mm, "end": v(-14.97, 16.34) * mm});
            skLineSegment(sketch, "E52.75.43.0", {"start": v(-14.97, 16.34) * mm, "end": v(-15.03, 16.4) * mm});
            skLineSegment(sketch, "E52.78.43.0", {"start": v(-17.74, 13.64) * mm, "end": v(-17.87, 13.79) * mm});
            skLineSegment(sketch, "E52.81.43.0", {"start": v(-15.03, 16.4) * mm, "end": v(-15.14, 16.48) * mm});
            skLineSegment(sketch, "E52.84.43.0", {"start": v(-17.58, 13.5) * mm, "end": v(-17.64, 13.55) * mm});
            skLineSegment(sketch, "E52.87.43.0", {"start": v(-17.56, 13.47) * mm, "end": v(-17.58, 13.5) * mm});
            skLineSegment(sketch, "E52.2.44.0", {"start": v(-17.25, 9.96) * mm, "end": v(-19.17, 11.07) * mm});
            skLineSegment(sketch, "E52.3.44.0", {"start": v(-20.1, 15.3) * mm, "end": v(-20.72, 15.38) * mm});
            skLineSegment(sketch, "E52.6.44.0", {"start": v(-15.26, 12.8) * mm, "end": v(-16.95, 14.23) * mm});
            skLineSegment(sketch, "E52.9.44.0", {"start": v(-19.52, 15.2) * mm, "end": v(-20.1, 15.3) * mm});
            skLineSegment(sketch, "E52.12.44.0", {"start": v(-20.97, 13.14) * mm, "end": v(-21.25, 13.65) * mm});
            skLineSegment(sketch, "E52.15.44.0", {"start": v(-21.25, 13.65) * mm, "end": v(-21.54, 14.21) * mm});
            skLineSegment(sketch, "E52.18.44.0", {"start": v(-19, 15.09) * mm, "end": v(-19.52, 15.2) * mm});
            skLineSegment(sketch, "E52.21.44.0", {"start": v(-21.41, 15.43) * mm, "end": v(-22.16, 15.45) * mm});
            skLineSegment(sketch, "E52.24.44.0", {"start": v(-18.56, 14.96) * mm, "end": v(-19, 15.09) * mm});
            skLineSegment(sketch, "E52.27.44.0", {"start": v(-21.83, 14.84) * mm, "end": v(-22.1, 15.54) * mm});
            skLineSegment(sketch, "E52.30.44.0", {"start": v(-20.72, 15.38) * mm, "end": v(-21.41, 15.43) * mm});
            skLineSegment(sketch, "E52.33.44.0", {"start": v(-20.68, 12.7) * mm, "end": v(-20.97, 13.14) * mm});
            skLineSegment(sketch, "E52.36.44.0", {"start": v(-21.54, 14.21) * mm, "end": v(-21.83, 14.84) * mm});
            skLineSegment(sketch, "E52.39.44.0", {"start": v(-17.55, 14.58) * mm, "end": v(-17.83, 14.7) * mm});
            skLineSegment(sketch, "E52.42.44.0", {"start": v(-17.83, 14.7) * mm, "end": v(-18.16, 14.83) * mm});
            skLineSegment(sketch, "E52.45.44.0", {"start": v(-18.16, 14.83) * mm, "end": v(-18.56, 14.96) * mm});
            skLineSegment(sketch, "E52.48.44.0", {"start": v(-20.15, 12) * mm, "end": v(-20.4, 12.32) * mm});
            skLineSegment(sketch, "E52.51.44.0", {"start": v(-19.91, 11.72) * mm, "end": v(-20.15, 12) * mm});
            skLineSegment(sketch, "E52.54.44.0", {"start": v(-20.4, 12.32) * mm, "end": v(-20.68, 12.7) * mm});
            skLineSegment(sketch, "E52.57.44.0", {"start": v(-17.33, 14.46) * mm, "end": v(-17.55, 14.58) * mm});
            skLineSegment(sketch, "E52.60.44.0", {"start": v(-17.16, 14.37) * mm, "end": v(-17.33, 14.46) * mm});
            skLineSegment(sketch, "E52.63.44.0", {"start": v(-19.7, 11.5) * mm, "end": v(-19.91, 11.72) * mm});
            skLineSegment(sketch, "E52.66.44.0", {"start": v(-19.52, 11.34) * mm, "end": v(-19.7, 11.5) * mm});
            skLineSegment(sketch, "E52.69.44.0", {"start": v(-19.26, 11.13) * mm, "end": v(-19.37, 11.21) * mm});
            skLineSegment(sketch, "E52.72.44.0", {"start": v(-16.95, 14.23) * mm, "end": v(-16.98, 14.24) * mm});
            skLineSegment(sketch, "E52.75.44.0", {"start": v(-16.98, 14.24) * mm, "end": v(-17.04, 14.3) * mm});
            skLineSegment(sketch, "E52.78.44.0", {"start": v(-19.37, 11.21) * mm, "end": v(-19.52, 11.34) * mm});
            skLineSegment(sketch, "E52.81.44.0", {"start": v(-17.04, 14.3) * mm, "end": v(-17.16, 14.37) * mm});
            skLineSegment(sketch, "E52.84.44.0", {"start": v(-19.2, 11.08) * mm, "end": v(-19.26, 11.13) * mm});
            skLineSegment(sketch, "E52.87.44.0", {"start": v(-19.17, 11.07) * mm, "end": v(-19.2, 11.08) * mm});
            skLineSegment(sketch, "E52.2.45.0", {"start": v(-18.4, 7.62) * mm, "end": v(-20.45, 8.47) * mm});
            skLineSegment(sketch, "E52.3.45.0", {"start": v(-21.92, 12.55) * mm, "end": v(-22.56, 12.55) * mm});
            skLineSegment(sketch, "E52.6.45.0", {"start": v(-16.8, 10.7) * mm, "end": v(-18.67, 11.9) * mm});
            skLineSegment(sketch, "E52.9.45.0", {"start": v(-21.34, 12.53) * mm, "end": v(-21.92, 12.55) * mm});
            skLineSegment(sketch, "E52.12.45.0", {"start": v(-22.5, 10.3) * mm, "end": v(-22.85, 10.76) * mm});
            skLineSegment(sketch, "E52.15.45.0", {"start": v(-22.85, 10.76) * mm, "end": v(-23.21, 11.28) * mm});
            skLineSegment(sketch, "E52.18.45.0", {"start": v(-20.82, 12.48) * mm, "end": v(-21.34, 12.53) * mm});
            skLineSegment(sketch, "E52.21.45.0", {"start": v(-23.25, 12.5) * mm, "end": v(-23.99, 12.43) * mm});
            skLineSegment(sketch, "E52.24.45.0", {"start": v(-20.35, 12.41) * mm, "end": v(-20.82, 12.48) * mm});
            skLineSegment(sketch, "E52.27.45.0", {"start": v(-23.58, 11.87) * mm, "end": v(-23.94, 12.52) * mm});
            skLineSegment(sketch, "E52.30.45.0", {"start": v(-22.56, 12.55) * mm, "end": v(-23.25, 12.5) * mm});
            skLineSegment(sketch, "E52.33.45.0", {"start": v(-22.16, 9.9) * mm, "end": v(-22.5, 10.3) * mm});
            skLineSegment(sketch, "E52.36.45.0", {"start": v(-23.21, 11.28) * mm, "end": v(-23.58, 11.87) * mm});
            skLineSegment(sketch, "E52.39.45.0", {"start": v(-19.3, 12.16) * mm, "end": v(-19.6, 12.25) * mm});
            skLineSegment(sketch, "E52.42.45.0", {"start": v(-19.6, 12.25) * mm, "end": v(-19.94, 12.33) * mm});
            skLineSegment(sketch, "E52.45.45.0", {"start": v(-19.94, 12.33) * mm, "end": v(-20.35, 12.41) * mm});
            skLineSegment(sketch, "E52.48.45.0", {"start": v(-21.54, 9.26) * mm, "end": v(-21.84, 9.55) * mm});
            skLineSegment(sketch, "E52.51.45.0", {"start": v(-21.27, 9.02) * mm, "end": v(-21.54, 9.26) * mm});
            skLineSegment(sketch, "E52.54.45.0", {"start": v(-21.84, 9.55) * mm, "end": v(-22.16, 9.9) * mm});
            skLineSegment(sketch, "E52.57.45.0", {"start": v(-19.07, 12.08) * mm, "end": v(-19.3, 12.16) * mm});
            skLineSegment(sketch, "E52.60.45.0", {"start": v(-18.89, 12) * mm, "end": v(-19.07, 12.08) * mm});
            skLineSegment(sketch, "E52.63.45.0", {"start": v(-21.03, 8.84) * mm, "end": v(-21.27, 9.02) * mm});
            skLineSegment(sketch, "E52.66.45.0", {"start": v(-20.83, 8.7) * mm, "end": v(-21.03, 8.84) * mm});
            skLineSegment(sketch, "E52.69.45.0", {"start": v(-20.55, 8.52) * mm, "end": v(-20.67, 8.59) * mm});
            skLineSegment(sketch, "E52.72.45.0", {"start": v(-18.67, 11.9) * mm, "end": v(-18.69, 11.9) * mm});
            skLineSegment(sketch, "E52.75.45.0", {"start": v(-18.69, 11.9) * mm, "end": v(-18.76, 11.94) * mm});
            skLineSegment(sketch, "E52.78.45.0", {"start": v(-20.67, 8.59) * mm, "end": v(-20.83, 8.7) * mm});
            skLineSegment(sketch, "E52.81.45.0", {"start": v(-18.76, 11.94) * mm, "end": v(-18.89, 12) * mm});
            skLineSegment(sketch, "E52.84.45.0", {"start": v(-20.47, 8.48) * mm, "end": v(-20.55, 8.52) * mm});
            skLineSegment(sketch, "E52.87.45.0", {"start": v(-20.45, 8.47) * mm, "end": v(-20.47, 8.48) * mm});
            skLineSegment(sketch, "E52.2.46.0", {"start": v(-19.24, 5.16) * mm, "end": v(-21.38, 5.73) * mm});
            skLineSegment(sketch, "E52.3.46.0", {"start": v(-23.37, 9.58) * mm, "end": v(-24, 9.5) * mm});
            skLineSegment(sketch, "E52.6.46.0", {"start": v(-18.05, 8.42) * mm, "end": v(-20.06, 9.35) * mm});
            skLineSegment(sketch, "E52.9.46.0", {"start": v(-22.8, 9.64) * mm, "end": v(-23.37, 9.58) * mm});
            skLineSegment(sketch, "E52.12.46.0", {"start": v(-23.65, 7.27) * mm, "end": v(-24.06, 7.68) * mm});
            skLineSegment(sketch, "E52.15.46.0", {"start": v(-24.06, 7.68) * mm, "end": v(-24.49, 8.15) * mm});
            skLineSegment(sketch, "E52.18.46.0", {"start": v(-22.27, 9.66) * mm, "end": v(-22.8, 9.64) * mm});
            skLineSegment(sketch, "E52.21.46.0", {"start": v(-24.68, 9.37) * mm, "end": v(-25.4, 9.19) * mm});
            skLineSegment(sketch, "E52.24.46.0", {"start": v(-21.8, 9.65) * mm, "end": v(-22.27, 9.66) * mm});
            skLineSegment(sketch, "E52.27.46.0", {"start": v(-24.93, 8.69) * mm, "end": v(-25.37, 9.3) * mm});
            skLineSegment(sketch, "E52.30.46.0", {"start": v(-24, 9.5) * mm, "end": v(-24.68, 9.37) * mm});
            skLineSegment(sketch, "E52.33.46.0", {"start": v(-23.26, 6.92) * mm, "end": v(-23.65, 7.27) * mm});
            skLineSegment(sketch, "E52.36.46.0", {"start": v(-24.49, 8.15) * mm, "end": v(-24.93, 8.69) * mm});
            skLineSegment(sketch, "E52.39.46.0", {"start": v(-20.72, 9.54) * mm, "end": v(-21.02, 9.59) * mm});
            skLineSegment(sketch, "E52.42.46.0", {"start": v(-21.02, 9.59) * mm, "end": v(-21.38, 9.63) * mm});
            skLineSegment(sketch, "E52.45.46.0", {"start": v(-21.38, 9.63) * mm, "end": v(-21.8, 9.65) * mm});
            skLineSegment(sketch, "E52.48.46.0", {"start": v(-22.57, 6.37) * mm, "end": v(-22.9, 6.62) * mm});
            skLineSegment(sketch, "E52.51.46.0", {"start": v(-22.27, 6.17) * mm, "end": v(-22.57, 6.37) * mm});
            skLineSegment(sketch, "E52.54.46.0", {"start": v(-22.9, 6.62) * mm, "end": v(-23.26, 6.92) * mm});
            skLineSegment(sketch, "E52.57.46.0", {"start": v(-20.48, 9.49) * mm, "end": v(-20.72, 9.54) * mm});
            skLineSegment(sketch, "E52.60.46.0", {"start": v(-20.3, 9.44) * mm, "end": v(-20.48, 9.49) * mm});
            skLineSegment(sketch, "E52.63.46.0", {"start": v(-22, 6.02) * mm, "end": v(-22.27, 6.17) * mm});
            skLineSegment(sketch, "E52.66.46.0", {"start": v(-21.79, 5.9) * mm, "end": v(-22, 6.02) * mm});
            skLineSegment(sketch, "E52.69.46.0", {"start": v(-21.48, 5.76) * mm, "end": v(-21.61, 5.82) * mm});
            skLineSegment(sketch, "E52.72.46.0", {"start": v(-20.06, 9.35) * mm, "end": v(-20.08, 9.36) * mm});
            skLineSegment(sketch, "E52.75.46.0", {"start": v(-20.08, 9.36) * mm, "end": v(-20.16, 9.4) * mm});
            skLineSegment(sketch, "E52.78.46.0", {"start": v(-21.61, 5.82) * mm, "end": v(-21.79, 5.9) * mm});
            skLineSegment(sketch, "E52.81.46.0", {"start": v(-20.16, 9.4) * mm, "end": v(-20.3, 9.44) * mm});
            skLineSegment(sketch, "E52.84.46.0", {"start": v(-21.4, 5.74) * mm, "end": v(-21.48, 5.76) * mm});
            skLineSegment(sketch, "E52.87.46.0", {"start": v(-21.38, 5.73) * mm, "end": v(-21.4, 5.74) * mm});
            skLineSegment(sketch, "E52.2.47.0", {"start": v(-19.75, 2.6) * mm, "end": v(-21.94, 2.89) * mm});
            skLineSegment(sketch, "E52.3.47.0", {"start": v(-24.42, 6.45) * mm, "end": v(-25.03, 6.28) * mm});
            skLineSegment(sketch, "E52.6.47.0", {"start": v(-19, 6) * mm, "end": v(-21.1, 6.66) * mm});
            skLineSegment(sketch, "E52.9.47.0", {"start": v(-23.85, 6.58) * mm, "end": v(-24.42, 6.45) * mm});
            skLineSegment(sketch, "E52.12.47.0", {"start": v(-24.4, 4.12) * mm, "end": v(-24.86, 4.47) * mm});
            skLineSegment(sketch, "E52.15.47.0", {"start": v(-24.86, 4.47) * mm, "end": v(-25.34, 4.89) * mm});
            skLineSegment(sketch, "E52.18.47.0", {"start": v(-23.34, 6.67) * mm, "end": v(-23.85, 6.58) * mm});
            skLineSegment(sketch, "E52.21.47.0", {"start": v(-25.7, 6.06) * mm, "end": v(-26.39, 5.8) * mm});
            skLineSegment(sketch, "E52.24.47.0", {"start": v(-22.87, 6.72) * mm, "end": v(-23.34, 6.67) * mm});
            skLineSegment(sketch, "E52.27.47.0", {"start": v(-25.85, 5.36) * mm, "end": v(-26.36, 5.9) * mm});
            skLineSegment(sketch, "E52.30.47.0", {"start": v(-25.03, 6.28) * mm, "end": v(-25.7, 6.06) * mm});
            skLineSegment(sketch, "E52.33.47.0", {"start": v(-23.97, 3.82) * mm, "end": v(-24.4, 4.12) * mm});
            skLineSegment(sketch, "E52.36.47.0", {"start": v(-25.34, 4.89) * mm, "end": v(-25.85, 5.36) * mm});
            skLineSegment(sketch, "E52.39.47.0", {"start": v(-21.8, 6.75) * mm, "end": v(-22.1, 6.76) * mm});
            skLineSegment(sketch, "E52.42.47.0", {"start": v(-22.1, 6.76) * mm, "end": v(-22.45, 6.75) * mm});
            skLineSegment(sketch, "E52.45.47.0", {"start": v(-22.45, 6.75) * mm, "end": v(-22.87, 6.72) * mm});
            skLineSegment(sketch, "E52.48.47.0", {"start": v(-23.2, 3.37) * mm, "end": v(-23.57, 3.57) * mm});
            skLineSegment(sketch, "E52.51.47.0", {"start": v(-22.88, 3.21) * mm, "end": v(-23.2, 3.37) * mm});
            skLineSegment(sketch, "E52.54.47.0", {"start": v(-23.57, 3.57) * mm, "end": v(-23.97, 3.82) * mm});
            skLineSegment(sketch, "E52.57.47.0", {"start": v(-21.54, 6.73) * mm, "end": v(-21.8, 6.75) * mm});
            skLineSegment(sketch, "E52.60.47.0", {"start": v(-21.35, 6.7) * mm, "end": v(-21.54, 6.73) * mm});
            skLineSegment(sketch, "E52.63.47.0", {"start": v(-22.6, 3.1) * mm, "end": v(-22.88, 3.21) * mm});
            skLineSegment(sketch, "E52.66.47.0", {"start": v(-22.37, 3) * mm, "end": v(-22.6, 3.1) * mm});
            skLineSegment(sketch, "E52.69.47.0", {"start": v(-22.05, 2.91) * mm, "end": v(-22.18, 2.95) * mm});
            skLineSegment(sketch, "E52.72.47.0", {"start": v(-21.1, 6.66) * mm, "end": v(-21.13, 6.66) * mm});
            skLineSegment(sketch, "E52.75.47.0", {"start": v(-21.13, 6.66) * mm, "end": v(-21.22, 6.68) * mm});
            skLineSegment(sketch, "E52.78.47.0", {"start": v(-22.18, 2.95) * mm, "end": v(-22.37, 3) * mm});
            skLineSegment(sketch, "E52.81.47.0", {"start": v(-21.22, 6.68) * mm, "end": v(-21.35, 6.7) * mm});
            skLineSegment(sketch, "E52.84.47.0", {"start": v(-21.97, 2.9) * mm, "end": v(-22.05, 2.91) * mm});
            skLineSegment(sketch, "E52.87.47.0", {"start": v(-21.94, 2.89) * mm, "end": v(-21.97, 2.9) * mm});
            skSolve(sketch);
        }
        {
            var Q0;
            {var subQ0=sQuery(id+"F1.wireOp",EDGE,"E0");var subQ27=makeQuery(id+"F1.imprint","INTERSECT",VERTEX,{"derivedFrom":[subQ0,sQuery(id+"F1.wireOp",EDGE,"E51.10.0")]});Q0=makeQuery(id+"F1.imprint","IMPRINT",FACE,{"disambiguationData":[TD([[makeQuery(id+"F1.imprint","IMPRINT",EDGE,{"disambiguationData":[TD([[subQ27,-1.0]])],"derivedFrom":subQ0}),1.0]])]});}
            var Q1;
            {var subQ0=sQuery(id+"F1.wireOp",EDGE,"E51.1.0");Q1=makeQuery(id+"F1.imprint","IMPRINT",FACE,{"disambiguationData":[TD([[makeQuery(id+"F1.imprint","IMPRINT",EDGE,{"derivedFrom":subQ0}),-1.0]])]});}
            var Q2;
            {var subQ7=sQuery(id+"F1.wireOp",EDGE,"E51.2.0");Q2=makeQuery(id+"F1.imprint","IMPRINT",FACE,{"disambiguationData":[TD([[makeQuery(id+"F1.imprint","IMPRINT",EDGE,{"derivedFrom":subQ7}),-1.0]])]});}
            var Q3;
            {var subQ8=sQuery(id+"F1.wireOp",EDGE,"E51.3.0");Q3=makeQuery(id+"F1.imprint","IMPRINT",FACE,{"disambiguationData":[TD([[makeQuery(id+"F1.imprint","IMPRINT",EDGE,{"derivedFrom":subQ8}),-1.0]])]});}
            var Q4;
            {var subQ2=sQuery(id+"F1.wireOp",EDGE,"E51.4.0");Q4=makeQuery(id+"F1.imprint","IMPRINT",FACE,{"disambiguationData":[TD([[makeQuery(id+"F1.imprint","IMPRINT",EDGE,{"derivedFrom":subQ2}),-1.0]])]});}
            var Q5;
            {var subQ8=sQuery(id+"F1.wireOp",EDGE,"E51.5.0");Q5=makeQuery(id+"F1.imprint","IMPRINT",FACE,{"disambiguationData":[TD([[makeQuery(id+"F1.imprint","IMPRINT",EDGE,{"derivedFrom":subQ8}),-1.0]])]});}
            var Q6;
            {var subQ3=sQuery(id+"F1.wireOp",EDGE,"E51.6.0");Q6=makeQuery(id+"F1.imprint","IMPRINT",FACE,{"disambiguationData":[TD([[makeQuery(id+"F1.imprint","IMPRINT",EDGE,{"derivedFrom":subQ3}),-1.0]])]});}
            var Q7;
            {var subQ0=sQuery(id+"F1.wireOp",EDGE,"E51.7.0");Q7=makeQuery(id+"F1.imprint","IMPRINT",FACE,{"disambiguationData":[TD([[makeQuery(id+"F1.imprint","IMPRINT",EDGE,{"derivedFrom":subQ0}),-1.0]])]});}
            var Q8;
            {var subQ5=sQuery(id+"F1.wireOp",EDGE,"E51.8.0");Q8=makeQuery(id+"F1.imprint","IMPRINT",FACE,{"disambiguationData":[TD([[makeQuery(id+"F1.imprint","IMPRINT",EDGE,{"derivedFrom":subQ5}),-1.0]])]});}
            var Q9;
            {var subQ1=sQuery(id+"F1.wireOp",EDGE,"E51.9.0");Q9=makeQuery(id+"F1.imprint","IMPRINT",FACE,{"disambiguationData":[TD([[makeQuery(id+"F1.imprint","IMPRINT",EDGE,{"derivedFrom":subQ1}),-1.0]])]});}
            var Q10;
            {var subQ5=sQuery(id+"F1.wireOp",EDGE,"E51.10.0");Q10=makeQuery(id+"F1.imprint","IMPRINT",FACE,{"disambiguationData":[TD([[makeQuery(id+"F1.imprint","IMPRINT",EDGE,{"derivedFrom":subQ5}),-1.0]])]});}
            var Q11;
            {var subQ8=sQuery(id+"F1.wireOp",EDGE,"E51.11.0");Q11=makeQuery(id+"F1.imprint","IMPRINT",FACE,{"disambiguationData":[TD([[makeQuery(id+"F1.imprint","IMPRINT",EDGE,{"derivedFrom":subQ8}),-1.0]])]});}
            var Q12;
            {var subQ2=sQuery(id+"F1.wireOp",EDGE,"E51.12.0");Q12=makeQuery(id+"F1.imprint","IMPRINT",FACE,{"disambiguationData":[TD([[makeQuery(id+"F1.imprint","IMPRINT",EDGE,{"derivedFrom":subQ2}),-1.0]])]});}
            var Q13;
            {var subQ3=sQuery(id+"F1.wireOp",EDGE,"E51.13.0");Q13=makeQuery(id+"F1.imprint","IMPRINT",FACE,{"disambiguationData":[TD([[makeQuery(id+"F1.imprint","IMPRINT",EDGE,{"derivedFrom":subQ3}),-1.0]])]});}
            var Q14;
            {var subQ0=sQuery(id+"F1.wireOp",EDGE,"E51.14.0");Q14=makeQuery(id+"F1.imprint","IMPRINT",FACE,{"disambiguationData":[TD([[makeQuery(id+"F1.imprint","IMPRINT",EDGE,{"derivedFrom":subQ0}),-1.0]])]});}
            var Q15;
            {var subQ6=sQuery(id+"F1.wireOp",EDGE,"E51.15.0");Q15=makeQuery(id+"F1.imprint","IMPRINT",FACE,{"disambiguationData":[TD([[makeQuery(id+"F1.imprint","IMPRINT",EDGE,{"derivedFrom":subQ6}),-1.0]])]});}
            var Q16;
            {var subQ5=sQuery(id+"F1.wireOp",EDGE,"E51.16.0");Q16=makeQuery(id+"F1.imprint","IMPRINT",FACE,{"disambiguationData":[TD([[makeQuery(id+"F1.imprint","IMPRINT",EDGE,{"derivedFrom":subQ5}),-1.0]])]});}
            var Q17;
            {var subQ7=sQuery(id+"F1.wireOp",EDGE,"E51.17.0");Q17=makeQuery(id+"F1.imprint","IMPRINT",FACE,{"disambiguationData":[TD([[makeQuery(id+"F1.imprint","IMPRINT",EDGE,{"derivedFrom":subQ7}),-1.0]])]});}
            var Q18;
            {var subQ5=sQuery(id+"F1.wireOp",EDGE,"E51.18.0");Q18=makeQuery(id+"F1.imprint","IMPRINT",FACE,{"disambiguationData":[TD([[makeQuery(id+"F1.imprint","IMPRINT",EDGE,{"derivedFrom":subQ5}),-1.0]])]});}
            var Q19;
            {var subQ8=sQuery(id+"F1.wireOp",EDGE,"E51.19.0");Q19=makeQuery(id+"F1.imprint","IMPRINT",FACE,{"disambiguationData":[TD([[makeQuery(id+"F1.imprint","IMPRINT",EDGE,{"derivedFrom":subQ8}),-1.0]])]});}
            var Q20;
            {var subQ8=sQuery(id+"F1.wireOp",EDGE,"E21");Q20=makeQuery(id+"F1.imprint","IMPRINT",FACE,{"disambiguationData":[TD([[makeQuery(id+"F1.imprint","IMPRINT",EDGE,{"derivedFrom":subQ8}),-1.0]])]});}
            extrude(context, id + "F2", {"entities" : qUnion([Q0, Q1, Q2, Q3, Q4, Q5, Q6, Q7, Q8, Q9, Q10, Q11, Q12, Q13, Q14, Q15, Q16, Q17, Q18, Q19, Q20]), "depth" : (getVariable(context, 'GearThickness')) * mm});
        }
    });
